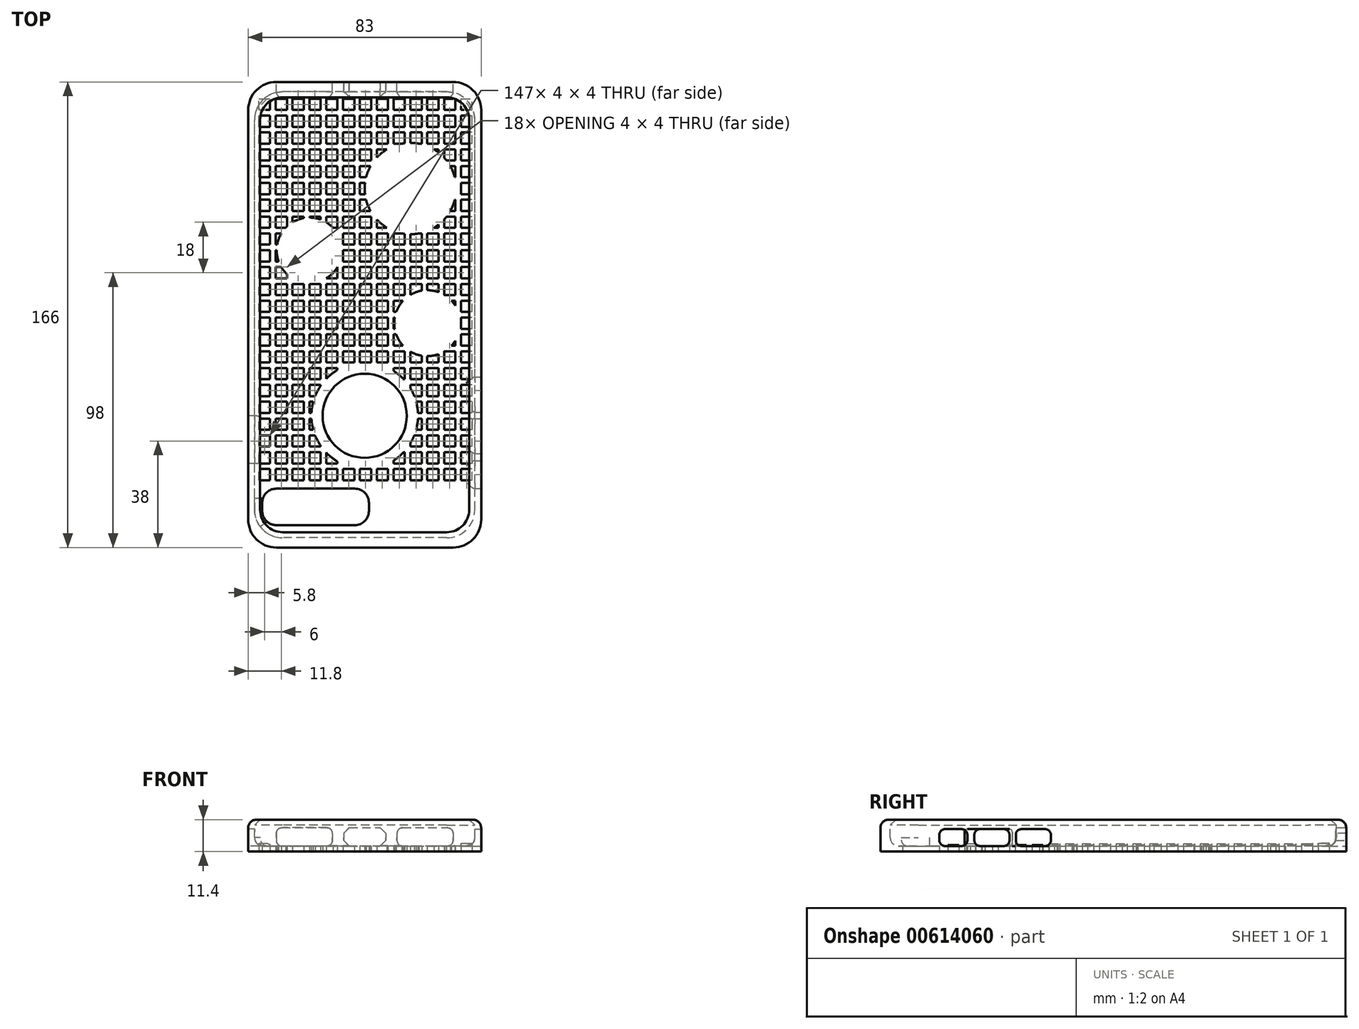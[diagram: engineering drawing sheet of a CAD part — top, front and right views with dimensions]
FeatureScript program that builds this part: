
annotation { "Feature Type Name" : "Feature", "Feature Type Description" : "" }
export const myFeature = defineFeature(function(context is Context, id is Id, definition is map)
    precondition{}
    {
        {
            var Q0;
            Q0=qCreatedBy(makeId("Top.planeOp"),FACE);
            var sketch = newSketch(context, id + "F0", { "sketchPlane" : qUnion([Q0])});
            skLineSegment(sketch, "E0.bottom", {"start": v(41.5, 83) * mm, "end": v(-41.5, 83) * mm});
            skLineSegment(sketch, "E0.top", {"start": v(41.5, -83) * mm, "end": v(-41.5, -83) * mm});
            skLineSegment(sketch, "E0.left", {"start": v(41.5, 83) * mm, "end": v(41.5, -83) * mm});
            skLineSegment(sketch, "E0.right", {"start": v(-41.5, 83) * mm, "end": v(-41.5, -83) * mm});
            skPoint(sketch, "E0.middle", {"position": v(0, 0) * mm});
            skSolve(sketch);
        }
        {
            var Q0;
            Q0=makeQuery(id+"F0.imprint","IMPRINT",FACE,{"disambiguationData":[TD([[makeQuery(id+"F0.imprint","IMPRINT",EDGE,{"derivedFrom":sQuery(id+"F0.wireOp",EDGE,"E0.bottom")}),1.0]])]});
            extrude(context, id + "F1", {"entities" : qUnion([Q0]), "depth" : 9.4 * mm});
        }
        {
            var Q0;
            Q0=makeQuery(id+"F1.opExtrude","CAP_FACE",FACE,{"disambiguationData":[OSD([sQuery(id+"F0.wireOp",EDGE,"E0.bottom"),sQuery(id+"F0.wireOp",EDGE,"E0.top"),sQuery(id+"F0.wireOp",EDGE,"E0.left"),sQuery(id+"F0.wireOp",EDGE,"E0.right")])],"isStart":false});
            var sketch = newSketch(context, id + "F2", { "sketchPlane" : qUnion([Q0])});
            skLineSegment(sketch, "E1.bottom", {"start": v(39.25, -79.5) * mm, "end": v(-39.25, -79.5) * mm});
            skLineSegment(sketch, "E1.top", {"start": v(39.25, 79.5) * mm, "end": v(-39.25, 79.5) * mm});
            skLineSegment(sketch, "E1.left", {"start": v(39.25, -79.5) * mm, "end": v(39.25, 79.5) * mm});
            skLineSegment(sketch, "E1.right", {"start": v(-39.25, -79.5) * mm, "end": v(-39.25, 79.5) * mm});
            skPoint(sketch, "E1.middle", {"position": v(0, 0) * mm});
            skSolve(sketch);
        }
        {
            var Q0;
            Q0=makeQuery(id+"F2.imprint","IMPRINT",FACE,{"disambiguationData":[TD([[makeQuery(id+"F2.imprint","IMPRINT",EDGE,{"derivedFrom":sQuery(id+"F2.wireOp",EDGE,"E1.bottom")}),-1.0]])]});
            extrude(context, id + "F3", {"entities" : qUnion([Q0]), "operationType" : NewBodyOperationType.REMOVE, "oppositeDirection" : true, "depth" : 7.4 * mm});
        }
        {
            var Q0;
            Q0=makeQuery(id+"F3.boolean.opBoolean","COPY",EDGE,{"derivedFrom":makeQuery(id+"F3.opExtrude","SWEPT_EDGE",EDGE,{"disambiguationData":[OSD([sQuery(id+"F2.wireOp",EDGE,"E1.top"),sQuery(id+"F2.wireOp",EDGE,"E1.left")])]})});
            var Q1;
            Q1=makeQuery(id+"F3.boolean.opBoolean","COPY",EDGE,{"derivedFrom":makeQuery(id+"F3.opExtrude","SWEPT_EDGE",EDGE,{"disambiguationData":[OSD([sQuery(id+"F2.wireOp",EDGE,"E1.top"),sQuery(id+"F2.wireOp",EDGE,"E1.right")])]})});
            var Q2;
            Q2=makeQuery(id+"F3.boolean.opBoolean","COPY",EDGE,{"derivedFrom":makeQuery(id+"F3.opExtrude","SWEPT_EDGE",EDGE,{"disambiguationData":[OSD([sQuery(id+"F2.wireOp",EDGE,"E1.bottom"),sQuery(id+"F2.wireOp",EDGE,"E1.left")])]})});
            var Q3;
            Q3=makeQuery(id+"F3.boolean.opBoolean","COPY",EDGE,{"derivedFrom":makeQuery(id+"F3.opExtrude","SWEPT_EDGE",EDGE,{"disambiguationData":[OSD([sQuery(id+"F2.wireOp",EDGE,"E1.bottom"),sQuery(id+"F2.wireOp",EDGE,"E1.right")])]})});
            fillet(context, id + "F4", {"entities" : qUnion([Q0, Q1, Q2, Q3]), "radius" : 10 * mm, "tangentPropagation" : true, "allowEdgeOverflow" : false});
        }
        {
            var Q0;
            Q0=makeQuery(id+"F1.opExtrude","CAP_FACE",FACE,{"disambiguationData":[OSD([sQuery(id+"F0.wireOp",EDGE,"E0.bottom"),sQuery(id+"F0.wireOp",EDGE,"E0.top"),sQuery(id+"F0.wireOp",EDGE,"E0.left"),sQuery(id+"F0.wireOp",EDGE,"E0.right")])],"isStart":true});
            var sketch = newSketch(context, id + "F5", { "sketchPlane" : qUnion([Q0])});
            skLineSegment(sketch, "E2.bottom", {"start": v(1.5, 62) * mm, "end": v(-36.5, 62) * mm});
            skLineSegment(sketch, "E2.top", {"start": v(1.5, 75) * mm, "end": v(-36.5, 75) * mm});
            skLineSegment(sketch, "E2.left", {"start": v(-36.5, 62) * mm, "end": v(-36.5, 75) * mm});
            skLineSegment(sketch, "E2.right", {"start": v(1.5, 62) * mm, "end": v(1.5, 75) * mm});
            skSolve(sketch);
        }
        {
            var Q0;
            Q0=makeQuery(id+"F5.imprint","IMPRINT",FACE,{"disambiguationData":[TD([[makeQuery(id+"F5.imprint","IMPRINT",EDGE,{"derivedFrom":sQuery(id+"F5.wireOp",EDGE,"E2.bottom")}),-1.0]])]});
            extrude(context, id + "F6", {"entities" : qUnion([Q0]), "operationType" : NewBodyOperationType.REMOVE, "oppositeDirection" : true, "depth" : 25 * mm});
        }
        {
            var Q0;
            Q0=makeQuery(id+"F1.opExtrude","SWEPT_EDGE",EDGE,{"disambiguationData":[OSD([sQuery(id+"F0.wireOp",EDGE,"E0.top"),sQuery(id+"F0.wireOp",EDGE,"E0.right")])]});
            var Q1;
            Q1=makeQuery(id+"F1.opExtrude","SWEPT_EDGE",EDGE,{"disambiguationData":[OSD([sQuery(id+"F0.wireOp",EDGE,"E0.top"),sQuery(id+"F0.wireOp",EDGE,"E0.left")])]});
            var Q2;
            Q2=makeQuery(id+"F1.opExtrude","SWEPT_EDGE",EDGE,{"disambiguationData":[OSD([sQuery(id+"F0.wireOp",EDGE,"E0.bottom"),sQuery(id+"F0.wireOp",EDGE,"E0.right")])]});
            var Q3;
            Q3=makeQuery(id+"F1.opExtrude","SWEPT_EDGE",EDGE,{"disambiguationData":[OSD([sQuery(id+"F0.wireOp",EDGE,"E0.bottom"),sQuery(id+"F0.wireOp",EDGE,"E0.left")])]});
            fillet(context, id + "F7", {"entities" : qUnion([Q0, Q1, Q2, Q3]), "radius" : 10 * mm, "tangentPropagation" : true, "allowEdgeOverflow" : false});
        }
        {
            var Q0;
            Q0=makeQuery(id+"F6.boolean.opBoolean","COPY",EDGE,{"derivedFrom":makeQuery(id+"F6.opExtrude","SWEPT_EDGE",EDGE,{"disambiguationData":[OSD([sQuery(id+"F5.wireOp",EDGE,"E2.top"),sQuery(id+"F5.wireOp",EDGE,"E2.left")])]})});
            var Q1;
            Q1=makeQuery(id+"F6.boolean.opBoolean","COPY",EDGE,{"derivedFrom":makeQuery(id+"F6.opExtrude","SWEPT_EDGE",EDGE,{"disambiguationData":[OSD([sQuery(id+"F5.wireOp",EDGE,"E2.bottom"),sQuery(id+"F5.wireOp",EDGE,"E2.left")])]})});
            var Q2;
            Q2=makeQuery(id+"F6.boolean.opBoolean","COPY",EDGE,{"derivedFrom":makeQuery(id+"F6.opExtrude","SWEPT_EDGE",EDGE,{"disambiguationData":[OSD([sQuery(id+"F5.wireOp",EDGE,"E2.top"),sQuery(id+"F5.wireOp",EDGE,"E2.right")])]})});
            var Q3;
            Q3=makeQuery(id+"F6.boolean.opBoolean","COPY",EDGE,{"derivedFrom":makeQuery(id+"F6.opExtrude","SWEPT_EDGE",EDGE,{"disambiguationData":[OSD([sQuery(id+"F5.wireOp",EDGE,"E2.bottom"),sQuery(id+"F5.wireOp",EDGE,"E2.right")])]})});
            fillet(context, id + "F8", {"entities" : qUnion([Q0, Q1, Q2, Q3]), "radius" : 5 * mm, "tangentPropagation" : true, "allowEdgeOverflow" : false});
        }
        {
            var Q0;
            Q0=makeQuery(id+"F1.opExtrude","SWEPT_FACE",FACE,{"disambiguationData":[OSD([sQuery(id+"F0.wireOp",EDGE,"E0.bottom")])]});
            var sketch = newSketch(context, id + "F9", { "sketchPlane" : qUnion([Q0])});
            skLineSegment(sketch, "E3.bottom", {"start": v(7.5, 8.5) * mm, "end": v(-7.5, 8.5) * mm});
            skLineSegment(sketch, "E3.top", {"start": v(7.5, 2) * mm, "end": v(-7.5, 2) * mm});
            skLineSegment(sketch, "E3.left", {"start": v(7.5, 8.5) * mm, "end": v(7.5, 2) * mm});
            skLineSegment(sketch, "E3.right", {"start": v(-7.5, 8.5) * mm, "end": v(-7.5, 2) * mm});
            skPoint(sketch, "E3.middle", {"position": v(0, 5.25) * mm});
            skLineSegment(sketch, "E4.bottom", {"start": v(-11.5, 8.5) * mm, "end": v(-31.5, 8.5) * mm});
            skLineSegment(sketch, "E4.top", {"start": v(-11.5, 2) * mm, "end": v(-31.5, 2) * mm});
            skLineSegment(sketch, "E4.left", {"start": v(-11.5, 8.5) * mm, "end": v(-11.5, 2) * mm});
            skLineSegment(sketch, "E4.right", {"start": v(-31.5, 8.5) * mm, "end": v(-31.5, 2) * mm});
            skLineSegment(sketch, "E5.bottom", {"start": v(11.5, 8.5) * mm, "end": v(31.5, 8.5) * mm});
            skLineSegment(sketch, "E5.top", {"start": v(11.5, 2) * mm, "end": v(31.5, 2) * mm});
            skLineSegment(sketch, "E5.left", {"start": v(11.5, 8.5) * mm, "end": v(11.5, 2) * mm});
            skLineSegment(sketch, "E5.right", {"start": v(31.5, 8.5) * mm, "end": v(31.5, 2) * mm});
            skSolve(sketch);
        }
        {
            var Q0;
            Q0=qSketchRegion(id+"F9",true);
            extrude(context, id + "F10", {"entities" : qUnion([Q0]), "operationType" : NewBodyOperationType.REMOVE, "oppositeDirection" : true, "depth" : 25 * mm});
        }
        {
            var Q0;
            Q0=makeQuery(id+"F1.opExtrude","SWEPT_FACE",FACE,{"disambiguationData":[OSD([sQuery(id+"F0.wireOp",EDGE,"E0.left")])]});
            var sketch = newSketch(context, id + "F11", { "sketchPlane" : qUnion([Q0])});
            skLineSegment(sketch, "E6.bottom", {"start": v(-62, 8) * mm, "end": v(-52, 8) * mm});
            skLineSegment(sketch, "E6.top", {"start": v(-62, 2) * mm, "end": v(-52, 2) * mm});
            skLineSegment(sketch, "E6.left", {"start": v(-62, 8) * mm, "end": v(-62, 2) * mm});
            skLineSegment(sketch, "E6.right", {"start": v(-52, 8) * mm, "end": v(-52, 2) * mm});
            skLineSegment(sketch, "E7.bottom", {"start": v(-49.5, 2) * mm, "end": v(-37, 2) * mm});
            skLineSegment(sketch, "E7.top", {"start": v(-49.5, 8) * mm, "end": v(-37, 8) * mm});
            skLineSegment(sketch, "E7.left", {"start": v(-49.5, 2) * mm, "end": v(-49.5, 8) * mm});
            skLineSegment(sketch, "E7.right", {"start": v(-37, 2) * mm, "end": v(-37, 8) * mm});
            skLineSegment(sketch, "E8.bottom", {"start": v(-34.74, 2) * mm, "end": v(-22.24, 2) * mm});
            skLineSegment(sketch, "E8.top", {"start": v(-34.74, 8) * mm, "end": v(-22.24, 8) * mm});
            skLineSegment(sketch, "E8.left", {"start": v(-34.74, 2) * mm, "end": v(-34.74, 8) * mm});
            skLineSegment(sketch, "E8.right", {"start": v(-22.24, 2) * mm, "end": v(-22.24, 8) * mm});
            skSolve(sketch);
        }
        {
            var Q0;
            Q0=makeQuery(id+"F11.imprint","IMPRINT",FACE,{"disambiguationData":[TD([[makeQuery(id+"F11.imprint","IMPRINT",EDGE,{"derivedFrom":sQuery(id+"F11.wireOp",EDGE,"E6.bottom")}),-1.0]])]});
            var Q1;
            Q1=makeQuery(id+"F11.imprint","IMPRINT",FACE,{"disambiguationData":[TD([[makeQuery(id+"F11.imprint","IMPRINT",EDGE,{"derivedFrom":sQuery(id+"F11.wireOp",EDGE,"E7.bottom")}),1.0]])]});
            var Q2;
            Q2=makeQuery(id+"F11.imprint","IMPRINT",FACE,{"disambiguationData":[TD([[makeQuery(id+"F11.imprint","IMPRINT",EDGE,{"derivedFrom":sQuery(id+"F11.wireOp",EDGE,"E8.bottom")}),1.0]])]});
            extrude(context, id + "F12", {"entities" : qUnion([Q0, Q1, Q2]), "operationType" : NewBodyOperationType.REMOVE, "oppositeDirection" : true, "depth" : 3 * mm});
        }
        {
            var Q0;
            Q0=makeQuery(id+"F1.opExtrude","SWEPT_FACE",FACE,{"disambiguationData":[OSD([sQuery(id+"F0.wireOp",EDGE,"E0.right")])]});
            var sketch = newSketch(context, id + "F13", { "sketchPlane" : qUnion([Q0])});
            skLineSegment(sketch, "E9.bottom", {"start": v(53, 8) * mm, "end": v(36, 8) * mm});
            skLineSegment(sketch, "E9.top", {"start": v(53, 2) * mm, "end": v(36, 2) * mm});
            skLineSegment(sketch, "E9.left", {"start": v(53, 8) * mm, "end": v(53, 2) * mm});
            skLineSegment(sketch, "E9.right", {"start": v(36, 8) * mm, "end": v(36, 2) * mm});
            skSolve(sketch);
        }
        {
            var Q0;
            Q0=makeQuery(id+"F13.imprint","IMPRINT",FACE,{"disambiguationData":[TD([[makeQuery(id+"F13.imprint","IMPRINT",EDGE,{"derivedFrom":sQuery(id+"F13.wireOp",EDGE,"E9.bottom")}),1.0]])]});
            extrude(context, id + "F14", {"entities" : qUnion([Q0]), "operationType" : NewBodyOperationType.REMOVE, "oppositeDirection" : true, "depth" : 5 * mm});
        }
        {
            var Q0;
            Q0=makeQuery(id+"F1.opExtrude","CAP_FACE",FACE,{"disambiguationData":[OSD([sQuery(id+"F0.wireOp",EDGE,"E0.bottom"),sQuery(id+"F0.wireOp",EDGE,"E0.top"),sQuery(id+"F0.wireOp",EDGE,"E0.left"),sQuery(id+"F0.wireOp",EDGE,"E0.right")])],"isStart":false});
            var sketch = newSketch(context, id + "F15", { "sketchPlane" : qUnion([Q0])});
            skArc(sketch, "E10.0", {"start": v(-31.5, 83) * mm, "mid": v(-38.57, 80.07) * mm, "end": v(-41.5, 73) * mm});
            skLineSegment(sketch, "E11.0", {"start": v(31.5, 83) * mm, "end": v(-31.5, 83) * mm});
            skArc(sketch, "E12.0", {"start": v(41.5, 73) * mm, "mid": v(38.57, 80.07) * mm, "end": v(31.5, 83) * mm});
            skLineSegment(sketch, "E13.0", {"start": v(41.5, 73) * mm, "end": v(41.5, -73) * mm});
            skArc(sketch, "E14.0", {"start": v(31.5, -83) * mm, "mid": v(38.57, -80.07) * mm, "end": v(41.5, -73) * mm});
            skLineSegment(sketch, "E15.0", {"start": v(31.5, -83) * mm, "end": v(-31.5, -83) * mm});
            skArc(sketch, "E16.0", {"start": v(-41.5, -73) * mm, "mid": v(-38.57, -80.07) * mm, "end": v(-31.5, -83) * mm});
            skLineSegment(sketch, "E17.0", {"start": v(-41.5, 73) * mm, "end": v(-41.5, -73) * mm});
            skLineSegment(sketch, "E18.0", {"start": v(-36.25, -69.5) * mm, "end": v(-36.25, 69.5) * mm});
            skArc(sketch, "E18.1", {"start": v(-29.25, -76.5) * mm, "mid": v(-34.2, -74.45) * mm, "end": v(-36.25, -69.5) * mm});
            skArc(sketch, "E18.2", {"start": v(-36.25, 69.5) * mm, "mid": v(-34.2, 74.45) * mm, "end": v(-29.25, 76.5) * mm});
            skLineSegment(sketch, "E18.3", {"start": v(29.25, -76.5) * mm, "end": v(-29.25, -76.5) * mm});
            skLineSegment(sketch, "E18.4", {"start": v(29.25, 76.5) * mm, "end": v(-29.25, 76.5) * mm});
            skArc(sketch, "E18.5", {"start": v(29.25, 76.5) * mm, "mid": v(34.2, 74.45) * mm, "end": v(36.25, 69.5) * mm});
            skLineSegment(sketch, "E18.6", {"start": v(36.25, -69.5) * mm, "end": v(36.25, 69.5) * mm});
            skArc(sketch, "E18.7", {"start": v(36.25, -69.5) * mm, "mid": v(34.2, -74.45) * mm, "end": v(29.25, -76.5) * mm});
            skSolve(sketch);
        }
        {
            var Q0;
            Q0=qSketchRegion(id+"F15",true);
            extrude(context, id + "F16", {"entities" : qUnion([Q0]), "operationType" : NewBodyOperationType.ADD, "depth" : 2 * mm});
        }
        {
            var Q0;
            Q0=makeQuery(id+"F16.opExtrude","CAP_EDGE",EDGE,{"disambiguationData":[OSD([sQuery(id+"F15.wireOp",EDGE,"70d5f63f-d463-4b85-bbfd-dc065f4d9ea8.0")])],"isStart":true});
            var Q1;
            Q1=makeQuery(id+"F16.opExtrude","CAP_EDGE",EDGE,{"disambiguationData":[OSD([sQuery(id+"F15.wireOp",EDGE,"E18.0")])],"isStart":true});
            chamfer(context, id + "F17", {"entities" : qUnion([Q0, Q1]), "width" : 3 * mm, "tangentPropagation" : true});
        }
        {
            var Q0;
            Q0=makeQuery(id+"F14.boolean.opBoolean","COPY",EDGE,{"derivedFrom":makeQuery(id+"F14.opExtrude","SWEPT_EDGE",EDGE,{"disambiguationData":[OSD([sQuery(id+"F13.wireOp",EDGE,"E9.bottom"),sQuery(id+"F13.wireOp",EDGE,"E9.right")])]})});
            var Q1;
            Q1=makeQuery(id+"F14.boolean.opBoolean","COPY",EDGE,{"derivedFrom":makeQuery(id+"F14.opExtrude","SWEPT_EDGE",EDGE,{"disambiguationData":[OSD([sQuery(id+"F13.wireOp",EDGE,"E9.top"),sQuery(id+"F13.wireOp",EDGE,"E9.right")])]})});
            var Q2;
            Q2=makeQuery(id+"F14.boolean.opBoolean","COPY",EDGE,{"derivedFrom":makeQuery(id+"F14.opExtrude","SWEPT_EDGE",EDGE,{"disambiguationData":[OSD([sQuery(id+"F13.wireOp",EDGE,"E9.top"),sQuery(id+"F13.wireOp",EDGE,"E9.left")])]})});
            var Q3;
            Q3=makeQuery(id+"F14.boolean.opBoolean","COPY",EDGE,{"derivedFrom":makeQuery(id+"F14.opExtrude","SWEPT_EDGE",EDGE,{"disambiguationData":[OSD([sQuery(id+"F13.wireOp",EDGE,"E9.bottom"),sQuery(id+"F13.wireOp",EDGE,"E9.left")])]})});
            fillet(context, id + "F18", {"entities" : qUnion([Q0, Q1, Q2, Q3]), "radius" : 1 * mm, "tangentPropagation" : true, "allowEdgeOverflow" : false});
        }
        {
            var Q0;
            Q0=makeQuery(id+"F12.boolean.opBoolean","COPY",EDGE,{"derivedFrom":makeQuery(id+"F12.opExtrude","SWEPT_EDGE",EDGE,{"disambiguationData":[OSD([sQuery(id+"F11.wireOp",EDGE,"E6.top"),sQuery(id+"F11.wireOp",EDGE,"E6.right")])]})});
            var Q1;
            Q1=makeQuery(id+"F12.boolean.opBoolean","COPY",EDGE,{"derivedFrom":makeQuery(id+"F12.opExtrude","SWEPT_EDGE",EDGE,{"disambiguationData":[OSD([sQuery(id+"F11.wireOp",EDGE,"E7.bottom"),sQuery(id+"F11.wireOp",EDGE,"E7.right")])]})});
            var Q2;
            Q2=makeQuery(id+"F12.boolean.opBoolean","COPY",EDGE,{"derivedFrom":makeQuery(id+"F12.opExtrude","SWEPT_EDGE",EDGE,{"disambiguationData":[OSD([sQuery(id+"F11.wireOp",EDGE,"E8.bottom"),sQuery(id+"F11.wireOp",EDGE,"E8.right")])]})});
            var Q3;
            Q3=makeQuery(id+"F12.boolean.opBoolean","COPY",EDGE,{"derivedFrom":makeQuery(id+"F12.opExtrude","SWEPT_EDGE",EDGE,{"disambiguationData":[OSD([sQuery(id+"F11.wireOp",EDGE,"E7.bottom"),sQuery(id+"F11.wireOp",EDGE,"E7.left")])]})});
            var Q4;
            Q4=makeQuery(id+"F12.boolean.opBoolean","COPY",EDGE,{"derivedFrom":makeQuery(id+"F12.opExtrude","SWEPT_EDGE",EDGE,{"disambiguationData":[OSD([sQuery(id+"F11.wireOp",EDGE,"E8.bottom"),sQuery(id+"F11.wireOp",EDGE,"E8.left")])]})});
            var Q5;
            Q5=makeQuery(id+"F12.boolean.opBoolean","COPY",EDGE,{"derivedFrom":makeQuery(id+"F12.opExtrude","SWEPT_EDGE",EDGE,{"disambiguationData":[OSD([sQuery(id+"F11.wireOp",EDGE,"E6.top"),sQuery(id+"F11.wireOp",EDGE,"E6.left")])]})});
            var Q6;
            Q6=makeQuery(id+"F12.boolean.opBoolean","COPY",EDGE,{"derivedFrom":makeQuery(id+"F12.opExtrude","SWEPT_EDGE",EDGE,{"disambiguationData":[OSD([sQuery(id+"F11.wireOp",EDGE,"E6.bottom"),sQuery(id+"F11.wireOp",EDGE,"E6.left")])]})});
            var Q7;
            Q7=makeQuery(id+"F12.boolean.opBoolean","COPY",EDGE,{"derivedFrom":makeQuery(id+"F12.opExtrude","SWEPT_EDGE",EDGE,{"disambiguationData":[OSD([sQuery(id+"F11.wireOp",EDGE,"E7.top"),sQuery(id+"F11.wireOp",EDGE,"E7.left")])]})});
            var Q8;
            Q8=makeQuery(id+"F12.boolean.opBoolean","COPY",EDGE,{"derivedFrom":makeQuery(id+"F12.opExtrude","SWEPT_EDGE",EDGE,{"disambiguationData":[OSD([sQuery(id+"F11.wireOp",EDGE,"E8.top"),sQuery(id+"F11.wireOp",EDGE,"E8.left")])]})});
            var Q9;
            Q9=makeQuery(id+"F12.boolean.opBoolean","COPY",EDGE,{"derivedFrom":makeQuery(id+"F12.opExtrude","SWEPT_EDGE",EDGE,{"disambiguationData":[OSD([sQuery(id+"F11.wireOp",EDGE,"E8.top"),sQuery(id+"F11.wireOp",EDGE,"E8.right")])]})});
            var Q10;
            Q10=makeQuery(id+"F12.boolean.opBoolean","COPY",EDGE,{"derivedFrom":makeQuery(id+"F12.opExtrude","SWEPT_EDGE",EDGE,{"disambiguationData":[OSD([sQuery(id+"F11.wireOp",EDGE,"E7.top"),sQuery(id+"F11.wireOp",EDGE,"E7.right")])]})});
            var Q11;
            Q11=makeQuery(id+"F12.boolean.opBoolean","COPY",EDGE,{"derivedFrom":makeQuery(id+"F12.opExtrude","SWEPT_EDGE",EDGE,{"disambiguationData":[OSD([sQuery(id+"F11.wireOp",EDGE,"E6.bottom"),sQuery(id+"F11.wireOp",EDGE,"E6.right")])]})});
            fillet(context, id + "F19", {"entities" : qUnion([Q0, Q1, Q2, Q3, Q4, Q5, Q6, Q7, Q8, Q9, Q10, Q11]), "radius" : 2 * mm, "tangentPropagation" : true, "allowEdgeOverflow" : false});
        }
        {
            var Q0;
            Q0=makeQuery(id+"F10.boolean.opBoolean","COPY",EDGE,{"derivedFrom":makeQuery(id+"F10.opExtrude","SWEPT_EDGE",EDGE,{"disambiguationData":[OSD([sQuery(id+"F9.wireOp",EDGE,"E3.bottom"),sQuery(id+"F9.wireOp",EDGE,"E3.right")])]})});
            var Q1;
            Q1=makeQuery(id+"F10.boolean.opBoolean","COPY",EDGE,{"derivedFrom":makeQuery(id+"F10.opExtrude","SWEPT_EDGE",EDGE,{"disambiguationData":[OSD([sQuery(id+"F9.wireOp",EDGE,"E3.top"),sQuery(id+"F9.wireOp",EDGE,"E3.left")])]})});
            var Q2;
            Q2=makeQuery(id+"F10.boolean.opBoolean","COPY",EDGE,{"derivedFrom":makeQuery(id+"F10.opExtrude","SWEPT_EDGE",EDGE,{"disambiguationData":[OSD([sQuery(id+"F9.wireOp",EDGE,"E3.bottom"),sQuery(id+"F9.wireOp",EDGE,"E3.left")])]})});
            var Q3;
            Q3=makeQuery(id+"F10.boolean.opBoolean","COPY",EDGE,{"derivedFrom":makeQuery(id+"F10.opExtrude","SWEPT_EDGE",EDGE,{"disambiguationData":[OSD([sQuery(id+"F9.wireOp",EDGE,"E3.top"),sQuery(id+"F9.wireOp",EDGE,"E3.right")])]})});
            chamfer(context, id + "F20", {"entities" : qUnion([Q0, Q1, Q2, Q3]), "width" : 2 * mm, "tangentPropagation" : true});
        }
        {
            var Q0;
            Q0=makeQuery(id+"F10.boolean.opBoolean","COPY",EDGE,{"derivedFrom":makeQuery(id+"F10.opExtrude","SWEPT_EDGE",EDGE,{"disambiguationData":[OSD([sQuery(id+"F9.wireOp",EDGE,"E4.bottom"),sQuery(id+"F9.wireOp",EDGE,"E4.left")])]})});
            var Q1;
            Q1=makeQuery(id+"F10.boolean.opBoolean","COPY",EDGE,{"derivedFrom":makeQuery(id+"F10.opExtrude","SWEPT_EDGE",EDGE,{"disambiguationData":[OSD([sQuery(id+"F0.wireOp",EDGE,"E0.bottom"),sQuery(id+"F0.wireOp",EDGE,"E0.right"),sQuery(id+"F9.wireOp",EDGE,"E5.bottom"),sQuery(id+"F9.wireOp",EDGE,"E5.right")])]})});
            var Q2;
            Q2=makeQuery(id+"F10.boolean.opBoolean","COPY",EDGE,{"derivedFrom":makeQuery(id+"F10.opExtrude","SWEPT_EDGE",EDGE,{"disambiguationData":[OSD([sQuery(id+"F0.wireOp",EDGE,"E0.bottom"),sQuery(id+"F0.wireOp",EDGE,"E0.right"),sQuery(id+"F9.wireOp",EDGE,"E5.top"),sQuery(id+"F9.wireOp",EDGE,"E5.right")])]})});
            var Q3;
            Q3=makeQuery(id+"F10.boolean.opBoolean","COPY",EDGE,{"derivedFrom":makeQuery(id+"F10.opExtrude","SWEPT_EDGE",EDGE,{"disambiguationData":[OSD([sQuery(id+"F9.wireOp",EDGE,"E4.top"),sQuery(id+"F9.wireOp",EDGE,"E4.left")])]})});
            var Q4;
            Q4=makeQuery(id+"F10.boolean.opBoolean","COPY",EDGE,{"derivedFrom":makeQuery(id+"F10.opExtrude","SWEPT_EDGE",EDGE,{"disambiguationData":[OSD([sQuery(id+"F0.wireOp",EDGE,"E0.bottom"),sQuery(id+"F0.wireOp",EDGE,"E0.left"),sQuery(id+"F9.wireOp",EDGE,"E4.top"),sQuery(id+"F9.wireOp",EDGE,"E4.right")])]})});
            var Q5;
            Q5=makeQuery(id+"F10.boolean.opBoolean","COPY",EDGE,{"derivedFrom":makeQuery(id+"F10.opExtrude","SWEPT_EDGE",EDGE,{"disambiguationData":[OSD([sQuery(id+"F9.wireOp",EDGE,"E5.top"),sQuery(id+"F9.wireOp",EDGE,"E5.left")])]})});
            var Q6;
            Q6=makeQuery(id+"F10.boolean.opBoolean","COPY",EDGE,{"derivedFrom":makeQuery(id+"F10.opExtrude","SWEPT_EDGE",EDGE,{"disambiguationData":[OSD([sQuery(id+"F9.wireOp",EDGE,"E5.bottom"),sQuery(id+"F9.wireOp",EDGE,"E5.left")])]})});
            var Q7;
            Q7=makeQuery(id+"F10.boolean.opBoolean","COPY",EDGE,{"derivedFrom":makeQuery(id+"F10.opExtrude","SWEPT_EDGE",EDGE,{"disambiguationData":[OSD([sQuery(id+"F0.wireOp",EDGE,"E0.bottom"),sQuery(id+"F0.wireOp",EDGE,"E0.left"),sQuery(id+"F9.wireOp",EDGE,"E4.bottom"),sQuery(id+"F9.wireOp",EDGE,"E4.right")])]})});
            fillet(context, id + "F21", {"entities" : qUnion([Q0, Q1, Q2, Q3, Q4, Q5, Q6, Q7]), "radius" : 2 * mm, "tangentPropagation" : true, "allowEdgeOverflow" : false});
        }
        {
            var Q0;
            Q0=makeQuery(id+"F16.opExtrude","CAP_EDGE",EDGE,{"disambiguationData":[OSD([sQuery(id+"F15.wireOp",EDGE,"E13.0")])],"isStart":false});
            fillet(context, id + "F22", {"entities" : qUnion([Q0]), "radius" : 3 * mm, "tangentPropagation" : true, "allowEdgeOverflow" : false});
        }
        {
            var Q0;
            {var subQ0=sQuery(id+"F2.wireOp",EDGE,"E1.right");Q0=makeQuery(id+"F14.boolean.opBoolean","SPLIT",EDGE,{"disambiguationData":[TD([makeQuery(id+"F14.opExtrude","SWEPT_FACE",FACE,{"disambiguationData":[OSD([sQuery(id+"F13.wireOp",EDGE,"E9.left")])]})])],"derivedFrom":makeQuery(id+"F3.boolean.opBoolean","COPY",EDGE,{"derivedFrom":makeQuery(id+"F3.opExtrude","CAP_EDGE",EDGE,{"disambiguationData":[OSD([subQ0])],"isStart":false})})});}
            var Q1;
            {var subQ0=sQuery(id+"F2.wireOp",EDGE,"E1.right");Q1=makeQuery(id+"FE60Vq3lKrfm1dI_2.splitOp","SPLIT",EDGE,{"derivedFrom":makeQuery(id+"F14.boolean.opBoolean","SPLIT",EDGE,{"disambiguationData":[TD([makeQuery(id+"F14.opExtrude","SWEPT_FACE",FACE,{"disambiguationData":[OSD([sQuery(id+"F13.wireOp",EDGE,"E9.right")])]})])],"derivedFrom":makeQuery(id+"F3.boolean.opBoolean","COPY",EDGE,{"derivedFrom":makeQuery(id+"F3.opExtrude","CAP_EDGE",EDGE,{"disambiguationData":[OSD([subQ0])],"isStart":false})})}),"isFromBackBody":true});}
            var Q2;
            {var subQ0=sQuery(id+"F2.wireOp",EDGE,"E1.right");Q2=makeQuery(id+"FE60Vq3lKrfm1dI_2.splitOp","SPLIT",EDGE,{"derivedFrom":makeQuery(id+"F14.boolean.opBoolean","SPLIT",EDGE,{"disambiguationData":[TD([makeQuery(id+"F14.opExtrude","SWEPT_FACE",FACE,{"disambiguationData":[OSD([sQuery(id+"F13.wireOp",EDGE,"E9.right")])]})])],"derivedFrom":makeQuery(id+"F3.boolean.opBoolean","COPY",EDGE,{"derivedFrom":makeQuery(id+"F3.opExtrude","CAP_EDGE",EDGE,{"disambiguationData":[OSD([subQ0])],"isStart":false})})})});}
            var Q3;
            {var subQ0=sQuery(id+"F2.wireOp",EDGE,"E1.top");Q3=makeQuery(id+"F10.boolean.opBoolean","SPLIT",EDGE,{"disambiguationData":[TD([makeQuery(id+"F10.opExtrude","SWEPT_FACE",FACE,{"disambiguationData":[OSD([sQuery(id+"F9.wireOp",EDGE,"E3.left")])]})])],"derivedFrom":makeQuery(id+"F3.boolean.opBoolean","COPY",EDGE,{"derivedFrom":makeQuery(id+"F3.opExtrude","CAP_EDGE",EDGE,{"disambiguationData":[OSD([subQ0])],"isStart":false})})});}
            var Q4;
            {var subQ0=sQuery(id+"F2.wireOp",EDGE,"E1.top");Q4=makeQuery(id+"F10.boolean.opBoolean","SPLIT",EDGE,{"disambiguationData":[TD([makeQuery(id+"F10.opExtrude","SWEPT_FACE",FACE,{"disambiguationData":[OSD([sQuery(id+"F9.wireOp",EDGE,"E3.right")])]})])],"derivedFrom":makeQuery(id+"F3.boolean.opBoolean","COPY",EDGE,{"derivedFrom":makeQuery(id+"F3.opExtrude","CAP_EDGE",EDGE,{"disambiguationData":[OSD([subQ0])],"isStart":false})})});}
            var Q5;
            {var subQ0=sQuery(id+"F2.wireOp",EDGE,"E1.left");var subQ1=sQuery(id+"F2.wireOp",EDGE,"E1.top");Q5=makeQuery(id+"F4.opFillet","BLEND_EDGE",EDGE,{"blendedFrom":[makeQuery(id+"F3.boolean.opBoolean","COPY",EDGE,{"derivedFrom":makeQuery(id+"F3.opExtrude","SWEPT_EDGE",EDGE,{"disambiguationData":[OSD([subQ1,subQ0])]})}),makeQuery(id+"F3.boolean.opBoolean","COPY",FACE,{"derivedFrom":makeQuery(id+"F3.opExtrude","CAP_FACE",FACE,{"disambiguationData":[OSD([sQuery(id+"F2.wireOp",EDGE,"E1.bottom"),subQ1,subQ0,sQuery(id+"F2.wireOp",EDGE,"E1.right")])],"isStart":false})})],"blendedInto":[makeQuery(id+"F3.boolean.opBoolean","COPY",FACE,{"derivedFrom":makeQuery(id+"F3.opExtrude","CAP_FACE",FACE,{"disambiguationData":[OSD([sQuery(id+"F2.wireOp",EDGE,"E1.bottom"),subQ1,subQ0,sQuery(id+"F2.wireOp",EDGE,"E1.right")])],"isStart":false})})]});}
            var Q6;
            {var subQ0=sQuery(id+"F2.wireOp",EDGE,"E1.left");Q6=makeQuery(id+"F12.boolean.opBoolean","SPLIT",EDGE,{"disambiguationData":[TD([makeQuery(id+"F12.opExtrude","SWEPT_FACE",FACE,{"disambiguationData":[OSD([sQuery(id+"F11.wireOp",EDGE,"E7.right")])]})])],"derivedFrom":makeQuery(id+"F3.boolean.opBoolean","COPY",EDGE,{"derivedFrom":makeQuery(id+"F3.opExtrude","CAP_EDGE",EDGE,{"disambiguationData":[OSD([subQ0])],"isStart":false})})});}
            var Q7;
            {var subQ0=sQuery(id+"F2.wireOp",EDGE,"E1.left");Q7=makeQuery(id+"F12.boolean.opBoolean","SPLIT",EDGE,{"disambiguationData":[TD([makeQuery(id+"F12.opExtrude","SWEPT_FACE",FACE,{"disambiguationData":[OSD([sQuery(id+"F11.wireOp",EDGE,"E6.right")])]})])],"derivedFrom":makeQuery(id+"F3.boolean.opBoolean","COPY",EDGE,{"derivedFrom":makeQuery(id+"F3.opExtrude","CAP_EDGE",EDGE,{"disambiguationData":[OSD([subQ0])],"isStart":false})})});}
            var Q8;
            {var subQ0=sQuery(id+"F2.wireOp",EDGE,"E1.left");Q8=makeQuery(id+"FE60Vq3lKrfm1dI_2.splitOp","SPLIT",EDGE,{"derivedFrom":makeQuery(id+"F12.boolean.opBoolean","SPLIT",EDGE,{"disambiguationData":[TD([makeQuery(id+"F12.opExtrude","SWEPT_FACE",FACE,{"disambiguationData":[OSD([sQuery(id+"F11.wireOp",EDGE,"E8.right")])]})])],"derivedFrom":makeQuery(id+"F3.boolean.opBoolean","COPY",EDGE,{"derivedFrom":makeQuery(id+"F3.opExtrude","CAP_EDGE",EDGE,{"disambiguationData":[OSD([subQ0])],"isStart":false})})}),"isFromBackBody":true});}
            fillet(context, id + "F23", {"entities" : qUnion([Q0, Q1, Q2, Q3, Q4, Q5, Q6, Q7, Q8]), "radius" : 3 * mm, "tangentPropagation" : true, "allowEdgeOverflow" : false});
        }
        {
            var Q0;
            Q0=makeQuery(id+"F1.opExtrude","CAP_FACE",FACE,{"disambiguationData":[OSD([sQuery(id+"F0.wireOp",EDGE,"E0.bottom"),sQuery(id+"F0.wireOp",EDGE,"E0.top"),sQuery(id+"F0.wireOp",EDGE,"E0.left"),sQuery(id+"F0.wireOp",EDGE,"E0.right")])],"isStart":true});
            var sketch = newSketch(context, id + "F24", { "sketchPlane" : qUnion([Q0])});
            skLineSegment(sketch, "E19.bottom", {"start": v(-37.7, 59) * mm, "end": v(-33.7, 59) * mm});
            skLineSegment(sketch, "E19.top", {"start": v(-37.7, 55) * mm, "end": v(-33.7, 55) * mm});
            skLineSegment(sketch, "E19.left", {"start": v(-37.7, 59) * mm, "end": v(-37.7, 55) * mm});
            skLineSegment(sketch, "E19.right", {"start": v(-33.7, 59) * mm, "end": v(-33.7, 55) * mm});
            skLineSegment(sketch, "E20.0.1.0", {"start": v(-37.7, 53) * mm, "end": v(-33.7, 53) * mm});
            skLineSegment(sketch, "E20.0.1.1", {"start": v(-37.7, 53) * mm, "end": v(-37.7, 49) * mm});
            skLineSegment(sketch, "E20.0.1.2", {"start": v(-37.7, 49) * mm, "end": v(-33.7, 49) * mm});
            skLineSegment(sketch, "E20.0.1.3", {"start": v(-33.7, 53) * mm, "end": v(-33.7, 49) * mm});
            skLineSegment(sketch, "E20.0.2.0", {"start": v(-37.7, 47) * mm, "end": v(-33.7, 47) * mm});
            skLineSegment(sketch, "E20.0.2.1", {"start": v(-37.7, 47) * mm, "end": v(-37.7, 43) * mm});
            skLineSegment(sketch, "E20.0.2.2", {"start": v(-37.7, 43) * mm, "end": v(-33.7, 43) * mm});
            skLineSegment(sketch, "E20.0.2.3", {"start": v(-33.7, 47) * mm, "end": v(-33.7, 43) * mm});
            skLineSegment(sketch, "E20.0.3.0", {"start": v(-37.7, 41) * mm, "end": v(-33.7, 41) * mm});
            skLineSegment(sketch, "E20.0.3.1", {"start": v(-37.7, 41) * mm, "end": v(-37.7, 37) * mm});
            skLineSegment(sketch, "E20.0.3.2", {"start": v(-37.7, 37) * mm, "end": v(-33.7, 37) * mm});
            skLineSegment(sketch, "E20.0.3.3", {"start": v(-33.7, 41) * mm, "end": v(-33.7, 37) * mm});
            skLineSegment(sketch, "E20.0.4.0", {"start": v(-37.7, 35) * mm, "end": v(-33.7, 35) * mm});
            skLineSegment(sketch, "E20.0.4.1", {"start": v(-37.7, 35) * mm, "end": v(-37.7, 31) * mm});
            skLineSegment(sketch, "E20.0.4.2", {"start": v(-37.7, 31) * mm, "end": v(-33.7, 31) * mm});
            skLineSegment(sketch, "E20.0.4.3", {"start": v(-33.7, 35) * mm, "end": v(-33.7, 31) * mm});
            skLineSegment(sketch, "E20.0.5.0", {"start": v(-37.7, 29) * mm, "end": v(-33.7, 29) * mm});
            skLineSegment(sketch, "E20.0.5.1", {"start": v(-37.7, 29) * mm, "end": v(-37.7, 25) * mm});
            skLineSegment(sketch, "E20.0.5.2", {"start": v(-37.7, 25) * mm, "end": v(-33.7, 25) * mm});
            skLineSegment(sketch, "E20.0.5.3", {"start": v(-33.7, 29) * mm, "end": v(-33.7, 25) * mm});
            skLineSegment(sketch, "E20.0.6.0", {"start": v(-37.7, 23) * mm, "end": v(-33.7, 23) * mm});
            skLineSegment(sketch, "E20.0.6.1", {"start": v(-37.7, 23) * mm, "end": v(-37.7, 19) * mm});
            skLineSegment(sketch, "E20.0.6.2", {"start": v(-37.7, 19) * mm, "end": v(-33.7, 19) * mm});
            skLineSegment(sketch, "E20.0.6.3", {"start": v(-33.7, 23) * mm, "end": v(-33.7, 19) * mm});
            skLineSegment(sketch, "E20.0.7.0", {"start": v(-37.7, 17) * mm, "end": v(-33.7, 17) * mm});
            skLineSegment(sketch, "E20.0.7.1", {"start": v(-37.7, 17) * mm, "end": v(-37.7, 13) * mm});
            skLineSegment(sketch, "E20.0.7.2", {"start": v(-37.7, 13) * mm, "end": v(-33.7, 13) * mm});
            skLineSegment(sketch, "E20.0.7.3", {"start": v(-33.7, 17) * mm, "end": v(-33.7, 13) * mm});
            skLineSegment(sketch, "E20.0.8.0", {"start": v(-37.7, 11) * mm, "end": v(-33.7, 11) * mm});
            skLineSegment(sketch, "E20.0.8.1", {"start": v(-37.7, 11) * mm, "end": v(-37.7, 7) * mm});
            skLineSegment(sketch, "E20.0.8.2", {"start": v(-37.7, 7) * mm, "end": v(-33.7, 7) * mm});
            skLineSegment(sketch, "E20.0.8.3", {"start": v(-33.7, 11) * mm, "end": v(-33.7, 7) * mm});
            skLineSegment(sketch, "E20.0.9.0", {"start": v(-37.7, 5) * mm, "end": v(-33.7, 5) * mm});
            skLineSegment(sketch, "E20.0.9.1", {"start": v(-37.7, 5) * mm, "end": v(-37.7, 1) * mm});
            skLineSegment(sketch, "E20.0.9.2", {"start": v(-37.7, 1) * mm, "end": v(-33.7, 1) * mm});
            skLineSegment(sketch, "E20.0.9.3", {"start": v(-33.7, 5) * mm, "end": v(-33.7, 1) * mm});
            skLineSegment(sketch, "E20.0.10.0", {"start": v(-37.7, -1) * mm, "end": v(-33.7, -1) * mm});
            skLineSegment(sketch, "E20.0.10.1", {"start": v(-37.7, -1) * mm, "end": v(-37.7, -5) * mm});
            skLineSegment(sketch, "E20.0.10.2", {"start": v(-37.7, -5) * mm, "end": v(-33.7, -5) * mm});
            skLineSegment(sketch, "E20.0.10.3", {"start": v(-33.7, -1) * mm, "end": v(-33.7, -5) * mm});
            skLineSegment(sketch, "E20.0.11.0", {"start": v(-37.7, -7) * mm, "end": v(-33.7, -7) * mm});
            skLineSegment(sketch, "E20.0.11.1", {"start": v(-37.7, -7) * mm, "end": v(-37.7, -11) * mm});
            skLineSegment(sketch, "E20.0.11.2", {"start": v(-37.7, -11) * mm, "end": v(-33.7, -11) * mm});
            skLineSegment(sketch, "E20.0.11.3", {"start": v(-33.7, -7) * mm, "end": v(-33.7, -11) * mm});
            skLineSegment(sketch, "E20.0.12.0", {"start": v(-37.7, -13) * mm, "end": v(-33.7, -13) * mm});
            skLineSegment(sketch, "E20.0.12.1", {"start": v(-37.7, -13) * mm, "end": v(-37.7, -17) * mm});
            skLineSegment(sketch, "E20.0.12.2", {"start": v(-37.7, -17) * mm, "end": v(-33.7, -17) * mm});
            skLineSegment(sketch, "E20.0.12.3", {"start": v(-33.7, -13) * mm, "end": v(-33.7, -17) * mm});
            skLineSegment(sketch, "E20.0.13.0", {"start": v(-37.7, -19) * mm, "end": v(-33.7, -19) * mm});
            skLineSegment(sketch, "E20.0.13.1", {"start": v(-37.7, -19) * mm, "end": v(-37.7, -23) * mm});
            skLineSegment(sketch, "E20.0.13.2", {"start": v(-37.7, -23) * mm, "end": v(-33.7, -23) * mm});
            skLineSegment(sketch, "E20.0.13.3", {"start": v(-33.7, -19) * mm, "end": v(-33.7, -23) * mm});
            skLineSegment(sketch, "E20.0.14.0", {"start": v(-37.7, -25) * mm, "end": v(-33.7, -25) * mm});
            skLineSegment(sketch, "E20.0.14.1", {"start": v(-37.7, -25) * mm, "end": v(-37.7, -29) * mm});
            skLineSegment(sketch, "E20.0.14.2", {"start": v(-37.7, -29) * mm, "end": v(-33.7, -29) * mm});
            skLineSegment(sketch, "E20.0.14.3", {"start": v(-33.7, -25) * mm, "end": v(-33.7, -29) * mm});
            skLineSegment(sketch, "E20.1.0.0", {"start": v(-31.7, 59) * mm, "end": v(-27.7, 59) * mm});
            skLineSegment(sketch, "E20.1.0.1", {"start": v(-31.7, 59) * mm, "end": v(-31.7, 55) * mm});
            skLineSegment(sketch, "E20.1.0.2", {"start": v(-31.7, 55) * mm, "end": v(-27.7, 55) * mm});
            skLineSegment(sketch, "E20.1.0.3", {"start": v(-27.7, 59) * mm, "end": v(-27.7, 55) * mm});
            skLineSegment(sketch, "E20.1.1.0", {"start": v(-31.7, 53) * mm, "end": v(-27.7, 53) * mm});
            skLineSegment(sketch, "E20.1.1.1", {"start": v(-31.7, 53) * mm, "end": v(-31.7, 49) * mm});
            skLineSegment(sketch, "E20.1.1.2", {"start": v(-31.7, 49) * mm, "end": v(-27.7, 49) * mm});
            skLineSegment(sketch, "E20.1.1.3", {"start": v(-27.7, 53) * mm, "end": v(-27.7, 49) * mm});
            skLineSegment(sketch, "E20.1.2.0", {"start": v(-31.7, 47) * mm, "end": v(-27.7, 47) * mm});
            skLineSegment(sketch, "E20.1.2.1", {"start": v(-31.7, 47) * mm, "end": v(-31.7, 43) * mm});
            skLineSegment(sketch, "E20.1.2.2", {"start": v(-31.7, 43) * mm, "end": v(-27.7, 43) * mm});
            skLineSegment(sketch, "E20.1.2.3", {"start": v(-27.7, 47) * mm, "end": v(-27.7, 43) * mm});
            skLineSegment(sketch, "E20.1.3.0", {"start": v(-31.7, 41) * mm, "end": v(-27.7, 41) * mm});
            skLineSegment(sketch, "E20.1.3.1", {"start": v(-31.7, 41) * mm, "end": v(-31.7, 37) * mm});
            skLineSegment(sketch, "E20.1.3.2", {"start": v(-31.7, 37) * mm, "end": v(-27.7, 37) * mm});
            skLineSegment(sketch, "E20.1.3.3", {"start": v(-27.7, 41) * mm, "end": v(-27.7, 37) * mm});
            skLineSegment(sketch, "E20.1.4.0", {"start": v(-31.7, 35) * mm, "end": v(-27.7, 35) * mm});
            skLineSegment(sketch, "E20.1.4.1", {"start": v(-31.7, 35) * mm, "end": v(-31.7, 31) * mm});
            skLineSegment(sketch, "E20.1.4.2", {"start": v(-31.7, 31) * mm, "end": v(-27.7, 31) * mm});
            skLineSegment(sketch, "E20.1.4.3", {"start": v(-27.7, 35) * mm, "end": v(-27.7, 31) * mm});
            skLineSegment(sketch, "E20.1.5.0", {"start": v(-31.7, 29) * mm, "end": v(-27.7, 29) * mm});
            skLineSegment(sketch, "E20.1.5.1", {"start": v(-31.7, 29) * mm, "end": v(-31.7, 25) * mm});
            skLineSegment(sketch, "E20.1.5.2", {"start": v(-31.7, 25) * mm, "end": v(-27.7, 25) * mm});
            skLineSegment(sketch, "E20.1.5.3", {"start": v(-27.7, 29) * mm, "end": v(-27.7, 25) * mm});
            skLineSegment(sketch, "E20.1.6.0", {"start": v(-31.7, 23) * mm, "end": v(-27.7, 23) * mm});
            skLineSegment(sketch, "E20.1.6.1", {"start": v(-31.7, 23) * mm, "end": v(-31.7, 19) * mm});
            skLineSegment(sketch, "E20.1.6.2", {"start": v(-31.7, 19) * mm, "end": v(-27.7, 19) * mm});
            skLineSegment(sketch, "E20.1.6.3", {"start": v(-27.7, 23) * mm, "end": v(-27.7, 19) * mm});
            skLineSegment(sketch, "E20.1.7.0", {"start": v(-31.7, 17) * mm, "end": v(-27.7, 17) * mm});
            skLineSegment(sketch, "E20.1.7.1", {"start": v(-31.7, 17) * mm, "end": v(-31.7, 13) * mm});
            skLineSegment(sketch, "E20.1.7.2", {"start": v(-31.7, 13) * mm, "end": v(-27.7, 13) * mm});
            skLineSegment(sketch, "E20.1.7.3", {"start": v(-27.7, 17) * mm, "end": v(-27.7, 13) * mm});
            skLineSegment(sketch, "E20.1.8.0", {"start": v(-31.7, 11) * mm, "end": v(-27.7, 11) * mm});
            skLineSegment(sketch, "E20.1.8.1", {"start": v(-31.7, 11) * mm, "end": v(-31.7, 7) * mm});
            skLineSegment(sketch, "E20.1.8.2", {"start": v(-31.7, 7) * mm, "end": v(-27.7, 7) * mm});
            skLineSegment(sketch, "E20.1.8.3", {"start": v(-27.7, 11) * mm, "end": v(-27.7, 7) * mm});
            skLineSegment(sketch, "E20.1.9.0", {"start": v(-31.7, 5) * mm, "end": v(-27.7, 5) * mm});
            skLineSegment(sketch, "E20.1.9.1", {"start": v(-31.7, 5) * mm, "end": v(-31.7, 1) * mm});
            skLineSegment(sketch, "E20.1.9.2", {"start": v(-31.7, 1) * mm, "end": v(-27.7, 1) * mm});
            skLineSegment(sketch, "E20.1.9.3", {"start": v(-27.7, 5) * mm, "end": v(-27.7, 1) * mm});
            skLineSegment(sketch, "E20.1.10.0", {"start": v(-31.7, -1) * mm, "end": v(-27.7, -1) * mm});
            skLineSegment(sketch, "E20.1.10.1", {"start": v(-31.7, -1) * mm, "end": v(-31.7, -5) * mm});
            skLineSegment(sketch, "E20.1.10.2", {"start": v(-31.7, -5) * mm, "end": v(-27.7, -5) * mm});
            skLineSegment(sketch, "E20.1.10.3", {"start": v(-27.7, -1) * mm, "end": v(-27.7, -5) * mm});
            skLineSegment(sketch, "E20.1.11.0", {"start": v(-31.7, -7) * mm, "end": v(-27.7, -7) * mm});
            skLineSegment(sketch, "E20.1.11.1", {"start": v(-31.7, -7) * mm, "end": v(-31.7, -11) * mm});
            skLineSegment(sketch, "E20.1.11.2", {"start": v(-31.7, -11) * mm, "end": v(-27.7, -11) * mm});
            skLineSegment(sketch, "E20.1.11.3", {"start": v(-27.7, -7) * mm, "end": v(-27.7, -11) * mm});
            skLineSegment(sketch, "E20.1.12.0", {"start": v(-31.7, -13) * mm, "end": v(-27.7, -13) * mm});
            skLineSegment(sketch, "E20.1.12.1", {"start": v(-31.7, -13) * mm, "end": v(-31.7, -17) * mm});
            skLineSegment(sketch, "E20.1.12.2", {"start": v(-31.7, -17) * mm, "end": v(-27.7, -17) * mm});
            skLineSegment(sketch, "E20.1.12.3", {"start": v(-27.7, -13) * mm, "end": v(-27.7, -17) * mm});
            skLineSegment(sketch, "E20.1.13.0", {"start": v(-31.7, -19) * mm, "end": v(-27.7, -19) * mm});
            skLineSegment(sketch, "E20.1.13.1", {"start": v(-31.7, -19) * mm, "end": v(-31.7, -23) * mm});
            skLineSegment(sketch, "E20.1.13.2", {"start": v(-31.7, -23) * mm, "end": v(-27.7, -23) * mm});
            skLineSegment(sketch, "E20.1.13.3", {"start": v(-27.7, -19) * mm, "end": v(-27.7, -23) * mm});
            skLineSegment(sketch, "E20.1.14.0", {"start": v(-31.7, -25) * mm, "end": v(-27.7, -25) * mm});
            skLineSegment(sketch, "E20.1.14.1", {"start": v(-31.7, -25) * mm, "end": v(-31.7, -29) * mm});
            skLineSegment(sketch, "E20.1.14.2", {"start": v(-31.7, -29) * mm, "end": v(-27.7, -29) * mm});
            skLineSegment(sketch, "E20.1.14.3", {"start": v(-27.7, -25) * mm, "end": v(-27.7, -29) * mm});
            skLineSegment(sketch, "E20.2.0.0", {"start": v(-25.7, 59) * mm, "end": v(-21.7, 59) * mm});
            skLineSegment(sketch, "E20.2.0.1", {"start": v(-25.7, 59) * mm, "end": v(-25.7, 55) * mm});
            skLineSegment(sketch, "E20.2.0.2", {"start": v(-25.7, 55) * mm, "end": v(-21.7, 55) * mm});
            skLineSegment(sketch, "E20.2.0.3", {"start": v(-21.7, 59) * mm, "end": v(-21.7, 55) * mm});
            skLineSegment(sketch, "E20.2.1.0", {"start": v(-25.7, 53) * mm, "end": v(-21.7, 53) * mm});
            skLineSegment(sketch, "E20.2.1.1", {"start": v(-25.7, 53) * mm, "end": v(-25.7, 49) * mm});
            skLineSegment(sketch, "E20.2.1.2", {"start": v(-25.7, 49) * mm, "end": v(-21.7, 49) * mm});
            skLineSegment(sketch, "E20.2.1.3", {"start": v(-21.7, 53) * mm, "end": v(-21.7, 49) * mm});
            skLineSegment(sketch, "E20.2.2.0", {"start": v(-25.7, 47) * mm, "end": v(-21.7, 47) * mm});
            skLineSegment(sketch, "E20.2.2.1", {"start": v(-25.7, 47) * mm, "end": v(-25.7, 43) * mm});
            skLineSegment(sketch, "E20.2.2.2", {"start": v(-25.7, 43) * mm, "end": v(-21.7, 43) * mm});
            skLineSegment(sketch, "E20.2.2.3", {"start": v(-21.7, 47) * mm, "end": v(-21.7, 43) * mm});
            skLineSegment(sketch, "E20.2.3.0", {"start": v(-25.7, 41) * mm, "end": v(-21.7, 41) * mm});
            skLineSegment(sketch, "E20.2.3.1", {"start": v(-25.7, 41) * mm, "end": v(-25.7, 37) * mm});
            skLineSegment(sketch, "E20.2.3.2", {"start": v(-25.7, 37) * mm, "end": v(-21.7, 37) * mm});
            skLineSegment(sketch, "E20.2.3.3", {"start": v(-21.7, 41) * mm, "end": v(-21.7, 37) * mm});
            skLineSegment(sketch, "E20.2.4.0", {"start": v(-25.7, 35) * mm, "end": v(-21.7, 35) * mm});
            skLineSegment(sketch, "E20.2.4.1", {"start": v(-25.7, 35) * mm, "end": v(-25.7, 31) * mm});
            skLineSegment(sketch, "E20.2.4.2", {"start": v(-25.7, 31) * mm, "end": v(-21.7, 31) * mm});
            skLineSegment(sketch, "E20.2.4.3", {"start": v(-21.7, 35) * mm, "end": v(-21.7, 31) * mm});
            skLineSegment(sketch, "E20.2.5.0", {"start": v(-25.7, 29) * mm, "end": v(-21.7, 29) * mm});
            skLineSegment(sketch, "E20.2.5.1", {"start": v(-25.7, 29) * mm, "end": v(-25.7, 25) * mm});
            skLineSegment(sketch, "E20.2.5.2", {"start": v(-25.7, 25) * mm, "end": v(-21.7, 25) * mm});
            skLineSegment(sketch, "E20.2.5.3", {"start": v(-21.7, 29) * mm, "end": v(-21.7, 25) * mm});
            skLineSegment(sketch, "E20.2.6.0", {"start": v(-25.7, 23) * mm, "end": v(-21.7, 23) * mm});
            skLineSegment(sketch, "E20.2.6.1", {"start": v(-25.7, 23) * mm, "end": v(-25.7, 19) * mm});
            skLineSegment(sketch, "E20.2.6.2", {"start": v(-25.7, 19) * mm, "end": v(-21.7, 19) * mm});
            skLineSegment(sketch, "E20.2.6.3", {"start": v(-21.7, 23) * mm, "end": v(-21.7, 19) * mm});
            skLineSegment(sketch, "E20.2.7.0", {"start": v(-25.7, 17) * mm, "end": v(-21.7, 17) * mm});
            skLineSegment(sketch, "E20.2.7.1", {"start": v(-25.7, 17) * mm, "end": v(-25.7, 13) * mm});
            skLineSegment(sketch, "E20.2.7.2", {"start": v(-25.7, 13) * mm, "end": v(-21.7, 13) * mm});
            skLineSegment(sketch, "E20.2.7.3", {"start": v(-21.7, 17) * mm, "end": v(-21.7, 13) * mm});
            skLineSegment(sketch, "E20.2.8.0", {"start": v(-25.7, 11) * mm, "end": v(-21.7, 11) * mm});
            skLineSegment(sketch, "E20.2.8.1", {"start": v(-25.7, 11) * mm, "end": v(-25.7, 7) * mm});
            skLineSegment(sketch, "E20.2.8.2", {"start": v(-25.7, 7) * mm, "end": v(-21.7, 7) * mm});
            skLineSegment(sketch, "E20.2.8.3", {"start": v(-21.7, 11) * mm, "end": v(-21.7, 7) * mm});
            skLineSegment(sketch, "E20.2.9.0", {"start": v(-25.7, 5) * mm, "end": v(-21.7, 5) * mm});
            skLineSegment(sketch, "E20.2.9.1", {"start": v(-25.7, 5) * mm, "end": v(-25.7, 1) * mm});
            skLineSegment(sketch, "E20.2.9.2", {"start": v(-25.7, 1) * mm, "end": v(-21.7, 1) * mm});
            skLineSegment(sketch, "E20.2.9.3", {"start": v(-21.7, 5) * mm, "end": v(-21.7, 1) * mm});
            skLineSegment(sketch, "E20.2.10.0", {"start": v(-25.7, -1) * mm, "end": v(-21.7, -1) * mm});
            skLineSegment(sketch, "E20.2.10.1", {"start": v(-25.7, -1) * mm, "end": v(-25.7, -5) * mm});
            skLineSegment(sketch, "E20.2.10.2", {"start": v(-25.7, -5) * mm, "end": v(-21.7, -5) * mm});
            skLineSegment(sketch, "E20.2.10.3", {"start": v(-21.7, -1) * mm, "end": v(-21.7, -5) * mm});
            skLineSegment(sketch, "E20.2.11.0", {"start": v(-25.7, -7) * mm, "end": v(-21.7, -7) * mm});
            skLineSegment(sketch, "E20.2.11.1", {"start": v(-25.7, -7) * mm, "end": v(-25.7, -11) * mm});
            skLineSegment(sketch, "E20.2.11.2", {"start": v(-25.7, -11) * mm, "end": v(-21.7, -11) * mm});
            skLineSegment(sketch, "E20.2.11.3", {"start": v(-21.7, -7) * mm, "end": v(-21.7, -11) * mm});
            skLineSegment(sketch, "E20.2.12.0", {"start": v(-25.7, -13) * mm, "end": v(-21.7, -13) * mm});
            skLineSegment(sketch, "E20.2.12.1", {"start": v(-25.7, -13) * mm, "end": v(-25.7, -17) * mm});
            skLineSegment(sketch, "E20.2.12.2", {"start": v(-25.7, -17) * mm, "end": v(-21.7, -17) * mm});
            skLineSegment(sketch, "E20.2.12.3", {"start": v(-21.7, -13) * mm, "end": v(-21.7, -17) * mm});
            skLineSegment(sketch, "E20.2.13.0", {"start": v(-25.7, -19) * mm, "end": v(-21.7, -19) * mm});
            skLineSegment(sketch, "E20.2.13.1", {"start": v(-25.7, -19) * mm, "end": v(-25.7, -23) * mm});
            skLineSegment(sketch, "E20.2.13.2", {"start": v(-25.7, -23) * mm, "end": v(-21.7, -23) * mm});
            skLineSegment(sketch, "E20.2.13.3", {"start": v(-21.7, -19) * mm, "end": v(-21.7, -23) * mm});
            skLineSegment(sketch, "E20.2.14.0", {"start": v(-25.7, -25) * mm, "end": v(-21.7, -25) * mm});
            skLineSegment(sketch, "E20.2.14.1", {"start": v(-25.7, -25) * mm, "end": v(-25.7, -29) * mm});
            skLineSegment(sketch, "E20.2.14.2", {"start": v(-25.7, -29) * mm, "end": v(-21.7, -29) * mm});
            skLineSegment(sketch, "E20.2.14.3", {"start": v(-21.7, -25) * mm, "end": v(-21.7, -29) * mm});
            skLineSegment(sketch, "E20.3.0.0", {"start": v(-19.7, 59) * mm, "end": v(-15.7, 59) * mm});
            skLineSegment(sketch, "E20.3.0.1", {"start": v(-19.7, 59) * mm, "end": v(-19.7, 55) * mm});
            skLineSegment(sketch, "E20.3.0.2", {"start": v(-19.7, 55) * mm, "end": v(-15.7, 55) * mm});
            skLineSegment(sketch, "E20.3.0.3", {"start": v(-15.7, 59) * mm, "end": v(-15.7, 55) * mm});
            skLineSegment(sketch, "E20.3.1.0", {"start": v(-19.7, 53) * mm, "end": v(-15.7, 53) * mm});
            skLineSegment(sketch, "E20.3.1.1", {"start": v(-19.7, 53) * mm, "end": v(-19.7, 49) * mm});
            skLineSegment(sketch, "E20.3.1.2", {"start": v(-19.7, 49) * mm, "end": v(-15.7, 49) * mm});
            skLineSegment(sketch, "E20.3.1.3", {"start": v(-15.7, 53) * mm, "end": v(-15.7, 49) * mm});
            skLineSegment(sketch, "E20.3.2.0", {"start": v(-19.7, 47) * mm, "end": v(-15.7, 47) * mm});
            skLineSegment(sketch, "E20.3.2.1", {"start": v(-19.7, 47) * mm, "end": v(-19.7, 43) * mm});
            skLineSegment(sketch, "E20.3.2.2", {"start": v(-19.7, 43) * mm, "end": v(-15.7, 43) * mm});
            skLineSegment(sketch, "E20.3.2.3", {"start": v(-15.7, 47) * mm, "end": v(-15.7, 43) * mm});
            skLineSegment(sketch, "E20.3.3.0", {"start": v(-19.7, 41) * mm, "end": v(-15.7, 41) * mm});
            skLineSegment(sketch, "E20.3.3.1", {"start": v(-19.7, 41) * mm, "end": v(-19.7, 37) * mm});
            skLineSegment(sketch, "E20.3.3.2", {"start": v(-19.7, 37) * mm, "end": v(-15.7, 37) * mm});
            skLineSegment(sketch, "E20.3.3.3", {"start": v(-15.7, 41) * mm, "end": v(-15.7, 37) * mm});
            skLineSegment(sketch, "E20.3.4.0", {"start": v(-19.7, 35) * mm, "end": v(-15.7, 35) * mm});
            skLineSegment(sketch, "E20.3.4.1", {"start": v(-19.7, 35) * mm, "end": v(-19.7, 31) * mm});
            skLineSegment(sketch, "E20.3.4.2", {"start": v(-19.7, 31) * mm, "end": v(-15.7, 31) * mm});
            skLineSegment(sketch, "E20.3.4.3", {"start": v(-15.7, 35) * mm, "end": v(-15.7, 31) * mm});
            skLineSegment(sketch, "E20.3.5.0", {"start": v(-19.7, 29) * mm, "end": v(-15.7, 29) * mm});
            skLineSegment(sketch, "E20.3.5.1", {"start": v(-19.7, 29) * mm, "end": v(-19.7, 25) * mm});
            skLineSegment(sketch, "E20.3.5.2", {"start": v(-19.7, 25) * mm, "end": v(-15.7, 25) * mm});
            skLineSegment(sketch, "E20.3.5.3", {"start": v(-15.7, 29) * mm, "end": v(-15.7, 25) * mm});
            skLineSegment(sketch, "E20.3.6.0", {"start": v(-19.7, 23) * mm, "end": v(-15.7, 23) * mm});
            skLineSegment(sketch, "E20.3.6.1", {"start": v(-19.7, 23) * mm, "end": v(-19.7, 19) * mm});
            skLineSegment(sketch, "E20.3.6.2", {"start": v(-19.7, 19) * mm, "end": v(-15.7, 19) * mm});
            skLineSegment(sketch, "E20.3.6.3", {"start": v(-15.7, 23) * mm, "end": v(-15.7, 19) * mm});
            skLineSegment(sketch, "E20.3.7.0", {"start": v(-19.7, 17) * mm, "end": v(-15.7, 17) * mm});
            skLineSegment(sketch, "E20.3.7.1", {"start": v(-19.7, 17) * mm, "end": v(-19.7, 13) * mm});
            skLineSegment(sketch, "E20.3.7.2", {"start": v(-19.7, 13) * mm, "end": v(-15.7, 13) * mm});
            skLineSegment(sketch, "E20.3.7.3", {"start": v(-15.7, 17) * mm, "end": v(-15.7, 13) * mm});
            skLineSegment(sketch, "E20.3.8.0", {"start": v(-19.7, 11) * mm, "end": v(-15.7, 11) * mm});
            skLineSegment(sketch, "E20.3.8.1", {"start": v(-19.7, 11) * mm, "end": v(-19.7, 7) * mm});
            skLineSegment(sketch, "E20.3.8.2", {"start": v(-19.7, 7) * mm, "end": v(-15.7, 7) * mm});
            skLineSegment(sketch, "E20.3.8.3", {"start": v(-15.7, 11) * mm, "end": v(-15.7, 7) * mm});
            skLineSegment(sketch, "E20.3.9.0", {"start": v(-19.7, 5) * mm, "end": v(-15.7, 5) * mm});
            skLineSegment(sketch, "E20.3.9.1", {"start": v(-19.7, 5) * mm, "end": v(-19.7, 1) * mm});
            skLineSegment(sketch, "E20.3.9.2", {"start": v(-19.7, 1) * mm, "end": v(-15.7, 1) * mm});
            skLineSegment(sketch, "E20.3.9.3", {"start": v(-15.7, 5) * mm, "end": v(-15.7, 1) * mm});
            skLineSegment(sketch, "E20.3.10.0", {"start": v(-19.7, -1) * mm, "end": v(-15.7, -1) * mm});
            skLineSegment(sketch, "E20.3.10.1", {"start": v(-19.7, -1) * mm, "end": v(-19.7, -5) * mm});
            skLineSegment(sketch, "E20.3.10.2", {"start": v(-19.7, -5) * mm, "end": v(-15.7, -5) * mm});
            skLineSegment(sketch, "E20.3.10.3", {"start": v(-15.7, -1) * mm, "end": v(-15.7, -5) * mm});
            skLineSegment(sketch, "E20.3.11.0", {"start": v(-19.7, -7) * mm, "end": v(-15.7, -7) * mm});
            skLineSegment(sketch, "E20.3.11.1", {"start": v(-19.7, -7) * mm, "end": v(-19.7, -11) * mm});
            skLineSegment(sketch, "E20.3.11.2", {"start": v(-19.7, -11) * mm, "end": v(-15.7, -11) * mm});
            skLineSegment(sketch, "E20.3.11.3", {"start": v(-15.7, -7) * mm, "end": v(-15.7, -11) * mm});
            skLineSegment(sketch, "E20.3.12.0", {"start": v(-19.7, -13) * mm, "end": v(-15.7, -13) * mm});
            skLineSegment(sketch, "E20.3.12.1", {"start": v(-19.7, -13) * mm, "end": v(-19.7, -17) * mm});
            skLineSegment(sketch, "E20.3.12.2", {"start": v(-19.7, -17) * mm, "end": v(-15.7, -17) * mm});
            skLineSegment(sketch, "E20.3.12.3", {"start": v(-15.7, -13) * mm, "end": v(-15.7, -17) * mm});
            skLineSegment(sketch, "E20.3.13.0", {"start": v(-19.7, -19) * mm, "end": v(-15.7, -19) * mm});
            skLineSegment(sketch, "E20.3.13.1", {"start": v(-19.7, -19) * mm, "end": v(-19.7, -23) * mm});
            skLineSegment(sketch, "E20.3.13.2", {"start": v(-19.7, -23) * mm, "end": v(-15.7, -23) * mm});
            skLineSegment(sketch, "E20.3.13.3", {"start": v(-15.7, -19) * mm, "end": v(-15.7, -23) * mm});
            skLineSegment(sketch, "E20.3.14.0", {"start": v(-19.7, -25) * mm, "end": v(-15.7, -25) * mm});
            skLineSegment(sketch, "E20.3.14.1", {"start": v(-19.7, -25) * mm, "end": v(-19.7, -29) * mm});
            skLineSegment(sketch, "E20.3.14.2", {"start": v(-19.7, -29) * mm, "end": v(-15.7, -29) * mm});
            skLineSegment(sketch, "E20.3.14.3", {"start": v(-15.7, -25) * mm, "end": v(-15.7, -29) * mm});
            skLineSegment(sketch, "E20.4.0.0", {"start": v(-13.7, 59) * mm, "end": v(-9.7, 59) * mm});
            skLineSegment(sketch, "E20.4.0.1", {"start": v(-13.7, 59) * mm, "end": v(-13.7, 55) * mm});
            skLineSegment(sketch, "E20.4.0.2", {"start": v(-13.7, 55) * mm, "end": v(-9.7, 55) * mm});
            skLineSegment(sketch, "E20.4.0.3", {"start": v(-9.7, 59) * mm, "end": v(-9.7, 55) * mm});
            skLineSegment(sketch, "E20.4.1.0", {"start": v(-13.7, 53) * mm, "end": v(-9.7, 53) * mm});
            skLineSegment(sketch, "E20.4.1.1", {"start": v(-13.7, 53) * mm, "end": v(-13.7, 49) * mm});
            skLineSegment(sketch, "E20.4.1.2", {"start": v(-13.7, 49) * mm, "end": v(-9.7, 49) * mm});
            skLineSegment(sketch, "E20.4.1.3", {"start": v(-9.7, 53) * mm, "end": v(-9.7, 49) * mm});
            skLineSegment(sketch, "E20.4.2.0", {"start": v(-13.7, 47) * mm, "end": v(-9.7, 47) * mm});
            skLineSegment(sketch, "E20.4.2.1", {"start": v(-13.7, 47) * mm, "end": v(-13.7, 43) * mm});
            skLineSegment(sketch, "E20.4.2.2", {"start": v(-13.7, 43) * mm, "end": v(-9.7, 43) * mm});
            skLineSegment(sketch, "E20.4.2.3", {"start": v(-9.7, 47) * mm, "end": v(-9.7, 43) * mm});
            skLineSegment(sketch, "E20.4.3.0", {"start": v(-13.7, 41) * mm, "end": v(-9.7, 41) * mm});
            skLineSegment(sketch, "E20.4.3.1", {"start": v(-13.7, 41) * mm, "end": v(-13.7, 37) * mm});
            skLineSegment(sketch, "E20.4.3.2", {"start": v(-13.7, 37) * mm, "end": v(-9.7, 37) * mm});
            skLineSegment(sketch, "E20.4.3.3", {"start": v(-9.7, 41) * mm, "end": v(-9.7, 37) * mm});
            skLineSegment(sketch, "E20.4.4.0", {"start": v(-13.7, 35) * mm, "end": v(-9.7, 35) * mm});
            skLineSegment(sketch, "E20.4.4.1", {"start": v(-13.7, 35) * mm, "end": v(-13.7, 31) * mm});
            skLineSegment(sketch, "E20.4.4.2", {"start": v(-13.7, 31) * mm, "end": v(-9.7, 31) * mm});
            skLineSegment(sketch, "E20.4.4.3", {"start": v(-9.7, 35) * mm, "end": v(-9.7, 31) * mm});
            skLineSegment(sketch, "E20.4.5.0", {"start": v(-13.7, 29) * mm, "end": v(-9.7, 29) * mm});
            skLineSegment(sketch, "E20.4.5.1", {"start": v(-13.7, 29) * mm, "end": v(-13.7, 25) * mm});
            skLineSegment(sketch, "E20.4.5.2", {"start": v(-13.7, 25) * mm, "end": v(-9.7, 25) * mm});
            skLineSegment(sketch, "E20.4.5.3", {"start": v(-9.7, 29) * mm, "end": v(-9.7, 25) * mm});
            skLineSegment(sketch, "E20.4.6.0", {"start": v(-13.7, 23) * mm, "end": v(-9.7, 23) * mm});
            skLineSegment(sketch, "E20.4.6.1", {"start": v(-13.7, 23) * mm, "end": v(-13.7, 19) * mm});
            skLineSegment(sketch, "E20.4.6.2", {"start": v(-13.7, 19) * mm, "end": v(-9.7, 19) * mm});
            skLineSegment(sketch, "E20.4.6.3", {"start": v(-9.7, 23) * mm, "end": v(-9.7, 19) * mm});
            skLineSegment(sketch, "E20.4.7.0", {"start": v(-13.7, 17) * mm, "end": v(-9.7, 17) * mm});
            skLineSegment(sketch, "E20.4.7.1", {"start": v(-13.7, 17) * mm, "end": v(-13.7, 13) * mm});
            skLineSegment(sketch, "E20.4.7.2", {"start": v(-13.7, 13) * mm, "end": v(-9.7, 13) * mm});
            skLineSegment(sketch, "E20.4.7.3", {"start": v(-9.7, 17) * mm, "end": v(-9.7, 13) * mm});
            skLineSegment(sketch, "E20.4.8.0", {"start": v(-13.7, 11) * mm, "end": v(-9.7, 11) * mm});
            skLineSegment(sketch, "E20.4.8.1", {"start": v(-13.7, 11) * mm, "end": v(-13.7, 7) * mm});
            skLineSegment(sketch, "E20.4.8.2", {"start": v(-13.7, 7) * mm, "end": v(-9.7, 7) * mm});
            skLineSegment(sketch, "E20.4.8.3", {"start": v(-9.7, 11) * mm, "end": v(-9.7, 7) * mm});
            skLineSegment(sketch, "E20.4.9.0", {"start": v(-13.7, 5) * mm, "end": v(-9.7, 5) * mm});
            skLineSegment(sketch, "E20.4.9.1", {"start": v(-13.7, 5) * mm, "end": v(-13.7, 1) * mm});
            skLineSegment(sketch, "E20.4.9.2", {"start": v(-13.7, 1) * mm, "end": v(-9.7, 1) * mm});
            skLineSegment(sketch, "E20.4.9.3", {"start": v(-9.7, 5) * mm, "end": v(-9.7, 1) * mm});
            skLineSegment(sketch, "E20.4.10.0", {"start": v(-13.7, -1) * mm, "end": v(-9.7, -1) * mm});
            skLineSegment(sketch, "E20.4.10.1", {"start": v(-13.7, -1) * mm, "end": v(-13.7, -5) * mm});
            skLineSegment(sketch, "E20.4.10.2", {"start": v(-13.7, -5) * mm, "end": v(-9.7, -5) * mm});
            skLineSegment(sketch, "E20.4.10.3", {"start": v(-9.7, -1) * mm, "end": v(-9.7, -5) * mm});
            skLineSegment(sketch, "E20.4.11.0", {"start": v(-13.7, -7) * mm, "end": v(-9.7, -7) * mm});
            skLineSegment(sketch, "E20.4.11.1", {"start": v(-13.7, -7) * mm, "end": v(-13.7, -11) * mm});
            skLineSegment(sketch, "E20.4.11.2", {"start": v(-13.7, -11) * mm, "end": v(-9.7, -11) * mm});
            skLineSegment(sketch, "E20.4.11.3", {"start": v(-9.7, -7) * mm, "end": v(-9.7, -11) * mm});
            skLineSegment(sketch, "E20.4.12.0", {"start": v(-13.7, -13) * mm, "end": v(-9.7, -13) * mm});
            skLineSegment(sketch, "E20.4.12.1", {"start": v(-13.7, -13) * mm, "end": v(-13.7, -17) * mm});
            skLineSegment(sketch, "E20.4.12.2", {"start": v(-13.7, -17) * mm, "end": v(-9.7, -17) * mm});
            skLineSegment(sketch, "E20.4.12.3", {"start": v(-9.7, -13) * mm, "end": v(-9.7, -17) * mm});
            skLineSegment(sketch, "E20.4.13.0", {"start": v(-13.7, -19) * mm, "end": v(-9.7, -19) * mm});
            skLineSegment(sketch, "E20.4.13.1", {"start": v(-13.7, -19) * mm, "end": v(-13.7, -23) * mm});
            skLineSegment(sketch, "E20.4.13.2", {"start": v(-13.7, -23) * mm, "end": v(-9.7, -23) * mm});
            skLineSegment(sketch, "E20.4.13.3", {"start": v(-9.7, -19) * mm, "end": v(-9.7, -23) * mm});
            skLineSegment(sketch, "E20.4.14.0", {"start": v(-13.7, -25) * mm, "end": v(-9.7, -25) * mm});
            skLineSegment(sketch, "E20.4.14.1", {"start": v(-13.7, -25) * mm, "end": v(-13.7, -29) * mm});
            skLineSegment(sketch, "E20.4.14.2", {"start": v(-13.7, -29) * mm, "end": v(-9.7, -29) * mm});
            skLineSegment(sketch, "E20.4.14.3", {"start": v(-9.7, -25) * mm, "end": v(-9.7, -29) * mm});
            skLineSegment(sketch, "E20.5.0.0", {"start": v(-7.7, 59) * mm, "end": v(-3.7, 59) * mm});
            skLineSegment(sketch, "E20.5.0.1", {"start": v(-7.7, 59) * mm, "end": v(-7.7, 55) * mm});
            skLineSegment(sketch, "E20.5.0.2", {"start": v(-7.7, 55) * mm, "end": v(-3.7, 55) * mm});
            skLineSegment(sketch, "E20.5.0.3", {"start": v(-3.7, 59) * mm, "end": v(-3.7, 55) * mm});
            skLineSegment(sketch, "E20.5.1.0", {"start": v(-7.7, 53) * mm, "end": v(-3.7, 53) * mm});
            skLineSegment(sketch, "E20.5.1.1", {"start": v(-7.7, 53) * mm, "end": v(-7.7, 49) * mm});
            skLineSegment(sketch, "E20.5.1.2", {"start": v(-7.7, 49) * mm, "end": v(-3.7, 49) * mm});
            skLineSegment(sketch, "E20.5.1.3", {"start": v(-3.7, 53) * mm, "end": v(-3.7, 49) * mm});
            skLineSegment(sketch, "E20.5.2.0", {"start": v(-7.7, 47) * mm, "end": v(-3.7, 47) * mm});
            skLineSegment(sketch, "E20.5.2.1", {"start": v(-7.7, 47) * mm, "end": v(-7.7, 43) * mm});
            skLineSegment(sketch, "E20.5.2.2", {"start": v(-7.7, 43) * mm, "end": v(-3.7, 43) * mm});
            skLineSegment(sketch, "E20.5.2.3", {"start": v(-3.7, 47) * mm, "end": v(-3.7, 43) * mm});
            skLineSegment(sketch, "E20.5.3.0", {"start": v(-7.7, 41) * mm, "end": v(-3.7, 41) * mm});
            skLineSegment(sketch, "E20.5.3.1", {"start": v(-7.7, 41) * mm, "end": v(-7.7, 37) * mm});
            skLineSegment(sketch, "E20.5.3.2", {"start": v(-7.7, 37) * mm, "end": v(-3.7, 37) * mm});
            skLineSegment(sketch, "E20.5.3.3", {"start": v(-3.7, 41) * mm, "end": v(-3.7, 37) * mm});
            skLineSegment(sketch, "E20.5.4.0", {"start": v(-7.7, 35) * mm, "end": v(-3.7, 35) * mm});
            skLineSegment(sketch, "E20.5.4.1", {"start": v(-7.7, 35) * mm, "end": v(-7.7, 31) * mm});
            skLineSegment(sketch, "E20.5.4.2", {"start": v(-7.7, 31) * mm, "end": v(-3.7, 31) * mm});
            skLineSegment(sketch, "E20.5.4.3", {"start": v(-3.7, 35) * mm, "end": v(-3.7, 31) * mm});
            skLineSegment(sketch, "E20.5.5.0", {"start": v(-7.7, 29) * mm, "end": v(-3.7, 29) * mm});
            skLineSegment(sketch, "E20.5.5.1", {"start": v(-7.7, 29) * mm, "end": v(-7.7, 25) * mm});
            skLineSegment(sketch, "E20.5.5.2", {"start": v(-7.7, 25) * mm, "end": v(-3.7, 25) * mm});
            skLineSegment(sketch, "E20.5.5.3", {"start": v(-3.7, 29) * mm, "end": v(-3.7, 25) * mm});
            skLineSegment(sketch, "E20.5.6.0", {"start": v(-7.7, 23) * mm, "end": v(-3.7, 23) * mm});
            skLineSegment(sketch, "E20.5.6.1", {"start": v(-7.7, 23) * mm, "end": v(-7.7, 19) * mm});
            skLineSegment(sketch, "E20.5.6.2", {"start": v(-7.7, 19) * mm, "end": v(-3.7, 19) * mm});
            skLineSegment(sketch, "E20.5.6.3", {"start": v(-3.7, 23) * mm, "end": v(-3.7, 19) * mm});
            skLineSegment(sketch, "E20.5.7.0", {"start": v(-7.7, 17) * mm, "end": v(-3.7, 17) * mm});
            skLineSegment(sketch, "E20.5.7.1", {"start": v(-7.7, 17) * mm, "end": v(-7.7, 13) * mm});
            skLineSegment(sketch, "E20.5.7.2", {"start": v(-7.7, 13) * mm, "end": v(-3.7, 13) * mm});
            skLineSegment(sketch, "E20.5.7.3", {"start": v(-3.7, 17) * mm, "end": v(-3.7, 13) * mm});
            skLineSegment(sketch, "E20.5.8.0", {"start": v(-7.7, 11) * mm, "end": v(-3.7, 11) * mm});
            skLineSegment(sketch, "E20.5.8.1", {"start": v(-7.7, 11) * mm, "end": v(-7.7, 7) * mm});
            skLineSegment(sketch, "E20.5.8.2", {"start": v(-7.7, 7) * mm, "end": v(-3.7, 7) * mm});
            skLineSegment(sketch, "E20.5.8.3", {"start": v(-3.7, 11) * mm, "end": v(-3.7, 7) * mm});
            skLineSegment(sketch, "E20.5.9.0", {"start": v(-7.7, 5) * mm, "end": v(-3.7, 5) * mm});
            skLineSegment(sketch, "E20.5.9.1", {"start": v(-7.7, 5) * mm, "end": v(-7.7, 1) * mm});
            skLineSegment(sketch, "E20.5.9.2", {"start": v(-7.7, 1) * mm, "end": v(-3.7, 1) * mm});
            skLineSegment(sketch, "E20.5.9.3", {"start": v(-3.7, 5) * mm, "end": v(-3.7, 1) * mm});
            skLineSegment(sketch, "E20.5.10.0", {"start": v(-7.7, -1) * mm, "end": v(-3.7, -1) * mm});
            skLineSegment(sketch, "E20.5.10.1", {"start": v(-7.7, -1) * mm, "end": v(-7.7, -5) * mm});
            skLineSegment(sketch, "E20.5.10.2", {"start": v(-7.7, -5) * mm, "end": v(-3.7, -5) * mm});
            skLineSegment(sketch, "E20.5.10.3", {"start": v(-3.7, -1) * mm, "end": v(-3.7, -5) * mm});
            skLineSegment(sketch, "E20.5.11.0", {"start": v(-7.7, -7) * mm, "end": v(-3.7, -7) * mm});
            skLineSegment(sketch, "E20.5.11.1", {"start": v(-7.7, -7) * mm, "end": v(-7.7, -11) * mm});
            skLineSegment(sketch, "E20.5.11.2", {"start": v(-7.7, -11) * mm, "end": v(-3.7, -11) * mm});
            skLineSegment(sketch, "E20.5.11.3", {"start": v(-3.7, -7) * mm, "end": v(-3.7, -11) * mm});
            skLineSegment(sketch, "E20.5.12.0", {"start": v(-7.7, -13) * mm, "end": v(-3.7, -13) * mm});
            skLineSegment(sketch, "E20.5.12.1", {"start": v(-7.7, -13) * mm, "end": v(-7.7, -17) * mm});
            skLineSegment(sketch, "E20.5.12.2", {"start": v(-7.7, -17) * mm, "end": v(-3.7, -17) * mm});
            skLineSegment(sketch, "E20.5.12.3", {"start": v(-3.7, -13) * mm, "end": v(-3.7, -17) * mm});
            skLineSegment(sketch, "E20.5.13.0", {"start": v(-7.7, -19) * mm, "end": v(-3.7, -19) * mm});
            skLineSegment(sketch, "E20.5.13.1", {"start": v(-7.7, -19) * mm, "end": v(-7.7, -23) * mm});
            skLineSegment(sketch, "E20.5.13.2", {"start": v(-7.7, -23) * mm, "end": v(-3.7, -23) * mm});
            skLineSegment(sketch, "E20.5.13.3", {"start": v(-3.7, -19) * mm, "end": v(-3.7, -23) * mm});
            skLineSegment(sketch, "E20.5.14.0", {"start": v(-7.7, -25) * mm, "end": v(-3.7, -25) * mm});
            skLineSegment(sketch, "E20.5.14.1", {"start": v(-7.7, -25) * mm, "end": v(-7.7, -29) * mm});
            skLineSegment(sketch, "E20.5.14.2", {"start": v(-7.7, -29) * mm, "end": v(-3.7, -29) * mm});
            skLineSegment(sketch, "E20.5.14.3", {"start": v(-3.7, -25) * mm, "end": v(-3.7, -29) * mm});
            skLineSegment(sketch, "E20.6.0.0", {"start": v(-1.7, 59) * mm, "end": v(2.3, 59) * mm});
            skLineSegment(sketch, "E20.6.0.1", {"start": v(-1.7, 59) * mm, "end": v(-1.7, 55) * mm});
            skLineSegment(sketch, "E20.6.0.2", {"start": v(-1.7, 55) * mm, "end": v(2.3, 55) * mm});
            skLineSegment(sketch, "E20.6.0.3", {"start": v(2.3, 59) * mm, "end": v(2.3, 55) * mm});
            skLineSegment(sketch, "E20.6.1.0", {"start": v(-1.7, 53) * mm, "end": v(2.3, 53) * mm});
            skLineSegment(sketch, "E20.6.1.1", {"start": v(-1.7, 53) * mm, "end": v(-1.7, 49) * mm});
            skLineSegment(sketch, "E20.6.1.2", {"start": v(-1.7, 49) * mm, "end": v(2.3, 49) * mm});
            skLineSegment(sketch, "E20.6.1.3", {"start": v(2.3, 53) * mm, "end": v(2.3, 49) * mm});
            skLineSegment(sketch, "E20.6.2.0", {"start": v(-1.7, 47) * mm, "end": v(2.3, 47) * mm});
            skLineSegment(sketch, "E20.6.2.1", {"start": v(-1.7, 47) * mm, "end": v(-1.7, 43) * mm});
            skLineSegment(sketch, "E20.6.2.2", {"start": v(-1.7, 43) * mm, "end": v(2.3, 43) * mm});
            skLineSegment(sketch, "E20.6.2.3", {"start": v(2.3, 47) * mm, "end": v(2.3, 43) * mm});
            skLineSegment(sketch, "E20.6.3.0", {"start": v(-1.7, 41) * mm, "end": v(2.3, 41) * mm});
            skLineSegment(sketch, "E20.6.3.1", {"start": v(-1.7, 41) * mm, "end": v(-1.7, 37) * mm});
            skLineSegment(sketch, "E20.6.3.2", {"start": v(-1.7, 37) * mm, "end": v(2.3, 37) * mm});
            skLineSegment(sketch, "E20.6.3.3", {"start": v(2.3, 41) * mm, "end": v(2.3, 37) * mm});
            skLineSegment(sketch, "E20.6.4.0", {"start": v(-1.7, 35) * mm, "end": v(2.3, 35) * mm});
            skLineSegment(sketch, "E20.6.4.1", {"start": v(-1.7, 35) * mm, "end": v(-1.7, 31) * mm});
            skLineSegment(sketch, "E20.6.4.2", {"start": v(-1.7, 31) * mm, "end": v(2.3, 31) * mm});
            skLineSegment(sketch, "E20.6.4.3", {"start": v(2.3, 35) * mm, "end": v(2.3, 31) * mm});
            skLineSegment(sketch, "E20.6.5.0", {"start": v(-1.7, 29) * mm, "end": v(2.3, 29) * mm});
            skLineSegment(sketch, "E20.6.5.1", {"start": v(-1.7, 29) * mm, "end": v(-1.7, 25) * mm});
            skLineSegment(sketch, "E20.6.5.2", {"start": v(-1.7, 25) * mm, "end": v(2.3, 25) * mm});
            skLineSegment(sketch, "E20.6.5.3", {"start": v(2.3, 29) * mm, "end": v(2.3, 25) * mm});
            skLineSegment(sketch, "E20.6.6.0", {"start": v(-1.7, 23) * mm, "end": v(2.3, 23) * mm});
            skLineSegment(sketch, "E20.6.6.1", {"start": v(-1.7, 23) * mm, "end": v(-1.7, 19) * mm});
            skLineSegment(sketch, "E20.6.6.2", {"start": v(-1.7, 19) * mm, "end": v(2.3, 19) * mm});
            skLineSegment(sketch, "E20.6.6.3", {"start": v(2.3, 23) * mm, "end": v(2.3, 19) * mm});
            skLineSegment(sketch, "E20.6.7.0", {"start": v(-1.7, 17) * mm, "end": v(2.3, 17) * mm});
            skLineSegment(sketch, "E20.6.7.1", {"start": v(-1.7, 17) * mm, "end": v(-1.7, 13) * mm});
            skLineSegment(sketch, "E20.6.7.2", {"start": v(-1.7, 13) * mm, "end": v(2.3, 13) * mm});
            skLineSegment(sketch, "E20.6.7.3", {"start": v(2.3, 17) * mm, "end": v(2.3, 13) * mm});
            skLineSegment(sketch, "E20.6.8.0", {"start": v(-1.7, 11) * mm, "end": v(2.3, 11) * mm});
            skLineSegment(sketch, "E20.6.8.1", {"start": v(-1.7, 11) * mm, "end": v(-1.7, 7) * mm});
            skLineSegment(sketch, "E20.6.8.2", {"start": v(-1.7, 7) * mm, "end": v(2.3, 7) * mm});
            skLineSegment(sketch, "E20.6.8.3", {"start": v(2.3, 11) * mm, "end": v(2.3, 7) * mm});
            skLineSegment(sketch, "E20.6.9.0", {"start": v(-1.7, 5) * mm, "end": v(2.3, 5) * mm});
            skLineSegment(sketch, "E20.6.9.1", {"start": v(-1.7, 5) * mm, "end": v(-1.7, 1) * mm});
            skLineSegment(sketch, "E20.6.9.2", {"start": v(-1.7, 1) * mm, "end": v(2.3, 1) * mm});
            skLineSegment(sketch, "E20.6.9.3", {"start": v(2.3, 5) * mm, "end": v(2.3, 1) * mm});
            skLineSegment(sketch, "E20.6.10.0", {"start": v(-1.7, -1) * mm, "end": v(2.3, -1) * mm});
            skLineSegment(sketch, "E20.6.10.1", {"start": v(-1.7, -1) * mm, "end": v(-1.7, -5) * mm});
            skLineSegment(sketch, "E20.6.10.2", {"start": v(-1.7, -5) * mm, "end": v(2.3, -5) * mm});
            skLineSegment(sketch, "E20.6.10.3", {"start": v(2.3, -1) * mm, "end": v(2.3, -5) * mm});
            skLineSegment(sketch, "E20.6.11.0", {"start": v(-1.7, -7) * mm, "end": v(2.3, -7) * mm});
            skLineSegment(sketch, "E20.6.11.1", {"start": v(-1.7, -7) * mm, "end": v(-1.7, -11) * mm});
            skLineSegment(sketch, "E20.6.11.2", {"start": v(-1.7, -11) * mm, "end": v(2.3, -11) * mm});
            skLineSegment(sketch, "E20.6.11.3", {"start": v(2.3, -7) * mm, "end": v(2.3, -11) * mm});
            skLineSegment(sketch, "E20.6.12.0", {"start": v(-1.7, -13) * mm, "end": v(2.3, -13) * mm});
            skLineSegment(sketch, "E20.6.12.1", {"start": v(-1.7, -13) * mm, "end": v(-1.7, -17) * mm});
            skLineSegment(sketch, "E20.6.12.2", {"start": v(-1.7, -17) * mm, "end": v(2.3, -17) * mm});
            skLineSegment(sketch, "E20.6.12.3", {"start": v(2.3, -13) * mm, "end": v(2.3, -17) * mm});
            skLineSegment(sketch, "E20.6.13.0", {"start": v(-1.7, -19) * mm, "end": v(2.3, -19) * mm});
            skLineSegment(sketch, "E20.6.13.1", {"start": v(-1.7, -19) * mm, "end": v(-1.7, -23) * mm});
            skLineSegment(sketch, "E20.6.13.2", {"start": v(-1.7, -23) * mm, "end": v(2.3, -23) * mm});
            skLineSegment(sketch, "E20.6.13.3", {"start": v(2.3, -19) * mm, "end": v(2.3, -23) * mm});
            skLineSegment(sketch, "E20.6.14.0", {"start": v(-1.7, -25) * mm, "end": v(2.3, -25) * mm});
            skLineSegment(sketch, "E20.6.14.1", {"start": v(-1.7, -25) * mm, "end": v(-1.7, -29) * mm});
            skLineSegment(sketch, "E20.6.14.2", {"start": v(-1.7, -29) * mm, "end": v(2.3, -29) * mm});
            skLineSegment(sketch, "E20.6.14.3", {"start": v(2.3, -25) * mm, "end": v(2.3, -29) * mm});
            skLineSegment(sketch, "E20.7.0.0", {"start": v(4.3, 59) * mm, "end": v(8.3, 59) * mm});
            skLineSegment(sketch, "E20.7.0.1", {"start": v(4.3, 59) * mm, "end": v(4.3, 55) * mm});
            skLineSegment(sketch, "E20.7.0.2", {"start": v(4.3, 55) * mm, "end": v(8.3, 55) * mm});
            skLineSegment(sketch, "E20.7.0.3", {"start": v(8.3, 59) * mm, "end": v(8.3, 55) * mm});
            skLineSegment(sketch, "E20.7.1.0", {"start": v(4.3, 53) * mm, "end": v(8.3, 53) * mm});
            skLineSegment(sketch, "E20.7.1.1", {"start": v(4.3, 53) * mm, "end": v(4.3, 49) * mm});
            skLineSegment(sketch, "E20.7.1.2", {"start": v(4.3, 49) * mm, "end": v(8.3, 49) * mm});
            skLineSegment(sketch, "E20.7.1.3", {"start": v(8.3, 53) * mm, "end": v(8.3, 49) * mm});
            skLineSegment(sketch, "E20.7.2.0", {"start": v(4.3, 47) * mm, "end": v(8.3, 47) * mm});
            skLineSegment(sketch, "E20.7.2.1", {"start": v(4.3, 47) * mm, "end": v(4.3, 43) * mm});
            skLineSegment(sketch, "E20.7.2.2", {"start": v(4.3, 43) * mm, "end": v(8.3, 43) * mm});
            skLineSegment(sketch, "E20.7.2.3", {"start": v(8.3, 47) * mm, "end": v(8.3, 43) * mm});
            skLineSegment(sketch, "E20.7.3.0", {"start": v(4.3, 41) * mm, "end": v(8.3, 41) * mm});
            skLineSegment(sketch, "E20.7.3.1", {"start": v(4.3, 41) * mm, "end": v(4.3, 37) * mm});
            skLineSegment(sketch, "E20.7.3.2", {"start": v(4.3, 37) * mm, "end": v(8.3, 37) * mm});
            skLineSegment(sketch, "E20.7.3.3", {"start": v(8.3, 41) * mm, "end": v(8.3, 37) * mm});
            skLineSegment(sketch, "E20.7.4.0", {"start": v(4.3, 35) * mm, "end": v(8.3, 35) * mm});
            skLineSegment(sketch, "E20.7.4.1", {"start": v(4.3, 35) * mm, "end": v(4.3, 31) * mm});
            skLineSegment(sketch, "E20.7.4.2", {"start": v(4.3, 31) * mm, "end": v(8.3, 31) * mm});
            skLineSegment(sketch, "E20.7.4.3", {"start": v(8.3, 35) * mm, "end": v(8.3, 31) * mm});
            skLineSegment(sketch, "E20.7.5.0", {"start": v(4.3, 29) * mm, "end": v(8.3, 29) * mm});
            skLineSegment(sketch, "E20.7.5.1", {"start": v(4.3, 29) * mm, "end": v(4.3, 25) * mm});
            skLineSegment(sketch, "E20.7.5.2", {"start": v(4.3, 25) * mm, "end": v(8.3, 25) * mm});
            skLineSegment(sketch, "E20.7.5.3", {"start": v(8.3, 29) * mm, "end": v(8.3, 25) * mm});
            skLineSegment(sketch, "E20.7.6.0", {"start": v(4.3, 23) * mm, "end": v(8.3, 23) * mm});
            skLineSegment(sketch, "E20.7.6.1", {"start": v(4.3, 23) * mm, "end": v(4.3, 19) * mm});
            skLineSegment(sketch, "E20.7.6.2", {"start": v(4.3, 19) * mm, "end": v(8.3, 19) * mm});
            skLineSegment(sketch, "E20.7.6.3", {"start": v(8.3, 23) * mm, "end": v(8.3, 19) * mm});
            skLineSegment(sketch, "E20.7.7.0", {"start": v(4.3, 17) * mm, "end": v(8.3, 17) * mm});
            skLineSegment(sketch, "E20.7.7.1", {"start": v(4.3, 17) * mm, "end": v(4.3, 13) * mm});
            skLineSegment(sketch, "E20.7.7.2", {"start": v(4.3, 13) * mm, "end": v(8.3, 13) * mm});
            skLineSegment(sketch, "E20.7.7.3", {"start": v(8.3, 17) * mm, "end": v(8.3, 13) * mm});
            skLineSegment(sketch, "E20.7.8.0", {"start": v(4.3, 11) * mm, "end": v(8.3, 11) * mm});
            skLineSegment(sketch, "E20.7.8.1", {"start": v(4.3, 11) * mm, "end": v(4.3, 7) * mm});
            skLineSegment(sketch, "E20.7.8.2", {"start": v(4.3, 7) * mm, "end": v(8.3, 7) * mm});
            skLineSegment(sketch, "E20.7.8.3", {"start": v(8.3, 11) * mm, "end": v(8.3, 7) * mm});
            skLineSegment(sketch, "E20.7.9.0", {"start": v(4.3, 5) * mm, "end": v(8.3, 5) * mm});
            skLineSegment(sketch, "E20.7.9.1", {"start": v(4.3, 5) * mm, "end": v(4.3, 1) * mm});
            skLineSegment(sketch, "E20.7.9.2", {"start": v(4.3, 1) * mm, "end": v(8.3, 1) * mm});
            skLineSegment(sketch, "E20.7.9.3", {"start": v(8.3, 5) * mm, "end": v(8.3, 1) * mm});
            skLineSegment(sketch, "E20.7.10.0", {"start": v(4.3, -1) * mm, "end": v(8.3, -1) * mm});
            skLineSegment(sketch, "E20.7.10.1", {"start": v(4.3, -1) * mm, "end": v(4.3, -5) * mm});
            skLineSegment(sketch, "E20.7.10.2", {"start": v(4.3, -5) * mm, "end": v(8.3, -5) * mm});
            skLineSegment(sketch, "E20.7.10.3", {"start": v(8.3, -1) * mm, "end": v(8.3, -5) * mm});
            skLineSegment(sketch, "E20.7.11.0", {"start": v(4.3, -7) * mm, "end": v(8.3, -7) * mm});
            skLineSegment(sketch, "E20.7.11.1", {"start": v(4.3, -7) * mm, "end": v(4.3, -11) * mm});
            skLineSegment(sketch, "E20.7.11.2", {"start": v(4.3, -11) * mm, "end": v(8.3, -11) * mm});
            skLineSegment(sketch, "E20.7.11.3", {"start": v(8.3, -7) * mm, "end": v(8.3, -11) * mm});
            skLineSegment(sketch, "E20.7.12.0", {"start": v(4.3, -13) * mm, "end": v(8.3, -13) * mm});
            skLineSegment(sketch, "E20.7.12.1", {"start": v(4.3, -13) * mm, "end": v(4.3, -17) * mm});
            skLineSegment(sketch, "E20.7.12.2", {"start": v(4.3, -17) * mm, "end": v(8.3, -17) * mm});
            skLineSegment(sketch, "E20.7.12.3", {"start": v(8.3, -13) * mm, "end": v(8.3, -17) * mm});
            skLineSegment(sketch, "E20.7.13.0", {"start": v(4.3, -19) * mm, "end": v(8.3, -19) * mm});
            skLineSegment(sketch, "E20.7.13.1", {"start": v(4.3, -19) * mm, "end": v(4.3, -23) * mm});
            skLineSegment(sketch, "E20.7.13.2", {"start": v(4.3, -23) * mm, "end": v(8.3, -23) * mm});
            skLineSegment(sketch, "E20.7.13.3", {"start": v(8.3, -19) * mm, "end": v(8.3, -23) * mm});
            skLineSegment(sketch, "E20.7.14.0", {"start": v(4.3, -25) * mm, "end": v(8.3, -25) * mm});
            skLineSegment(sketch, "E20.7.14.1", {"start": v(4.3, -25) * mm, "end": v(4.3, -29) * mm});
            skLineSegment(sketch, "E20.7.14.2", {"start": v(4.3, -29) * mm, "end": v(8.3, -29) * mm});
            skLineSegment(sketch, "E20.7.14.3", {"start": v(8.3, -25) * mm, "end": v(8.3, -29) * mm});
            skLineSegment(sketch, "E20.8.0.0", {"start": v(10.3, 59) * mm, "end": v(14.3, 59) * mm});
            skLineSegment(sketch, "E20.8.0.1", {"start": v(10.3, 59) * mm, "end": v(10.3, 55) * mm});
            skLineSegment(sketch, "E20.8.0.2", {"start": v(10.3, 55) * mm, "end": v(14.3, 55) * mm});
            skLineSegment(sketch, "E20.8.0.3", {"start": v(14.3, 59) * mm, "end": v(14.3, 55) * mm});
            skLineSegment(sketch, "E20.8.1.0", {"start": v(10.3, 53) * mm, "end": v(14.3, 53) * mm});
            skLineSegment(sketch, "E20.8.1.1", {"start": v(10.3, 53) * mm, "end": v(10.3, 49) * mm});
            skLineSegment(sketch, "E20.8.1.2", {"start": v(10.3, 49) * mm, "end": v(14.3, 49) * mm});
            skLineSegment(sketch, "E20.8.1.3", {"start": v(14.3, 53) * mm, "end": v(14.3, 49) * mm});
            skLineSegment(sketch, "E20.8.2.0", {"start": v(10.3, 47) * mm, "end": v(14.3, 47) * mm});
            skLineSegment(sketch, "E20.8.2.1", {"start": v(10.3, 47) * mm, "end": v(10.3, 43) * mm});
            skLineSegment(sketch, "E20.8.2.2", {"start": v(10.3, 43) * mm, "end": v(14.3, 43) * mm});
            skLineSegment(sketch, "E20.8.2.3", {"start": v(14.3, 47) * mm, "end": v(14.3, 43) * mm});
            skLineSegment(sketch, "E20.8.3.0", {"start": v(10.3, 41) * mm, "end": v(14.3, 41) * mm});
            skLineSegment(sketch, "E20.8.3.1", {"start": v(10.3, 41) * mm, "end": v(10.3, 37) * mm});
            skLineSegment(sketch, "E20.8.3.2", {"start": v(10.3, 37) * mm, "end": v(14.3, 37) * mm});
            skLineSegment(sketch, "E20.8.3.3", {"start": v(14.3, 41) * mm, "end": v(14.3, 37) * mm});
            skLineSegment(sketch, "E20.8.4.0", {"start": v(10.3, 35) * mm, "end": v(14.3, 35) * mm});
            skLineSegment(sketch, "E20.8.4.1", {"start": v(10.3, 35) * mm, "end": v(10.3, 31) * mm});
            skLineSegment(sketch, "E20.8.4.2", {"start": v(10.3, 31) * mm, "end": v(14.3, 31) * mm});
            skLineSegment(sketch, "E20.8.4.3", {"start": v(14.3, 35) * mm, "end": v(14.3, 31) * mm});
            skLineSegment(sketch, "E20.8.5.0", {"start": v(10.3, 29) * mm, "end": v(14.3, 29) * mm});
            skLineSegment(sketch, "E20.8.5.1", {"start": v(10.3, 29) * mm, "end": v(10.3, 25) * mm});
            skLineSegment(sketch, "E20.8.5.2", {"start": v(10.3, 25) * mm, "end": v(14.3, 25) * mm});
            skLineSegment(sketch, "E20.8.5.3", {"start": v(14.3, 29) * mm, "end": v(14.3, 25) * mm});
            skLineSegment(sketch, "E20.8.6.0", {"start": v(10.3, 23) * mm, "end": v(14.3, 23) * mm});
            skLineSegment(sketch, "E20.8.6.1", {"start": v(10.3, 23) * mm, "end": v(10.3, 19) * mm});
            skLineSegment(sketch, "E20.8.6.2", {"start": v(10.3, 19) * mm, "end": v(14.3, 19) * mm});
            skLineSegment(sketch, "E20.8.6.3", {"start": v(14.3, 23) * mm, "end": v(14.3, 19) * mm});
            skLineSegment(sketch, "E20.8.7.0", {"start": v(10.3, 17) * mm, "end": v(14.3, 17) * mm});
            skLineSegment(sketch, "E20.8.7.1", {"start": v(10.3, 17) * mm, "end": v(10.3, 13) * mm});
            skLineSegment(sketch, "E20.8.7.2", {"start": v(10.3, 13) * mm, "end": v(14.3, 13) * mm});
            skLineSegment(sketch, "E20.8.7.3", {"start": v(14.3, 17) * mm, "end": v(14.3, 13) * mm});
            skLineSegment(sketch, "E20.8.8.0", {"start": v(10.3, 11) * mm, "end": v(14.3, 11) * mm});
            skLineSegment(sketch, "E20.8.8.1", {"start": v(10.3, 11) * mm, "end": v(10.3, 7) * mm});
            skLineSegment(sketch, "E20.8.8.2", {"start": v(10.3, 7) * mm, "end": v(14.3, 7) * mm});
            skLineSegment(sketch, "E20.8.8.3", {"start": v(14.3, 11) * mm, "end": v(14.3, 7) * mm});
            skLineSegment(sketch, "E20.8.9.0", {"start": v(10.3, 5) * mm, "end": v(14.3, 5) * mm});
            skLineSegment(sketch, "E20.8.9.1", {"start": v(10.3, 5) * mm, "end": v(10.3, 1) * mm});
            skLineSegment(sketch, "E20.8.9.2", {"start": v(10.3, 1) * mm, "end": v(14.3, 1) * mm});
            skLineSegment(sketch, "E20.8.9.3", {"start": v(14.3, 5) * mm, "end": v(14.3, 1) * mm});
            skLineSegment(sketch, "E20.8.10.0", {"start": v(10.3, -1) * mm, "end": v(14.3, -1) * mm});
            skLineSegment(sketch, "E20.8.10.1", {"start": v(10.3, -1) * mm, "end": v(10.3, -5) * mm});
            skLineSegment(sketch, "E20.8.10.2", {"start": v(10.3, -5) * mm, "end": v(14.3, -5) * mm});
            skLineSegment(sketch, "E20.8.10.3", {"start": v(14.3, -1) * mm, "end": v(14.3, -5) * mm});
            skLineSegment(sketch, "E20.8.11.0", {"start": v(10.3, -7) * mm, "end": v(14.3, -7) * mm});
            skLineSegment(sketch, "E20.8.11.1", {"start": v(10.3, -7) * mm, "end": v(10.3, -11) * mm});
            skLineSegment(sketch, "E20.8.11.2", {"start": v(10.3, -11) * mm, "end": v(14.3, -11) * mm});
            skLineSegment(sketch, "E20.8.11.3", {"start": v(14.3, -7) * mm, "end": v(14.3, -11) * mm});
            skLineSegment(sketch, "E20.8.12.0", {"start": v(10.3, -13) * mm, "end": v(14.3, -13) * mm});
            skLineSegment(sketch, "E20.8.12.1", {"start": v(10.3, -13) * mm, "end": v(10.3, -17) * mm});
            skLineSegment(sketch, "E20.8.12.2", {"start": v(10.3, -17) * mm, "end": v(14.3, -17) * mm});
            skLineSegment(sketch, "E20.8.12.3", {"start": v(14.3, -13) * mm, "end": v(14.3, -17) * mm});
            skLineSegment(sketch, "E20.8.13.0", {"start": v(10.3, -19) * mm, "end": v(14.3, -19) * mm});
            skLineSegment(sketch, "E20.8.13.1", {"start": v(10.3, -19) * mm, "end": v(10.3, -23) * mm});
            skLineSegment(sketch, "E20.8.13.2", {"start": v(10.3, -23) * mm, "end": v(14.3, -23) * mm});
            skLineSegment(sketch, "E20.8.13.3", {"start": v(14.3, -19) * mm, "end": v(14.3, -23) * mm});
            skLineSegment(sketch, "E20.8.14.0", {"start": v(10.3, -25) * mm, "end": v(14.3, -25) * mm});
            skLineSegment(sketch, "E20.8.14.1", {"start": v(10.3, -25) * mm, "end": v(10.3, -29) * mm});
            skLineSegment(sketch, "E20.8.14.2", {"start": v(10.3, -29) * mm, "end": v(14.3, -29) * mm});
            skLineSegment(sketch, "E20.8.14.3", {"start": v(14.3, -25) * mm, "end": v(14.3, -29) * mm});
            skLineSegment(sketch, "E20.9.0.0", {"start": v(16.3, 59) * mm, "end": v(20.3, 59) * mm});
            skLineSegment(sketch, "E20.9.0.1", {"start": v(16.3, 59) * mm, "end": v(16.3, 55) * mm});
            skLineSegment(sketch, "E20.9.0.2", {"start": v(16.3, 55) * mm, "end": v(20.3, 55) * mm});
            skLineSegment(sketch, "E20.9.0.3", {"start": v(20.3, 59) * mm, "end": v(20.3, 55) * mm});
            skLineSegment(sketch, "E20.9.1.0", {"start": v(16.3, 53) * mm, "end": v(20.3, 53) * mm});
            skLineSegment(sketch, "E20.9.1.1", {"start": v(16.3, 53) * mm, "end": v(16.3, 49) * mm});
            skLineSegment(sketch, "E20.9.1.2", {"start": v(16.3, 49) * mm, "end": v(20.3, 49) * mm});
            skLineSegment(sketch, "E20.9.1.3", {"start": v(20.3, 53) * mm, "end": v(20.3, 49) * mm});
            skLineSegment(sketch, "E20.9.2.0", {"start": v(16.3, 47) * mm, "end": v(20.3, 47) * mm});
            skLineSegment(sketch, "E20.9.2.1", {"start": v(16.3, 47) * mm, "end": v(16.3, 43) * mm});
            skLineSegment(sketch, "E20.9.2.2", {"start": v(16.3, 43) * mm, "end": v(20.3, 43) * mm});
            skLineSegment(sketch, "E20.9.2.3", {"start": v(20.3, 47) * mm, "end": v(20.3, 43) * mm});
            skLineSegment(sketch, "E20.9.3.0", {"start": v(16.3, 41) * mm, "end": v(20.3, 41) * mm});
            skLineSegment(sketch, "E20.9.3.1", {"start": v(16.3, 41) * mm, "end": v(16.3, 37) * mm});
            skLineSegment(sketch, "E20.9.3.2", {"start": v(16.3, 37) * mm, "end": v(20.3, 37) * mm});
            skLineSegment(sketch, "E20.9.3.3", {"start": v(20.3, 41) * mm, "end": v(20.3, 37) * mm});
            skLineSegment(sketch, "E20.9.4.0", {"start": v(16.3, 35) * mm, "end": v(20.3, 35) * mm});
            skLineSegment(sketch, "E20.9.4.1", {"start": v(16.3, 35) * mm, "end": v(16.3, 31) * mm});
            skLineSegment(sketch, "E20.9.4.2", {"start": v(16.3, 31) * mm, "end": v(20.3, 31) * mm});
            skLineSegment(sketch, "E20.9.4.3", {"start": v(20.3, 35) * mm, "end": v(20.3, 31) * mm});
            skLineSegment(sketch, "E20.9.5.0", {"start": v(16.3, 29) * mm, "end": v(20.3, 29) * mm});
            skLineSegment(sketch, "E20.9.5.1", {"start": v(16.3, 29) * mm, "end": v(16.3, 25) * mm});
            skLineSegment(sketch, "E20.9.5.2", {"start": v(16.3, 25) * mm, "end": v(20.3, 25) * mm});
            skLineSegment(sketch, "E20.9.5.3", {"start": v(20.3, 29) * mm, "end": v(20.3, 25) * mm});
            skLineSegment(sketch, "E20.9.6.0", {"start": v(16.3, 23) * mm, "end": v(20.3, 23) * mm});
            skLineSegment(sketch, "E20.9.6.1", {"start": v(16.3, 23) * mm, "end": v(16.3, 19) * mm});
            skLineSegment(sketch, "E20.9.6.2", {"start": v(16.3, 19) * mm, "end": v(20.3, 19) * mm});
            skLineSegment(sketch, "E20.9.6.3", {"start": v(20.3, 23) * mm, "end": v(20.3, 19) * mm});
            skLineSegment(sketch, "E20.9.7.0", {"start": v(16.3, 17) * mm, "end": v(20.3, 17) * mm});
            skLineSegment(sketch, "E20.9.7.1", {"start": v(16.3, 17) * mm, "end": v(16.3, 13) * mm});
            skLineSegment(sketch, "E20.9.7.2", {"start": v(16.3, 13) * mm, "end": v(20.3, 13) * mm});
            skLineSegment(sketch, "E20.9.7.3", {"start": v(20.3, 17) * mm, "end": v(20.3, 13) * mm});
            skLineSegment(sketch, "E20.9.8.0", {"start": v(16.3, 11) * mm, "end": v(20.3, 11) * mm});
            skLineSegment(sketch, "E20.9.8.1", {"start": v(16.3, 11) * mm, "end": v(16.3, 7) * mm});
            skLineSegment(sketch, "E20.9.8.2", {"start": v(16.3, 7) * mm, "end": v(20.3, 7) * mm});
            skLineSegment(sketch, "E20.9.8.3", {"start": v(20.3, 11) * mm, "end": v(20.3, 7) * mm});
            skLineSegment(sketch, "E20.9.9.0", {"start": v(16.3, 5) * mm, "end": v(20.3, 5) * mm});
            skLineSegment(sketch, "E20.9.9.1", {"start": v(16.3, 5) * mm, "end": v(16.3, 1) * mm});
            skLineSegment(sketch, "E20.9.9.2", {"start": v(16.3, 1) * mm, "end": v(20.3, 1) * mm});
            skLineSegment(sketch, "E20.9.9.3", {"start": v(20.3, 5) * mm, "end": v(20.3, 1) * mm});
            skLineSegment(sketch, "E20.9.10.0", {"start": v(16.3, -1) * mm, "end": v(20.3, -1) * mm});
            skLineSegment(sketch, "E20.9.10.1", {"start": v(16.3, -1) * mm, "end": v(16.3, -5) * mm});
            skLineSegment(sketch, "E20.9.10.2", {"start": v(16.3, -5) * mm, "end": v(20.3, -5) * mm});
            skLineSegment(sketch, "E20.9.10.3", {"start": v(20.3, -1) * mm, "end": v(20.3, -5) * mm});
            skLineSegment(sketch, "E20.9.11.0", {"start": v(16.3, -7) * mm, "end": v(20.3, -7) * mm});
            skLineSegment(sketch, "E20.9.11.1", {"start": v(16.3, -7) * mm, "end": v(16.3, -11) * mm});
            skLineSegment(sketch, "E20.9.11.2", {"start": v(16.3, -11) * mm, "end": v(20.3, -11) * mm});
            skLineSegment(sketch, "E20.9.11.3", {"start": v(20.3, -7) * mm, "end": v(20.3, -11) * mm});
            skLineSegment(sketch, "E20.9.12.0", {"start": v(16.3, -13) * mm, "end": v(20.3, -13) * mm});
            skLineSegment(sketch, "E20.9.12.1", {"start": v(16.3, -13) * mm, "end": v(16.3, -17) * mm});
            skLineSegment(sketch, "E20.9.12.2", {"start": v(16.3, -17) * mm, "end": v(20.3, -17) * mm});
            skLineSegment(sketch, "E20.9.12.3", {"start": v(20.3, -13) * mm, "end": v(20.3, -17) * mm});
            skLineSegment(sketch, "E20.9.13.0", {"start": v(16.3, -19) * mm, "end": v(20.3, -19) * mm});
            skLineSegment(sketch, "E20.9.13.1", {"start": v(16.3, -19) * mm, "end": v(16.3, -23) * mm});
            skLineSegment(sketch, "E20.9.13.2", {"start": v(16.3, -23) * mm, "end": v(20.3, -23) * mm});
            skLineSegment(sketch, "E20.9.13.3", {"start": v(20.3, -19) * mm, "end": v(20.3, -23) * mm});
            skLineSegment(sketch, "E20.9.14.0", {"start": v(16.3, -25) * mm, "end": v(20.3, -25) * mm});
            skLineSegment(sketch, "E20.9.14.1", {"start": v(16.3, -25) * mm, "end": v(16.3, -29) * mm});
            skLineSegment(sketch, "E20.9.14.2", {"start": v(16.3, -29) * mm, "end": v(20.3, -29) * mm});
            skLineSegment(sketch, "E20.9.14.3", {"start": v(20.3, -25) * mm, "end": v(20.3, -29) * mm});
            skLineSegment(sketch, "E20.direction1", {"start": v(-37.7, 59) * mm, "end": v(-31.7, 59) * mm, "construction": true});
            skLineSegment(sketch, "E20.direction2", {"start": v(-37.7, 59) * mm, "end": v(-37.7, 53) * mm, "construction": true});
            skLineSegment(sketch, "E21.0.10.0", {"start": v(22.3, 59) * mm, "end": v(26.3, 59) * mm});
            skLineSegment(sketch, "E21.3.10.0", {"start": v(22.3, 59) * mm, "end": v(22.3, 55) * mm});
            skLineSegment(sketch, "E21.6.10.0", {"start": v(22.3, 55) * mm, "end": v(26.3, 55) * mm});
            skLineSegment(sketch, "E21.9.10.0", {"start": v(26.3, 59) * mm, "end": v(26.3, 55) * mm});
            skLineSegment(sketch, "E21.0.10.1", {"start": v(22.3, 53) * mm, "end": v(26.3, 53) * mm});
            skLineSegment(sketch, "E21.3.10.1", {"start": v(22.3, 53) * mm, "end": v(22.3, 49) * mm});
            skLineSegment(sketch, "E21.6.10.1", {"start": v(22.3, 49) * mm, "end": v(26.3, 49) * mm});
            skLineSegment(sketch, "E21.9.10.1", {"start": v(26.3, 53) * mm, "end": v(26.3, 49) * mm});
            skLineSegment(sketch, "E21.0.10.2", {"start": v(22.3, 47) * mm, "end": v(26.3, 47) * mm});
            skLineSegment(sketch, "E21.3.10.2", {"start": v(22.3, 47) * mm, "end": v(22.3, 43) * mm});
            skLineSegment(sketch, "E21.6.10.2", {"start": v(22.3, 43) * mm, "end": v(26.3, 43) * mm});
            skLineSegment(sketch, "E21.9.10.2", {"start": v(26.3, 47) * mm, "end": v(26.3, 43) * mm});
            skLineSegment(sketch, "E21.0.10.3", {"start": v(22.3, 41) * mm, "end": v(26.3, 41) * mm});
            skLineSegment(sketch, "E21.3.10.3", {"start": v(22.3, 41) * mm, "end": v(22.3, 37) * mm});
            skLineSegment(sketch, "E21.6.10.3", {"start": v(22.3, 37) * mm, "end": v(26.3, 37) * mm});
            skLineSegment(sketch, "E21.9.10.3", {"start": v(26.3, 41) * mm, "end": v(26.3, 37) * mm});
            skLineSegment(sketch, "E21.0.10.4", {"start": v(22.3, 35) * mm, "end": v(26.3, 35) * mm});
            skLineSegment(sketch, "E21.3.10.4", {"start": v(22.3, 35) * mm, "end": v(22.3, 31) * mm});
            skLineSegment(sketch, "E21.6.10.4", {"start": v(22.3, 31) * mm, "end": v(26.3, 31) * mm});
            skLineSegment(sketch, "E21.9.10.4", {"start": v(26.3, 35) * mm, "end": v(26.3, 31) * mm});
            skLineSegment(sketch, "E21.0.10.5", {"start": v(22.3, 29) * mm, "end": v(26.3, 29) * mm});
            skLineSegment(sketch, "E21.3.10.5", {"start": v(22.3, 29) * mm, "end": v(22.3, 25) * mm});
            skLineSegment(sketch, "E21.6.10.5", {"start": v(22.3, 25) * mm, "end": v(26.3, 25) * mm});
            skLineSegment(sketch, "E21.9.10.5", {"start": v(26.3, 29) * mm, "end": v(26.3, 25) * mm});
            skLineSegment(sketch, "E21.0.10.6", {"start": v(22.3, 23) * mm, "end": v(26.3, 23) * mm});
            skLineSegment(sketch, "E21.3.10.6", {"start": v(22.3, 23) * mm, "end": v(22.3, 19) * mm});
            skLineSegment(sketch, "E21.6.10.6", {"start": v(22.3, 19) * mm, "end": v(26.3, 19) * mm});
            skLineSegment(sketch, "E21.9.10.6", {"start": v(26.3, 23) * mm, "end": v(26.3, 19) * mm});
            skLineSegment(sketch, "E21.0.10.7", {"start": v(22.3, 17) * mm, "end": v(26.3, 17) * mm});
            skLineSegment(sketch, "E21.3.10.7", {"start": v(22.3, 17) * mm, "end": v(22.3, 13) * mm});
            skLineSegment(sketch, "E21.6.10.7", {"start": v(22.3, 13) * mm, "end": v(26.3, 13) * mm});
            skLineSegment(sketch, "E21.9.10.7", {"start": v(26.3, 17) * mm, "end": v(26.3, 13) * mm});
            skLineSegment(sketch, "E21.0.10.8", {"start": v(22.3, 11) * mm, "end": v(26.3, 11) * mm});
            skLineSegment(sketch, "E21.3.10.8", {"start": v(22.3, 11) * mm, "end": v(22.3, 7) * mm});
            skLineSegment(sketch, "E21.6.10.8", {"start": v(22.3, 7) * mm, "end": v(26.3, 7) * mm});
            skLineSegment(sketch, "E21.9.10.8", {"start": v(26.3, 11) * mm, "end": v(26.3, 7) * mm});
            skLineSegment(sketch, "E21.0.10.9", {"start": v(22.3, 5) * mm, "end": v(26.3, 5) * mm});
            skLineSegment(sketch, "E21.3.10.9", {"start": v(22.3, 5) * mm, "end": v(22.3, 1) * mm});
            skLineSegment(sketch, "E21.6.10.9", {"start": v(22.3, 1) * mm, "end": v(26.3, 1) * mm});
            skLineSegment(sketch, "E21.9.10.9", {"start": v(26.3, 5) * mm, "end": v(26.3, 1) * mm});
            skLineSegment(sketch, "E21.0.10.10", {"start": v(22.3, -1) * mm, "end": v(26.3, -1) * mm});
            skLineSegment(sketch, "E21.3.10.10", {"start": v(22.3, -1) * mm, "end": v(22.3, -5) * mm});
            skLineSegment(sketch, "E21.6.10.10", {"start": v(22.3, -5) * mm, "end": v(26.3, -5) * mm});
            skLineSegment(sketch, "E21.9.10.10", {"start": v(26.3, -1) * mm, "end": v(26.3, -5) * mm});
            skLineSegment(sketch, "E21.0.10.11", {"start": v(22.3, -7) * mm, "end": v(26.3, -7) * mm});
            skLineSegment(sketch, "E21.3.10.11", {"start": v(22.3, -7) * mm, "end": v(22.3, -11) * mm});
            skLineSegment(sketch, "E21.6.10.11", {"start": v(22.3, -11) * mm, "end": v(26.3, -11) * mm});
            skLineSegment(sketch, "E21.9.10.11", {"start": v(26.3, -7) * mm, "end": v(26.3, -11) * mm});
            skLineSegment(sketch, "E21.0.10.12", {"start": v(22.3, -13) * mm, "end": v(26.3, -13) * mm});
            skLineSegment(sketch, "E21.3.10.12", {"start": v(22.3, -13) * mm, "end": v(22.3, -17) * mm});
            skLineSegment(sketch, "E21.6.10.12", {"start": v(22.3, -17) * mm, "end": v(26.3, -17) * mm});
            skLineSegment(sketch, "E21.9.10.12", {"start": v(26.3, -13) * mm, "end": v(26.3, -17) * mm});
            skLineSegment(sketch, "E21.0.10.13", {"start": v(22.3, -19) * mm, "end": v(26.3, -19) * mm});
            skLineSegment(sketch, "E21.3.10.13", {"start": v(22.3, -19) * mm, "end": v(22.3, -23) * mm});
            skLineSegment(sketch, "E21.6.10.13", {"start": v(22.3, -23) * mm, "end": v(26.3, -23) * mm});
            skLineSegment(sketch, "E21.9.10.13", {"start": v(26.3, -19) * mm, "end": v(26.3, -23) * mm});
            skLineSegment(sketch, "E21.0.10.14", {"start": v(22.3, -25) * mm, "end": v(26.3, -25) * mm});
            skLineSegment(sketch, "E21.3.10.14", {"start": v(22.3, -25) * mm, "end": v(22.3, -29) * mm});
            skLineSegment(sketch, "E21.6.10.14", {"start": v(22.3, -29) * mm, "end": v(26.3, -29) * mm});
            skLineSegment(sketch, "E21.9.10.14", {"start": v(26.3, -25) * mm, "end": v(26.3, -29) * mm});
            skLineSegment(sketch, "E21.0.11.0", {"start": v(28.3, 59) * mm, "end": v(32.3, 59) * mm});
            skLineSegment(sketch, "E21.3.11.0", {"start": v(28.3, 59) * mm, "end": v(28.3, 55) * mm});
            skLineSegment(sketch, "E21.6.11.0", {"start": v(28.3, 55) * mm, "end": v(32.3, 55) * mm});
            skLineSegment(sketch, "E21.9.11.0", {"start": v(32.3, 59) * mm, "end": v(32.3, 55) * mm});
            skLineSegment(sketch, "E21.0.11.1", {"start": v(28.3, 53) * mm, "end": v(32.3, 53) * mm});
            skLineSegment(sketch, "E21.3.11.1", {"start": v(28.3, 53) * mm, "end": v(28.3, 49) * mm});
            skLineSegment(sketch, "E21.6.11.1", {"start": v(28.3, 49) * mm, "end": v(32.3, 49) * mm});
            skLineSegment(sketch, "E21.9.11.1", {"start": v(32.3, 53) * mm, "end": v(32.3, 49) * mm});
            skLineSegment(sketch, "E21.0.11.2", {"start": v(28.3, 47) * mm, "end": v(32.3, 47) * mm});
            skLineSegment(sketch, "E21.3.11.2", {"start": v(28.3, 47) * mm, "end": v(28.3, 43) * mm});
            skLineSegment(sketch, "E21.6.11.2", {"start": v(28.3, 43) * mm, "end": v(32.3, 43) * mm});
            skLineSegment(sketch, "E21.9.11.2", {"start": v(32.3, 47) * mm, "end": v(32.3, 43) * mm});
            skLineSegment(sketch, "E21.0.11.3", {"start": v(28.3, 41) * mm, "end": v(32.3, 41) * mm});
            skLineSegment(sketch, "E21.3.11.3", {"start": v(28.3, 41) * mm, "end": v(28.3, 37) * mm});
            skLineSegment(sketch, "E21.6.11.3", {"start": v(28.3, 37) * mm, "end": v(32.3, 37) * mm});
            skLineSegment(sketch, "E21.9.11.3", {"start": v(32.3, 41) * mm, "end": v(32.3, 37) * mm});
            skLineSegment(sketch, "E21.0.11.4", {"start": v(28.3, 35) * mm, "end": v(32.3, 35) * mm});
            skLineSegment(sketch, "E21.3.11.4", {"start": v(28.3, 35) * mm, "end": v(28.3, 31) * mm});
            skLineSegment(sketch, "E21.6.11.4", {"start": v(28.3, 31) * mm, "end": v(32.3, 31) * mm});
            skLineSegment(sketch, "E21.9.11.4", {"start": v(32.3, 35) * mm, "end": v(32.3, 31) * mm});
            skLineSegment(sketch, "E21.0.11.5", {"start": v(28.3, 29) * mm, "end": v(32.3, 29) * mm});
            skLineSegment(sketch, "E21.3.11.5", {"start": v(28.3, 29) * mm, "end": v(28.3, 25) * mm});
            skLineSegment(sketch, "E21.6.11.5", {"start": v(28.3, 25) * mm, "end": v(32.3, 25) * mm});
            skLineSegment(sketch, "E21.9.11.5", {"start": v(32.3, 29) * mm, "end": v(32.3, 25) * mm});
            skLineSegment(sketch, "E21.0.11.6", {"start": v(28.3, 23) * mm, "end": v(32.3, 23) * mm});
            skLineSegment(sketch, "E21.3.11.6", {"start": v(28.3, 23) * mm, "end": v(28.3, 19) * mm});
            skLineSegment(sketch, "E21.6.11.6", {"start": v(28.3, 19) * mm, "end": v(32.3, 19) * mm});
            skLineSegment(sketch, "E21.9.11.6", {"start": v(32.3, 23) * mm, "end": v(32.3, 19) * mm});
            skLineSegment(sketch, "E21.0.11.7", {"start": v(28.3, 17) * mm, "end": v(32.3, 17) * mm});
            skLineSegment(sketch, "E21.3.11.7", {"start": v(28.3, 17) * mm, "end": v(28.3, 13) * mm});
            skLineSegment(sketch, "E21.6.11.7", {"start": v(28.3, 13) * mm, "end": v(32.3, 13) * mm});
            skLineSegment(sketch, "E21.9.11.7", {"start": v(32.3, 17) * mm, "end": v(32.3, 13) * mm});
            skLineSegment(sketch, "E21.0.11.8", {"start": v(28.3, 11) * mm, "end": v(32.3, 11) * mm});
            skLineSegment(sketch, "E21.3.11.8", {"start": v(28.3, 11) * mm, "end": v(28.3, 7) * mm});
            skLineSegment(sketch, "E21.6.11.8", {"start": v(28.3, 7) * mm, "end": v(32.3, 7) * mm});
            skLineSegment(sketch, "E21.9.11.8", {"start": v(32.3, 11) * mm, "end": v(32.3, 7) * mm});
            skLineSegment(sketch, "E21.0.11.9", {"start": v(28.3, 5) * mm, "end": v(32.3, 5) * mm});
            skLineSegment(sketch, "E21.3.11.9", {"start": v(28.3, 5) * mm, "end": v(28.3, 1) * mm});
            skLineSegment(sketch, "E21.6.11.9", {"start": v(28.3, 1) * mm, "end": v(32.3, 1) * mm});
            skLineSegment(sketch, "E21.9.11.9", {"start": v(32.3, 5) * mm, "end": v(32.3, 1) * mm});
            skLineSegment(sketch, "E21.0.11.10", {"start": v(28.3, -1) * mm, "end": v(32.3, -1) * mm});
            skLineSegment(sketch, "E21.3.11.10", {"start": v(28.3, -1) * mm, "end": v(28.3, -5) * mm});
            skLineSegment(sketch, "E21.6.11.10", {"start": v(28.3, -5) * mm, "end": v(32.3, -5) * mm});
            skLineSegment(sketch, "E21.9.11.10", {"start": v(32.3, -1) * mm, "end": v(32.3, -5) * mm});
            skLineSegment(sketch, "E21.0.11.11", {"start": v(28.3, -7) * mm, "end": v(32.3, -7) * mm});
            skLineSegment(sketch, "E21.3.11.11", {"start": v(28.3, -7) * mm, "end": v(28.3, -11) * mm});
            skLineSegment(sketch, "E21.6.11.11", {"start": v(28.3, -11) * mm, "end": v(32.3, -11) * mm});
            skLineSegment(sketch, "E21.9.11.11", {"start": v(32.3, -7) * mm, "end": v(32.3, -11) * mm});
            skLineSegment(sketch, "E21.0.11.12", {"start": v(28.3, -13) * mm, "end": v(32.3, -13) * mm});
            skLineSegment(sketch, "E21.3.11.12", {"start": v(28.3, -13) * mm, "end": v(28.3, -17) * mm});
            skLineSegment(sketch, "E21.6.11.12", {"start": v(28.3, -17) * mm, "end": v(32.3, -17) * mm});
            skLineSegment(sketch, "E21.9.11.12", {"start": v(32.3, -13) * mm, "end": v(32.3, -17) * mm});
            skLineSegment(sketch, "E21.0.11.13", {"start": v(28.3, -19) * mm, "end": v(32.3, -19) * mm});
            skLineSegment(sketch, "E21.3.11.13", {"start": v(28.3, -19) * mm, "end": v(28.3, -23) * mm});
            skLineSegment(sketch, "E21.6.11.13", {"start": v(28.3, -23) * mm, "end": v(32.3, -23) * mm});
            skLineSegment(sketch, "E21.9.11.13", {"start": v(32.3, -19) * mm, "end": v(32.3, -23) * mm});
            skLineSegment(sketch, "E21.0.11.14", {"start": v(28.3, -25) * mm, "end": v(32.3, -25) * mm});
            skLineSegment(sketch, "E21.3.11.14", {"start": v(28.3, -25) * mm, "end": v(28.3, -29) * mm});
            skLineSegment(sketch, "E21.6.11.14", {"start": v(28.3, -29) * mm, "end": v(32.3, -29) * mm});
            skLineSegment(sketch, "E21.9.11.14", {"start": v(32.3, -25) * mm, "end": v(32.3, -29) * mm});
            skLineSegment(sketch, "E21.0.12.0", {"start": v(34.3, 59) * mm, "end": v(38.3, 59) * mm});
            skLineSegment(sketch, "E21.3.12.0", {"start": v(34.3, 59) * mm, "end": v(34.3, 55) * mm});
            skLineSegment(sketch, "E21.6.12.0", {"start": v(34.3, 55) * mm, "end": v(38.3, 55) * mm});
            skLineSegment(sketch, "E21.9.12.0", {"start": v(38.3, 59) * mm, "end": v(38.3, 55) * mm});
            skLineSegment(sketch, "E21.0.12.1", {"start": v(34.3, 53) * mm, "end": v(38.3, 53) * mm});
            skLineSegment(sketch, "E21.3.12.1", {"start": v(34.3, 53) * mm, "end": v(34.3, 49) * mm});
            skLineSegment(sketch, "E21.6.12.1", {"start": v(34.3, 49) * mm, "end": v(38.3, 49) * mm});
            skLineSegment(sketch, "E21.9.12.1", {"start": v(38.3, 53) * mm, "end": v(38.3, 49) * mm});
            skLineSegment(sketch, "E21.0.12.2", {"start": v(34.3, 47) * mm, "end": v(38.3, 47) * mm});
            skLineSegment(sketch, "E21.3.12.2", {"start": v(34.3, 47) * mm, "end": v(34.3, 43) * mm});
            skLineSegment(sketch, "E21.6.12.2", {"start": v(34.3, 43) * mm, "end": v(38.3, 43) * mm});
            skLineSegment(sketch, "E21.9.12.2", {"start": v(38.3, 47) * mm, "end": v(38.3, 43) * mm});
            skLineSegment(sketch, "E21.0.12.3", {"start": v(34.3, 41) * mm, "end": v(38.3, 41) * mm});
            skLineSegment(sketch, "E21.3.12.3", {"start": v(34.3, 41) * mm, "end": v(34.3, 37) * mm});
            skLineSegment(sketch, "E21.6.12.3", {"start": v(34.3, 37) * mm, "end": v(38.3, 37) * mm});
            skLineSegment(sketch, "E21.9.12.3", {"start": v(38.3, 41) * mm, "end": v(38.3, 37) * mm});
            skLineSegment(sketch, "E21.0.12.4", {"start": v(34.3, 35) * mm, "end": v(38.3, 35) * mm});
            skLineSegment(sketch, "E21.3.12.4", {"start": v(34.3, 35) * mm, "end": v(34.3, 31) * mm});
            skLineSegment(sketch, "E21.6.12.4", {"start": v(34.3, 31) * mm, "end": v(38.3, 31) * mm});
            skLineSegment(sketch, "E21.9.12.4", {"start": v(38.3, 35) * mm, "end": v(38.3, 31) * mm});
            skLineSegment(sketch, "E21.0.12.5", {"start": v(34.3, 29) * mm, "end": v(38.3, 29) * mm});
            skLineSegment(sketch, "E21.3.12.5", {"start": v(34.3, 29) * mm, "end": v(34.3, 25) * mm});
            skLineSegment(sketch, "E21.6.12.5", {"start": v(34.3, 25) * mm, "end": v(38.3, 25) * mm});
            skLineSegment(sketch, "E21.9.12.5", {"start": v(38.3, 29) * mm, "end": v(38.3, 25) * mm});
            skLineSegment(sketch, "E21.0.12.6", {"start": v(34.3, 23) * mm, "end": v(38.3, 23) * mm});
            skLineSegment(sketch, "E21.3.12.6", {"start": v(34.3, 23) * mm, "end": v(34.3, 19) * mm});
            skLineSegment(sketch, "E21.6.12.6", {"start": v(34.3, 19) * mm, "end": v(38.3, 19) * mm});
            skLineSegment(sketch, "E21.9.12.6", {"start": v(38.3, 23) * mm, "end": v(38.3, 19) * mm});
            skLineSegment(sketch, "E21.0.12.7", {"start": v(34.3, 17) * mm, "end": v(38.3, 17) * mm});
            skLineSegment(sketch, "E21.3.12.7", {"start": v(34.3, 17) * mm, "end": v(34.3, 13) * mm});
            skLineSegment(sketch, "E21.6.12.7", {"start": v(34.3, 13) * mm, "end": v(38.3, 13) * mm});
            skLineSegment(sketch, "E21.9.12.7", {"start": v(38.3, 17) * mm, "end": v(38.3, 13) * mm});
            skLineSegment(sketch, "E21.0.12.8", {"start": v(34.3, 11) * mm, "end": v(38.3, 11) * mm});
            skLineSegment(sketch, "E21.3.12.8", {"start": v(34.3, 11) * mm, "end": v(34.3, 7) * mm});
            skLineSegment(sketch, "E21.6.12.8", {"start": v(34.3, 7) * mm, "end": v(38.3, 7) * mm});
            skLineSegment(sketch, "E21.9.12.8", {"start": v(38.3, 11) * mm, "end": v(38.3, 7) * mm});
            skLineSegment(sketch, "E21.0.12.9", {"start": v(34.3, 5) * mm, "end": v(38.3, 5) * mm});
            skLineSegment(sketch, "E21.3.12.9", {"start": v(34.3, 5) * mm, "end": v(34.3, 1) * mm});
            skLineSegment(sketch, "E21.6.12.9", {"start": v(34.3, 1) * mm, "end": v(38.3, 1) * mm});
            skLineSegment(sketch, "E21.9.12.9", {"start": v(38.3, 5) * mm, "end": v(38.3, 1) * mm});
            skLineSegment(sketch, "E21.0.12.10", {"start": v(34.3, -1) * mm, "end": v(38.3, -1) * mm});
            skLineSegment(sketch, "E21.3.12.10", {"start": v(34.3, -1) * mm, "end": v(34.3, -5) * mm});
            skLineSegment(sketch, "E21.6.12.10", {"start": v(34.3, -5) * mm, "end": v(38.3, -5) * mm});
            skLineSegment(sketch, "E21.9.12.10", {"start": v(38.3, -1) * mm, "end": v(38.3, -5) * mm});
            skLineSegment(sketch, "E21.0.12.11", {"start": v(34.3, -7) * mm, "end": v(38.3, -7) * mm});
            skLineSegment(sketch, "E21.3.12.11", {"start": v(34.3, -7) * mm, "end": v(34.3, -11) * mm});
            skLineSegment(sketch, "E21.6.12.11", {"start": v(34.3, -11) * mm, "end": v(38.3, -11) * mm});
            skLineSegment(sketch, "E21.9.12.11", {"start": v(38.3, -7) * mm, "end": v(38.3, -11) * mm});
            skLineSegment(sketch, "E21.0.12.12", {"start": v(34.3, -13) * mm, "end": v(38.3, -13) * mm});
            skLineSegment(sketch, "E21.3.12.12", {"start": v(34.3, -13) * mm, "end": v(34.3, -17) * mm});
            skLineSegment(sketch, "E21.6.12.12", {"start": v(34.3, -17) * mm, "end": v(38.3, -17) * mm});
            skLineSegment(sketch, "E21.9.12.12", {"start": v(38.3, -13) * mm, "end": v(38.3, -17) * mm});
            skLineSegment(sketch, "E21.0.12.13", {"start": v(34.3, -19) * mm, "end": v(38.3, -19) * mm});
            skLineSegment(sketch, "E21.3.12.13", {"start": v(34.3, -19) * mm, "end": v(34.3, -23) * mm});
            skLineSegment(sketch, "E21.6.12.13", {"start": v(34.3, -23) * mm, "end": v(38.3, -23) * mm});
            skLineSegment(sketch, "E21.9.12.13", {"start": v(38.3, -19) * mm, "end": v(38.3, -23) * mm});
            skLineSegment(sketch, "E21.0.12.14", {"start": v(34.3, -25) * mm, "end": v(38.3, -25) * mm});
            skLineSegment(sketch, "E21.3.12.14", {"start": v(34.3, -25) * mm, "end": v(34.3, -29) * mm});
            skLineSegment(sketch, "E21.6.12.14", {"start": v(34.3, -29) * mm, "end": v(38.3, -29) * mm});
            skLineSegment(sketch, "E21.9.12.14", {"start": v(38.3, -25) * mm, "end": v(38.3, -29) * mm});
            skLineSegment(sketch, "E22.0.0.15", {"start": v(-37.7, -31) * mm, "end": v(-33.7, -31) * mm});
            skLineSegment(sketch, "E22.3.0.15", {"start": v(-37.7, -31) * mm, "end": v(-37.7, -35) * mm});
            skLineSegment(sketch, "E22.6.0.15", {"start": v(-37.7, -35) * mm, "end": v(-33.7, -35) * mm});
            skLineSegment(sketch, "E22.9.0.15", {"start": v(-33.7, -31) * mm, "end": v(-33.7, -35) * mm});
            skLineSegment(sketch, "E22.0.0.16", {"start": v(-37.7, -37) * mm, "end": v(-33.7, -37) * mm});
            skLineSegment(sketch, "E22.3.0.16", {"start": v(-37.7, -37) * mm, "end": v(-37.7, -41) * mm});
            skLineSegment(sketch, "E22.6.0.16", {"start": v(-37.7, -41) * mm, "end": v(-33.7, -41) * mm});
            skLineSegment(sketch, "E22.9.0.16", {"start": v(-33.7, -37) * mm, "end": v(-33.7, -41) * mm});
            skLineSegment(sketch, "E22.0.1.15", {"start": v(-31.7, -31) * mm, "end": v(-27.7, -31) * mm});
            skLineSegment(sketch, "E22.3.1.15", {"start": v(-31.7, -31) * mm, "end": v(-31.7, -35) * mm});
            skLineSegment(sketch, "E22.6.1.15", {"start": v(-31.7, -35) * mm, "end": v(-27.7, -35) * mm});
            skLineSegment(sketch, "E22.9.1.15", {"start": v(-27.7, -31) * mm, "end": v(-27.7, -35) * mm});
            skLineSegment(sketch, "E22.0.1.16", {"start": v(-31.7, -37) * mm, "end": v(-27.7, -37) * mm});
            skLineSegment(sketch, "E22.3.1.16", {"start": v(-31.7, -37) * mm, "end": v(-31.7, -41) * mm});
            skLineSegment(sketch, "E22.6.1.16", {"start": v(-31.7, -41) * mm, "end": v(-27.7, -41) * mm});
            skLineSegment(sketch, "E22.9.1.16", {"start": v(-27.7, -37) * mm, "end": v(-27.7, -41) * mm});
            skLineSegment(sketch, "E22.0.2.15", {"start": v(-25.7, -31) * mm, "end": v(-21.7, -31) * mm});
            skLineSegment(sketch, "E22.3.2.15", {"start": v(-25.7, -31) * mm, "end": v(-25.7, -35) * mm});
            skLineSegment(sketch, "E22.6.2.15", {"start": v(-25.7, -35) * mm, "end": v(-21.7, -35) * mm});
            skLineSegment(sketch, "E22.9.2.15", {"start": v(-21.7, -31) * mm, "end": v(-21.7, -35) * mm});
            skLineSegment(sketch, "E22.0.2.16", {"start": v(-25.7, -37) * mm, "end": v(-21.7, -37) * mm});
            skLineSegment(sketch, "E22.3.2.16", {"start": v(-25.7, -37) * mm, "end": v(-25.7, -41) * mm});
            skLineSegment(sketch, "E22.6.2.16", {"start": v(-25.7, -41) * mm, "end": v(-21.7, -41) * mm});
            skLineSegment(sketch, "E22.9.2.16", {"start": v(-21.7, -37) * mm, "end": v(-21.7, -41) * mm});
            skLineSegment(sketch, "E22.0.3.15", {"start": v(-19.7, -31) * mm, "end": v(-15.7, -31) * mm});
            skLineSegment(sketch, "E22.3.3.15", {"start": v(-19.7, -31) * mm, "end": v(-19.7, -35) * mm});
            skLineSegment(sketch, "E22.6.3.15", {"start": v(-19.7, -35) * mm, "end": v(-15.7, -35) * mm});
            skLineSegment(sketch, "E22.9.3.15", {"start": v(-15.7, -31) * mm, "end": v(-15.7, -35) * mm});
            skLineSegment(sketch, "E22.0.3.16", {"start": v(-19.7, -37) * mm, "end": v(-15.7, -37) * mm});
            skLineSegment(sketch, "E22.3.3.16", {"start": v(-19.7, -37) * mm, "end": v(-19.7, -41) * mm});
            skLineSegment(sketch, "E22.6.3.16", {"start": v(-19.7, -41) * mm, "end": v(-15.7, -41) * mm});
            skLineSegment(sketch, "E22.9.3.16", {"start": v(-15.7, -37) * mm, "end": v(-15.7, -41) * mm});
            skLineSegment(sketch, "E22.0.4.15", {"start": v(-13.7, -31) * mm, "end": v(-9.7, -31) * mm});
            skLineSegment(sketch, "E22.3.4.15", {"start": v(-13.7, -31) * mm, "end": v(-13.7, -35) * mm});
            skLineSegment(sketch, "E22.6.4.15", {"start": v(-13.7, -35) * mm, "end": v(-9.7, -35) * mm});
            skLineSegment(sketch, "E22.9.4.15", {"start": v(-9.7, -31) * mm, "end": v(-9.7, -35) * mm});
            skLineSegment(sketch, "E22.0.4.16", {"start": v(-13.7, -37) * mm, "end": v(-9.7, -37) * mm});
            skLineSegment(sketch, "E22.3.4.16", {"start": v(-13.7, -37) * mm, "end": v(-13.7, -41) * mm});
            skLineSegment(sketch, "E22.6.4.16", {"start": v(-13.7, -41) * mm, "end": v(-9.7, -41) * mm});
            skLineSegment(sketch, "E22.9.4.16", {"start": v(-9.7, -37) * mm, "end": v(-9.7, -41) * mm});
            skLineSegment(sketch, "E22.0.5.15", {"start": v(-7.7, -31) * mm, "end": v(-3.7, -31) * mm});
            skLineSegment(sketch, "E22.3.5.15", {"start": v(-7.7, -31) * mm, "end": v(-7.7, -35) * mm});
            skLineSegment(sketch, "E22.6.5.15", {"start": v(-7.7, -35) * mm, "end": v(-3.7, -35) * mm});
            skLineSegment(sketch, "E22.9.5.15", {"start": v(-3.7, -31) * mm, "end": v(-3.7, -35) * mm});
            skLineSegment(sketch, "E22.0.5.16", {"start": v(-7.7, -37) * mm, "end": v(-3.7, -37) * mm});
            skLineSegment(sketch, "E22.3.5.16", {"start": v(-7.7, -37) * mm, "end": v(-7.7, -41) * mm});
            skLineSegment(sketch, "E22.6.5.16", {"start": v(-7.7, -41) * mm, "end": v(-3.7, -41) * mm});
            skLineSegment(sketch, "E22.9.5.16", {"start": v(-3.7, -37) * mm, "end": v(-3.7, -41) * mm});
            skLineSegment(sketch, "E22.0.6.15", {"start": v(-1.7, -31) * mm, "end": v(2.3, -31) * mm});
            skLineSegment(sketch, "E22.3.6.15", {"start": v(-1.7, -31) * mm, "end": v(-1.7, -35) * mm});
            skLineSegment(sketch, "E22.6.6.15", {"start": v(-1.7, -35) * mm, "end": v(2.3, -35) * mm});
            skLineSegment(sketch, "E22.9.6.15", {"start": v(2.3, -31) * mm, "end": v(2.3, -35) * mm});
            skLineSegment(sketch, "E22.0.6.16", {"start": v(-1.7, -37) * mm, "end": v(2.3, -37) * mm});
            skLineSegment(sketch, "E22.3.6.16", {"start": v(-1.7, -37) * mm, "end": v(-1.7, -41) * mm});
            skLineSegment(sketch, "E22.6.6.16", {"start": v(-1.7, -41) * mm, "end": v(2.3, -41) * mm});
            skLineSegment(sketch, "E22.9.6.16", {"start": v(2.3, -37) * mm, "end": v(2.3, -41) * mm});
            skLineSegment(sketch, "E22.0.7.15", {"start": v(4.3, -31) * mm, "end": v(8.3, -31) * mm});
            skLineSegment(sketch, "E22.3.7.15", {"start": v(4.3, -31) * mm, "end": v(4.3, -35) * mm});
            skLineSegment(sketch, "E22.6.7.15", {"start": v(4.3, -35) * mm, "end": v(8.3, -35) * mm});
            skLineSegment(sketch, "E22.9.7.15", {"start": v(8.3, -31) * mm, "end": v(8.3, -35) * mm});
            skLineSegment(sketch, "E22.0.7.16", {"start": v(4.3, -37) * mm, "end": v(8.3, -37) * mm});
            skLineSegment(sketch, "E22.3.7.16", {"start": v(4.3, -37) * mm, "end": v(4.3, -41) * mm});
            skLineSegment(sketch, "E22.6.7.16", {"start": v(4.3, -41) * mm, "end": v(8.3, -41) * mm});
            skLineSegment(sketch, "E22.9.7.16", {"start": v(8.3, -37) * mm, "end": v(8.3, -41) * mm});
            skLineSegment(sketch, "E22.0.8.15", {"start": v(10.3, -31) * mm, "end": v(14.3, -31) * mm});
            skLineSegment(sketch, "E22.3.8.15", {"start": v(10.3, -31) * mm, "end": v(10.3, -35) * mm});
            skLineSegment(sketch, "E22.6.8.15", {"start": v(10.3, -35) * mm, "end": v(14.3, -35) * mm});
            skLineSegment(sketch, "E22.9.8.15", {"start": v(14.3, -31) * mm, "end": v(14.3, -35) * mm});
            skLineSegment(sketch, "E22.0.8.16", {"start": v(10.3, -37) * mm, "end": v(14.3, -37) * mm});
            skLineSegment(sketch, "E22.3.8.16", {"start": v(10.3, -37) * mm, "end": v(10.3, -41) * mm});
            skLineSegment(sketch, "E22.6.8.16", {"start": v(10.3, -41) * mm, "end": v(14.3, -41) * mm});
            skLineSegment(sketch, "E22.9.8.16", {"start": v(14.3, -37) * mm, "end": v(14.3, -41) * mm});
            skLineSegment(sketch, "E22.0.9.15", {"start": v(16.3, -31) * mm, "end": v(20.3, -31) * mm});
            skLineSegment(sketch, "E22.3.9.15", {"start": v(16.3, -31) * mm, "end": v(16.3, -35) * mm});
            skLineSegment(sketch, "E22.6.9.15", {"start": v(16.3, -35) * mm, "end": v(20.3, -35) * mm});
            skLineSegment(sketch, "E22.9.9.15", {"start": v(20.3, -31) * mm, "end": v(20.3, -35) * mm});
            skLineSegment(sketch, "E22.0.9.16", {"start": v(16.3, -37) * mm, "end": v(20.3, -37) * mm});
            skLineSegment(sketch, "E22.3.9.16", {"start": v(16.3, -37) * mm, "end": v(16.3, -41) * mm});
            skLineSegment(sketch, "E22.6.9.16", {"start": v(16.3, -41) * mm, "end": v(20.3, -41) * mm});
            skLineSegment(sketch, "E22.9.9.16", {"start": v(20.3, -37) * mm, "end": v(20.3, -41) * mm});
            skLineSegment(sketch, "E22.0.10.15", {"start": v(22.3, -31) * mm, "end": v(26.3, -31) * mm});
            skLineSegment(sketch, "E22.3.10.15", {"start": v(22.3, -31) * mm, "end": v(22.3, -35) * mm});
            skLineSegment(sketch, "E22.6.10.15", {"start": v(22.3, -35) * mm, "end": v(26.3, -35) * mm});
            skLineSegment(sketch, "E22.9.10.15", {"start": v(26.3, -31) * mm, "end": v(26.3, -35) * mm});
            skLineSegment(sketch, "E22.0.10.16", {"start": v(22.3, -37) * mm, "end": v(26.3, -37) * mm});
            skLineSegment(sketch, "E22.3.10.16", {"start": v(22.3, -37) * mm, "end": v(22.3, -41) * mm});
            skLineSegment(sketch, "E22.6.10.16", {"start": v(22.3, -41) * mm, "end": v(26.3, -41) * mm});
            skLineSegment(sketch, "E22.9.10.16", {"start": v(26.3, -37) * mm, "end": v(26.3, -41) * mm});
            skLineSegment(sketch, "E22.0.11.15", {"start": v(28.3, -31) * mm, "end": v(32.3, -31) * mm});
            skLineSegment(sketch, "E22.3.11.15", {"start": v(28.3, -31) * mm, "end": v(28.3, -35) * mm});
            skLineSegment(sketch, "E22.6.11.15", {"start": v(28.3, -35) * mm, "end": v(32.3, -35) * mm});
            skLineSegment(sketch, "E22.9.11.15", {"start": v(32.3, -31) * mm, "end": v(32.3, -35) * mm});
            skLineSegment(sketch, "E22.0.11.16", {"start": v(28.3, -37) * mm, "end": v(32.3, -37) * mm});
            skLineSegment(sketch, "E22.3.11.16", {"start": v(28.3, -37) * mm, "end": v(28.3, -41) * mm});
            skLineSegment(sketch, "E22.6.11.16", {"start": v(28.3, -41) * mm, "end": v(32.3, -41) * mm});
            skLineSegment(sketch, "E22.9.11.16", {"start": v(32.3, -37) * mm, "end": v(32.3, -41) * mm});
            skLineSegment(sketch, "E22.0.12.15", {"start": v(34.3, -31) * mm, "end": v(38.3, -31) * mm});
            skLineSegment(sketch, "E22.3.12.15", {"start": v(34.3, -31) * mm, "end": v(34.3, -35) * mm});
            skLineSegment(sketch, "E22.6.12.15", {"start": v(34.3, -35) * mm, "end": v(38.3, -35) * mm});
            skLineSegment(sketch, "E22.9.12.15", {"start": v(38.3, -31) * mm, "end": v(38.3, -35) * mm});
            skLineSegment(sketch, "E22.0.12.16", {"start": v(34.3, -37) * mm, "end": v(38.3, -37) * mm});
            skLineSegment(sketch, "E22.3.12.16", {"start": v(34.3, -37) * mm, "end": v(34.3, -41) * mm});
            skLineSegment(sketch, "E22.6.12.16", {"start": v(34.3, -41) * mm, "end": v(38.3, -41) * mm});
            skLineSegment(sketch, "E22.9.12.16", {"start": v(38.3, -37) * mm, "end": v(38.3, -41) * mm});
            skLineSegment(sketch, "E23.0.0.17", {"start": v(-37.7, -43) * mm, "end": v(-33.7, -43) * mm});
            skLineSegment(sketch, "E23.3.0.17", {"start": v(-37.7, -43) * mm, "end": v(-37.7, -47) * mm});
            skLineSegment(sketch, "E23.6.0.17", {"start": v(-37.7, -47) * mm, "end": v(-33.7, -47) * mm});
            skLineSegment(sketch, "E23.9.0.17", {"start": v(-33.7, -43) * mm, "end": v(-33.7, -47) * mm});
            skLineSegment(sketch, "E23.0.0.18", {"start": v(-37.7, -49) * mm, "end": v(-33.7, -49) * mm});
            skLineSegment(sketch, "E23.3.0.18", {"start": v(-37.7, -49) * mm, "end": v(-37.7, -53) * mm});
            skLineSegment(sketch, "E23.6.0.18", {"start": v(-37.7, -53) * mm, "end": v(-33.7, -53) * mm});
            skLineSegment(sketch, "E23.9.0.18", {"start": v(-33.7, -49) * mm, "end": v(-33.7, -53) * mm});
            skLineSegment(sketch, "E23.0.0.19", {"start": v(-37.7, -55) * mm, "end": v(-33.7, -55) * mm});
            skLineSegment(sketch, "E23.3.0.19", {"start": v(-37.7, -55) * mm, "end": v(-37.7, -59) * mm});
            skLineSegment(sketch, "E23.6.0.19", {"start": v(-37.7, -59) * mm, "end": v(-33.7, -59) * mm});
            skLineSegment(sketch, "E23.9.0.19", {"start": v(-33.7, -55) * mm, "end": v(-33.7, -59) * mm});
            skLineSegment(sketch, "E23.0.0.20", {"start": v(-37.7, -61) * mm, "end": v(-33.7, -61) * mm});
            skLineSegment(sketch, "E23.3.0.20", {"start": v(-37.7, -61) * mm, "end": v(-37.7, -65) * mm});
            skLineSegment(sketch, "E23.6.0.20", {"start": v(-37.7, -65) * mm, "end": v(-33.7, -65) * mm});
            skLineSegment(sketch, "E23.9.0.20", {"start": v(-33.7, -61) * mm, "end": v(-33.7, -65) * mm});
            skLineSegment(sketch, "E23.0.0.21", {"start": v(-37.7, -67) * mm, "end": v(-33.7, -67) * mm});
            skLineSegment(sketch, "E23.3.0.21", {"start": v(-37.7, -67) * mm, "end": v(-37.7, -71) * mm});
            skLineSegment(sketch, "E23.6.0.21", {"start": v(-37.7, -71) * mm, "end": v(-33.7, -71) * mm});
            skLineSegment(sketch, "E23.9.0.21", {"start": v(-33.7, -67) * mm, "end": v(-33.7, -71) * mm});
            skLineSegment(sketch, "E23.0.0.22", {"start": v(-37.7, -73) * mm, "end": v(-33.7, -73) * mm});
            skLineSegment(sketch, "E23.3.0.22", {"start": v(-37.7, -73) * mm, "end": v(-37.7, -77) * mm});
            skLineSegment(sketch, "E23.6.0.22", {"start": v(-37.7, -77) * mm, "end": v(-33.7, -77) * mm});
            skLineSegment(sketch, "E23.9.0.22", {"start": v(-33.7, -73) * mm, "end": v(-33.7, -77) * mm});
            skLineSegment(sketch, "E23.0.1.17", {"start": v(-31.7, -43) * mm, "end": v(-27.7, -43) * mm});
            skLineSegment(sketch, "E23.3.1.17", {"start": v(-31.7, -43) * mm, "end": v(-31.7, -47) * mm});
            skLineSegment(sketch, "E23.6.1.17", {"start": v(-31.7, -47) * mm, "end": v(-27.7, -47) * mm});
            skLineSegment(sketch, "E23.9.1.17", {"start": v(-27.7, -43) * mm, "end": v(-27.7, -47) * mm});
            skLineSegment(sketch, "E23.0.1.18", {"start": v(-31.7, -49) * mm, "end": v(-27.7, -49) * mm});
            skLineSegment(sketch, "E23.3.1.18", {"start": v(-31.7, -49) * mm, "end": v(-31.7, -53) * mm});
            skLineSegment(sketch, "E23.6.1.18", {"start": v(-31.7, -53) * mm, "end": v(-27.7, -53) * mm});
            skLineSegment(sketch, "E23.9.1.18", {"start": v(-27.7, -49) * mm, "end": v(-27.7, -53) * mm});
            skLineSegment(sketch, "E23.0.1.19", {"start": v(-31.7, -55) * mm, "end": v(-27.7, -55) * mm});
            skLineSegment(sketch, "E23.3.1.19", {"start": v(-31.7, -55) * mm, "end": v(-31.7, -59) * mm});
            skLineSegment(sketch, "E23.6.1.19", {"start": v(-31.7, -59) * mm, "end": v(-27.7, -59) * mm});
            skLineSegment(sketch, "E23.9.1.19", {"start": v(-27.7, -55) * mm, "end": v(-27.7, -59) * mm});
            skLineSegment(sketch, "E23.0.1.20", {"start": v(-31.7, -61) * mm, "end": v(-27.7, -61) * mm});
            skLineSegment(sketch, "E23.3.1.20", {"start": v(-31.7, -61) * mm, "end": v(-31.7, -65) * mm});
            skLineSegment(sketch, "E23.6.1.20", {"start": v(-31.7, -65) * mm, "end": v(-27.7, -65) * mm});
            skLineSegment(sketch, "E23.9.1.20", {"start": v(-27.7, -61) * mm, "end": v(-27.7, -65) * mm});
            skLineSegment(sketch, "E23.0.1.21", {"start": v(-31.7, -67) * mm, "end": v(-27.7, -67) * mm});
            skLineSegment(sketch, "E23.3.1.21", {"start": v(-31.7, -67) * mm, "end": v(-31.7, -71) * mm});
            skLineSegment(sketch, "E23.6.1.21", {"start": v(-31.7, -71) * mm, "end": v(-27.7, -71) * mm});
            skLineSegment(sketch, "E23.9.1.21", {"start": v(-27.7, -67) * mm, "end": v(-27.7, -71) * mm});
            skLineSegment(sketch, "E23.0.1.22", {"start": v(-31.7, -73) * mm, "end": v(-27.7, -73) * mm});
            skLineSegment(sketch, "E23.3.1.22", {"start": v(-31.7, -73) * mm, "end": v(-31.7, -77) * mm});
            skLineSegment(sketch, "E23.6.1.22", {"start": v(-31.7, -77) * mm, "end": v(-27.7, -77) * mm});
            skLineSegment(sketch, "E23.9.1.22", {"start": v(-27.7, -73) * mm, "end": v(-27.7, -77) * mm});
            skLineSegment(sketch, "E23.0.2.17", {"start": v(-25.7, -43) * mm, "end": v(-21.7, -43) * mm});
            skLineSegment(sketch, "E23.3.2.17", {"start": v(-25.7, -43) * mm, "end": v(-25.7, -47) * mm});
            skLineSegment(sketch, "E23.6.2.17", {"start": v(-25.7, -47) * mm, "end": v(-21.7, -47) * mm});
            skLineSegment(sketch, "E23.9.2.17", {"start": v(-21.7, -43) * mm, "end": v(-21.7, -47) * mm});
            skLineSegment(sketch, "E23.0.2.18", {"start": v(-25.7, -49) * mm, "end": v(-21.7, -49) * mm});
            skLineSegment(sketch, "E23.3.2.18", {"start": v(-25.7, -49) * mm, "end": v(-25.7, -53) * mm});
            skLineSegment(sketch, "E23.6.2.18", {"start": v(-25.7, -53) * mm, "end": v(-21.7, -53) * mm});
            skLineSegment(sketch, "E23.9.2.18", {"start": v(-21.7, -49) * mm, "end": v(-21.7, -53) * mm});
            skLineSegment(sketch, "E23.0.2.19", {"start": v(-25.7, -55) * mm, "end": v(-21.7, -55) * mm});
            skLineSegment(sketch, "E23.3.2.19", {"start": v(-25.7, -55) * mm, "end": v(-25.7, -59) * mm});
            skLineSegment(sketch, "E23.6.2.19", {"start": v(-25.7, -59) * mm, "end": v(-21.7, -59) * mm});
            skLineSegment(sketch, "E23.9.2.19", {"start": v(-21.7, -55) * mm, "end": v(-21.7, -59) * mm});
            skLineSegment(sketch, "E23.0.2.20", {"start": v(-25.7, -61) * mm, "end": v(-21.7, -61) * mm});
            skLineSegment(sketch, "E23.3.2.20", {"start": v(-25.7, -61) * mm, "end": v(-25.7, -65) * mm});
            skLineSegment(sketch, "E23.6.2.20", {"start": v(-25.7, -65) * mm, "end": v(-21.7, -65) * mm});
            skLineSegment(sketch, "E23.9.2.20", {"start": v(-21.7, -61) * mm, "end": v(-21.7, -65) * mm});
            skLineSegment(sketch, "E23.0.2.21", {"start": v(-25.7, -67) * mm, "end": v(-21.7, -67) * mm});
            skLineSegment(sketch, "E23.3.2.21", {"start": v(-25.7, -67) * mm, "end": v(-25.7, -71) * mm});
            skLineSegment(sketch, "E23.6.2.21", {"start": v(-25.7, -71) * mm, "end": v(-21.7, -71) * mm});
            skLineSegment(sketch, "E23.9.2.21", {"start": v(-21.7, -67) * mm, "end": v(-21.7, -71) * mm});
            skLineSegment(sketch, "E23.0.2.22", {"start": v(-25.7, -73) * mm, "end": v(-21.7, -73) * mm});
            skLineSegment(sketch, "E23.3.2.22", {"start": v(-25.7, -73) * mm, "end": v(-25.7, -77) * mm});
            skLineSegment(sketch, "E23.6.2.22", {"start": v(-25.7, -77) * mm, "end": v(-21.7, -77) * mm});
            skLineSegment(sketch, "E23.9.2.22", {"start": v(-21.7, -73) * mm, "end": v(-21.7, -77) * mm});
            skLineSegment(sketch, "E23.0.3.17", {"start": v(-19.7, -43) * mm, "end": v(-15.7, -43) * mm});
            skLineSegment(sketch, "E23.3.3.17", {"start": v(-19.7, -43) * mm, "end": v(-19.7, -47) * mm});
            skLineSegment(sketch, "E23.6.3.17", {"start": v(-19.7, -47) * mm, "end": v(-15.7, -47) * mm});
            skLineSegment(sketch, "E23.9.3.17", {"start": v(-15.7, -43) * mm, "end": v(-15.7, -47) * mm});
            skLineSegment(sketch, "E23.0.3.18", {"start": v(-19.7, -49) * mm, "end": v(-15.7, -49) * mm});
            skLineSegment(sketch, "E23.3.3.18", {"start": v(-19.7, -49) * mm, "end": v(-19.7, -53) * mm});
            skLineSegment(sketch, "E23.6.3.18", {"start": v(-19.7, -53) * mm, "end": v(-15.7, -53) * mm});
            skLineSegment(sketch, "E23.9.3.18", {"start": v(-15.7, -49) * mm, "end": v(-15.7, -53) * mm});
            skLineSegment(sketch, "E23.0.3.19", {"start": v(-19.7, -55) * mm, "end": v(-15.7, -55) * mm});
            skLineSegment(sketch, "E23.3.3.19", {"start": v(-19.7, -55) * mm, "end": v(-19.7, -59) * mm});
            skLineSegment(sketch, "E23.6.3.19", {"start": v(-19.7, -59) * mm, "end": v(-15.7, -59) * mm});
            skLineSegment(sketch, "E23.9.3.19", {"start": v(-15.7, -55) * mm, "end": v(-15.7, -59) * mm});
            skLineSegment(sketch, "E23.0.3.20", {"start": v(-19.7, -61) * mm, "end": v(-15.7, -61) * mm});
            skLineSegment(sketch, "E23.3.3.20", {"start": v(-19.7, -61) * mm, "end": v(-19.7, -65) * mm});
            skLineSegment(sketch, "E23.6.3.20", {"start": v(-19.7, -65) * mm, "end": v(-15.7, -65) * mm});
            skLineSegment(sketch, "E23.9.3.20", {"start": v(-15.7, -61) * mm, "end": v(-15.7, -65) * mm});
            skLineSegment(sketch, "E23.0.3.21", {"start": v(-19.7, -67) * mm, "end": v(-15.7, -67) * mm});
            skLineSegment(sketch, "E23.3.3.21", {"start": v(-19.7, -67) * mm, "end": v(-19.7, -71) * mm});
            skLineSegment(sketch, "E23.6.3.21", {"start": v(-19.7, -71) * mm, "end": v(-15.7, -71) * mm});
            skLineSegment(sketch, "E23.9.3.21", {"start": v(-15.7, -67) * mm, "end": v(-15.7, -71) * mm});
            skLineSegment(sketch, "E23.0.3.22", {"start": v(-19.7, -73) * mm, "end": v(-15.7, -73) * mm});
            skLineSegment(sketch, "E23.3.3.22", {"start": v(-19.7, -73) * mm, "end": v(-19.7, -77) * mm});
            skLineSegment(sketch, "E23.6.3.22", {"start": v(-19.7, -77) * mm, "end": v(-15.7, -77) * mm});
            skLineSegment(sketch, "E23.9.3.22", {"start": v(-15.7, -73) * mm, "end": v(-15.7, -77) * mm});
            skLineSegment(sketch, "E23.0.4.17", {"start": v(-13.7, -43) * mm, "end": v(-9.7, -43) * mm});
            skLineSegment(sketch, "E23.3.4.17", {"start": v(-13.7, -43) * mm, "end": v(-13.7, -47) * mm});
            skLineSegment(sketch, "E23.6.4.17", {"start": v(-13.7, -47) * mm, "end": v(-9.7, -47) * mm});
            skLineSegment(sketch, "E23.9.4.17", {"start": v(-9.7, -43) * mm, "end": v(-9.7, -47) * mm});
            skLineSegment(sketch, "E23.0.4.18", {"start": v(-13.7, -49) * mm, "end": v(-9.7, -49) * mm});
            skLineSegment(sketch, "E23.3.4.18", {"start": v(-13.7, -49) * mm, "end": v(-13.7, -53) * mm});
            skLineSegment(sketch, "E23.6.4.18", {"start": v(-13.7, -53) * mm, "end": v(-9.7, -53) * mm});
            skLineSegment(sketch, "E23.9.4.18", {"start": v(-9.7, -49) * mm, "end": v(-9.7, -53) * mm});
            skLineSegment(sketch, "E23.0.4.19", {"start": v(-13.7, -55) * mm, "end": v(-9.7, -55) * mm});
            skLineSegment(sketch, "E23.3.4.19", {"start": v(-13.7, -55) * mm, "end": v(-13.7, -59) * mm});
            skLineSegment(sketch, "E23.6.4.19", {"start": v(-13.7, -59) * mm, "end": v(-9.7, -59) * mm});
            skLineSegment(sketch, "E23.9.4.19", {"start": v(-9.7, -55) * mm, "end": v(-9.7, -59) * mm});
            skLineSegment(sketch, "E23.0.4.20", {"start": v(-13.7, -61) * mm, "end": v(-9.7, -61) * mm});
            skLineSegment(sketch, "E23.3.4.20", {"start": v(-13.7, -61) * mm, "end": v(-13.7, -65) * mm});
            skLineSegment(sketch, "E23.6.4.20", {"start": v(-13.7, -65) * mm, "end": v(-9.7, -65) * mm});
            skLineSegment(sketch, "E23.9.4.20", {"start": v(-9.7, -61) * mm, "end": v(-9.7, -65) * mm});
            skLineSegment(sketch, "E23.0.4.21", {"start": v(-13.7, -67) * mm, "end": v(-9.7, -67) * mm});
            skLineSegment(sketch, "E23.3.4.21", {"start": v(-13.7, -67) * mm, "end": v(-13.7, -71) * mm});
            skLineSegment(sketch, "E23.6.4.21", {"start": v(-13.7, -71) * mm, "end": v(-9.7, -71) * mm});
            skLineSegment(sketch, "E23.9.4.21", {"start": v(-9.7, -67) * mm, "end": v(-9.7, -71) * mm});
            skLineSegment(sketch, "E23.0.4.22", {"start": v(-13.7, -73) * mm, "end": v(-9.7, -73) * mm});
            skLineSegment(sketch, "E23.3.4.22", {"start": v(-13.7, -73) * mm, "end": v(-13.7, -77) * mm});
            skLineSegment(sketch, "E23.6.4.22", {"start": v(-13.7, -77) * mm, "end": v(-9.7, -77) * mm});
            skLineSegment(sketch, "E23.9.4.22", {"start": v(-9.7, -73) * mm, "end": v(-9.7, -77) * mm});
            skLineSegment(sketch, "E23.0.5.17", {"start": v(-7.7, -43) * mm, "end": v(-3.7, -43) * mm});
            skLineSegment(sketch, "E23.3.5.17", {"start": v(-7.7, -43) * mm, "end": v(-7.7, -47) * mm});
            skLineSegment(sketch, "E23.6.5.17", {"start": v(-7.7, -47) * mm, "end": v(-3.7, -47) * mm});
            skLineSegment(sketch, "E23.9.5.17", {"start": v(-3.7, -43) * mm, "end": v(-3.7, -47) * mm});
            skLineSegment(sketch, "E23.0.5.18", {"start": v(-7.7, -49) * mm, "end": v(-3.7, -49) * mm});
            skLineSegment(sketch, "E23.3.5.18", {"start": v(-7.7, -49) * mm, "end": v(-7.7, -53) * mm});
            skLineSegment(sketch, "E23.6.5.18", {"start": v(-7.7, -53) * mm, "end": v(-3.7, -53) * mm});
            skLineSegment(sketch, "E23.9.5.18", {"start": v(-3.7, -49) * mm, "end": v(-3.7, -53) * mm});
            skLineSegment(sketch, "E23.0.5.19", {"start": v(-7.7, -55) * mm, "end": v(-3.7, -55) * mm});
            skLineSegment(sketch, "E23.3.5.19", {"start": v(-7.7, -55) * mm, "end": v(-7.7, -59) * mm});
            skLineSegment(sketch, "E23.6.5.19", {"start": v(-7.7, -59) * mm, "end": v(-3.7, -59) * mm});
            skLineSegment(sketch, "E23.9.5.19", {"start": v(-3.7, -55) * mm, "end": v(-3.7, -59) * mm});
            skLineSegment(sketch, "E23.0.5.20", {"start": v(-7.7, -61) * mm, "end": v(-3.7, -61) * mm});
            skLineSegment(sketch, "E23.3.5.20", {"start": v(-7.7, -61) * mm, "end": v(-7.7, -65) * mm});
            skLineSegment(sketch, "E23.6.5.20", {"start": v(-7.7, -65) * mm, "end": v(-3.7, -65) * mm});
            skLineSegment(sketch, "E23.9.5.20", {"start": v(-3.7, -61) * mm, "end": v(-3.7, -65) * mm});
            skLineSegment(sketch, "E23.0.5.21", {"start": v(-7.7, -67) * mm, "end": v(-3.7, -67) * mm});
            skLineSegment(sketch, "E23.3.5.21", {"start": v(-7.7, -67) * mm, "end": v(-7.7, -71) * mm});
            skLineSegment(sketch, "E23.6.5.21", {"start": v(-7.7, -71) * mm, "end": v(-3.7, -71) * mm});
            skLineSegment(sketch, "E23.9.5.21", {"start": v(-3.7, -67) * mm, "end": v(-3.7, -71) * mm});
            skLineSegment(sketch, "E23.0.5.22", {"start": v(-7.7, -73) * mm, "end": v(-3.7, -73) * mm});
            skLineSegment(sketch, "E23.3.5.22", {"start": v(-7.7, -73) * mm, "end": v(-7.7, -77) * mm});
            skLineSegment(sketch, "E23.6.5.22", {"start": v(-7.7, -77) * mm, "end": v(-3.7, -77) * mm});
            skLineSegment(sketch, "E23.9.5.22", {"start": v(-3.7, -73) * mm, "end": v(-3.7, -77) * mm});
            skLineSegment(sketch, "E23.0.6.17", {"start": v(-1.7, -43) * mm, "end": v(2.3, -43) * mm});
            skLineSegment(sketch, "E23.3.6.17", {"start": v(-1.7, -43) * mm, "end": v(-1.7, -47) * mm});
            skLineSegment(sketch, "E23.6.6.17", {"start": v(-1.7, -47) * mm, "end": v(2.3, -47) * mm});
            skLineSegment(sketch, "E23.9.6.17", {"start": v(2.3, -43) * mm, "end": v(2.3, -47) * mm});
            skLineSegment(sketch, "E23.0.6.18", {"start": v(-1.7, -49) * mm, "end": v(2.3, -49) * mm});
            skLineSegment(sketch, "E23.3.6.18", {"start": v(-1.7, -49) * mm, "end": v(-1.7, -53) * mm});
            skLineSegment(sketch, "E23.6.6.18", {"start": v(-1.7, -53) * mm, "end": v(2.3, -53) * mm});
            skLineSegment(sketch, "E23.9.6.18", {"start": v(2.3, -49) * mm, "end": v(2.3, -53) * mm});
            skLineSegment(sketch, "E23.0.6.19", {"start": v(-1.7, -55) * mm, "end": v(2.3, -55) * mm});
            skLineSegment(sketch, "E23.3.6.19", {"start": v(-1.7, -55) * mm, "end": v(-1.7, -59) * mm});
            skLineSegment(sketch, "E23.6.6.19", {"start": v(-1.7, -59) * mm, "end": v(2.3, -59) * mm});
            skLineSegment(sketch, "E23.9.6.19", {"start": v(2.3, -55) * mm, "end": v(2.3, -59) * mm});
            skLineSegment(sketch, "E23.0.6.20", {"start": v(-1.7, -61) * mm, "end": v(2.3, -61) * mm});
            skLineSegment(sketch, "E23.3.6.20", {"start": v(-1.7, -61) * mm, "end": v(-1.7, -65) * mm});
            skLineSegment(sketch, "E23.6.6.20", {"start": v(-1.7, -65) * mm, "end": v(2.3, -65) * mm});
            skLineSegment(sketch, "E23.9.6.20", {"start": v(2.3, -61) * mm, "end": v(2.3, -65) * mm});
            skLineSegment(sketch, "E23.0.6.21", {"start": v(-1.7, -67) * mm, "end": v(2.3, -67) * mm});
            skLineSegment(sketch, "E23.3.6.21", {"start": v(-1.7, -67) * mm, "end": v(-1.7, -71) * mm});
            skLineSegment(sketch, "E23.6.6.21", {"start": v(-1.7, -71) * mm, "end": v(2.3, -71) * mm});
            skLineSegment(sketch, "E23.9.6.21", {"start": v(2.3, -67) * mm, "end": v(2.3, -71) * mm});
            skLineSegment(sketch, "E23.0.6.22", {"start": v(-1.7, -73) * mm, "end": v(2.3, -73) * mm});
            skLineSegment(sketch, "E23.3.6.22", {"start": v(-1.7, -73) * mm, "end": v(-1.7, -77) * mm});
            skLineSegment(sketch, "E23.6.6.22", {"start": v(-1.7, -77) * mm, "end": v(2.3, -77) * mm});
            skLineSegment(sketch, "E23.9.6.22", {"start": v(2.3, -73) * mm, "end": v(2.3, -77) * mm});
            skLineSegment(sketch, "E23.0.7.17", {"start": v(4.3, -43) * mm, "end": v(8.3, -43) * mm});
            skLineSegment(sketch, "E23.3.7.17", {"start": v(4.3, -43) * mm, "end": v(4.3, -47) * mm});
            skLineSegment(sketch, "E23.6.7.17", {"start": v(4.3, -47) * mm, "end": v(8.3, -47) * mm});
            skLineSegment(sketch, "E23.9.7.17", {"start": v(8.3, -43) * mm, "end": v(8.3, -47) * mm});
            skLineSegment(sketch, "E23.0.7.18", {"start": v(4.3, -49) * mm, "end": v(8.3, -49) * mm});
            skLineSegment(sketch, "E23.3.7.18", {"start": v(4.3, -49) * mm, "end": v(4.3, -53) * mm});
            skLineSegment(sketch, "E23.6.7.18", {"start": v(4.3, -53) * mm, "end": v(8.3, -53) * mm});
            skLineSegment(sketch, "E23.9.7.18", {"start": v(8.3, -49) * mm, "end": v(8.3, -53) * mm});
            skLineSegment(sketch, "E23.0.7.19", {"start": v(4.3, -55) * mm, "end": v(8.3, -55) * mm});
            skLineSegment(sketch, "E23.3.7.19", {"start": v(4.3, -55) * mm, "end": v(4.3, -59) * mm});
            skLineSegment(sketch, "E23.6.7.19", {"start": v(4.3, -59) * mm, "end": v(8.3, -59) * mm});
            skLineSegment(sketch, "E23.9.7.19", {"start": v(8.3, -55) * mm, "end": v(8.3, -59) * mm});
            skLineSegment(sketch, "E23.0.7.20", {"start": v(4.3, -61) * mm, "end": v(8.3, -61) * mm});
            skLineSegment(sketch, "E23.3.7.20", {"start": v(4.3, -61) * mm, "end": v(4.3, -65) * mm});
            skLineSegment(sketch, "E23.6.7.20", {"start": v(4.3, -65) * mm, "end": v(8.3, -65) * mm});
            skLineSegment(sketch, "E23.9.7.20", {"start": v(8.3, -61) * mm, "end": v(8.3, -65) * mm});
            skLineSegment(sketch, "E23.0.7.21", {"start": v(4.3, -67) * mm, "end": v(8.3, -67) * mm});
            skLineSegment(sketch, "E23.3.7.21", {"start": v(4.3, -67) * mm, "end": v(4.3, -71) * mm});
            skLineSegment(sketch, "E23.6.7.21", {"start": v(4.3, -71) * mm, "end": v(8.3, -71) * mm});
            skLineSegment(sketch, "E23.9.7.21", {"start": v(8.3, -67) * mm, "end": v(8.3, -71) * mm});
            skLineSegment(sketch, "E23.0.7.22", {"start": v(4.3, -73) * mm, "end": v(8.3, -73) * mm});
            skLineSegment(sketch, "E23.3.7.22", {"start": v(4.3, -73) * mm, "end": v(4.3, -77) * mm});
            skLineSegment(sketch, "E23.6.7.22", {"start": v(4.3, -77) * mm, "end": v(8.3, -77) * mm});
            skLineSegment(sketch, "E23.9.7.22", {"start": v(8.3, -73) * mm, "end": v(8.3, -77) * mm});
            skLineSegment(sketch, "E23.0.8.17", {"start": v(10.3, -43) * mm, "end": v(14.3, -43) * mm});
            skLineSegment(sketch, "E23.3.8.17", {"start": v(10.3, -43) * mm, "end": v(10.3, -47) * mm});
            skLineSegment(sketch, "E23.6.8.17", {"start": v(10.3, -47) * mm, "end": v(14.3, -47) * mm});
            skLineSegment(sketch, "E23.9.8.17", {"start": v(14.3, -43) * mm, "end": v(14.3, -47) * mm});
            skLineSegment(sketch, "E23.0.8.18", {"start": v(10.3, -49) * mm, "end": v(14.3, -49) * mm});
            skLineSegment(sketch, "E23.3.8.18", {"start": v(10.3, -49) * mm, "end": v(10.3, -53) * mm});
            skLineSegment(sketch, "E23.6.8.18", {"start": v(10.3, -53) * mm, "end": v(14.3, -53) * mm});
            skLineSegment(sketch, "E23.9.8.18", {"start": v(14.3, -49) * mm, "end": v(14.3, -53) * mm});
            skLineSegment(sketch, "E23.0.8.19", {"start": v(10.3, -55) * mm, "end": v(14.3, -55) * mm});
            skLineSegment(sketch, "E23.3.8.19", {"start": v(10.3, -55) * mm, "end": v(10.3, -59) * mm});
            skLineSegment(sketch, "E23.6.8.19", {"start": v(10.3, -59) * mm, "end": v(14.3, -59) * mm});
            skLineSegment(sketch, "E23.9.8.19", {"start": v(14.3, -55) * mm, "end": v(14.3, -59) * mm});
            skLineSegment(sketch, "E23.0.8.20", {"start": v(10.3, -61) * mm, "end": v(14.3, -61) * mm});
            skLineSegment(sketch, "E23.3.8.20", {"start": v(10.3, -61) * mm, "end": v(10.3, -65) * mm});
            skLineSegment(sketch, "E23.6.8.20", {"start": v(10.3, -65) * mm, "end": v(14.3, -65) * mm});
            skLineSegment(sketch, "E23.9.8.20", {"start": v(14.3, -61) * mm, "end": v(14.3, -65) * mm});
            skLineSegment(sketch, "E23.0.8.21", {"start": v(10.3, -67) * mm, "end": v(14.3, -67) * mm});
            skLineSegment(sketch, "E23.3.8.21", {"start": v(10.3, -67) * mm, "end": v(10.3, -71) * mm});
            skLineSegment(sketch, "E23.6.8.21", {"start": v(10.3, -71) * mm, "end": v(14.3, -71) * mm});
            skLineSegment(sketch, "E23.9.8.21", {"start": v(14.3, -67) * mm, "end": v(14.3, -71) * mm});
            skLineSegment(sketch, "E23.0.8.22", {"start": v(10.3, -73) * mm, "end": v(14.3, -73) * mm});
            skLineSegment(sketch, "E23.3.8.22", {"start": v(10.3, -73) * mm, "end": v(10.3, -77) * mm});
            skLineSegment(sketch, "E23.6.8.22", {"start": v(10.3, -77) * mm, "end": v(14.3, -77) * mm});
            skLineSegment(sketch, "E23.9.8.22", {"start": v(14.3, -73) * mm, "end": v(14.3, -77) * mm});
            skLineSegment(sketch, "E23.0.9.17", {"start": v(16.3, -43) * mm, "end": v(20.3, -43) * mm});
            skLineSegment(sketch, "E23.3.9.17", {"start": v(16.3, -43) * mm, "end": v(16.3, -47) * mm});
            skLineSegment(sketch, "E23.6.9.17", {"start": v(16.3, -47) * mm, "end": v(20.3, -47) * mm});
            skLineSegment(sketch, "E23.9.9.17", {"start": v(20.3, -43) * mm, "end": v(20.3, -47) * mm});
            skLineSegment(sketch, "E23.0.9.18", {"start": v(16.3, -49) * mm, "end": v(20.3, -49) * mm});
            skLineSegment(sketch, "E23.3.9.18", {"start": v(16.3, -49) * mm, "end": v(16.3, -53) * mm});
            skLineSegment(sketch, "E23.6.9.18", {"start": v(16.3, -53) * mm, "end": v(20.3, -53) * mm});
            skLineSegment(sketch, "E23.9.9.18", {"start": v(20.3, -49) * mm, "end": v(20.3, -53) * mm});
            skLineSegment(sketch, "E23.0.9.19", {"start": v(16.3, -55) * mm, "end": v(20.3, -55) * mm});
            skLineSegment(sketch, "E23.3.9.19", {"start": v(16.3, -55) * mm, "end": v(16.3, -59) * mm});
            skLineSegment(sketch, "E23.6.9.19", {"start": v(16.3, -59) * mm, "end": v(20.3, -59) * mm});
            skLineSegment(sketch, "E23.9.9.19", {"start": v(20.3, -55) * mm, "end": v(20.3, -59) * mm});
            skLineSegment(sketch, "E23.0.9.20", {"start": v(16.3, -61) * mm, "end": v(20.3, -61) * mm});
            skLineSegment(sketch, "E23.3.9.20", {"start": v(16.3, -61) * mm, "end": v(16.3, -65) * mm});
            skLineSegment(sketch, "E23.6.9.20", {"start": v(16.3, -65) * mm, "end": v(20.3, -65) * mm});
            skLineSegment(sketch, "E23.9.9.20", {"start": v(20.3, -61) * mm, "end": v(20.3, -65) * mm});
            skLineSegment(sketch, "E23.0.9.21", {"start": v(16.3, -67) * mm, "end": v(20.3, -67) * mm});
            skLineSegment(sketch, "E23.3.9.21", {"start": v(16.3, -67) * mm, "end": v(16.3, -71) * mm});
            skLineSegment(sketch, "E23.6.9.21", {"start": v(16.3, -71) * mm, "end": v(20.3, -71) * mm});
            skLineSegment(sketch, "E23.9.9.21", {"start": v(20.3, -67) * mm, "end": v(20.3, -71) * mm});
            skLineSegment(sketch, "E23.0.9.22", {"start": v(16.3, -73) * mm, "end": v(20.3, -73) * mm});
            skLineSegment(sketch, "E23.3.9.22", {"start": v(16.3, -73) * mm, "end": v(16.3, -77) * mm});
            skLineSegment(sketch, "E23.6.9.22", {"start": v(16.3, -77) * mm, "end": v(20.3, -77) * mm});
            skLineSegment(sketch, "E23.9.9.22", {"start": v(20.3, -73) * mm, "end": v(20.3, -77) * mm});
            skLineSegment(sketch, "E23.0.10.17", {"start": v(22.3, -43) * mm, "end": v(26.3, -43) * mm});
            skLineSegment(sketch, "E23.3.10.17", {"start": v(22.3, -43) * mm, "end": v(22.3, -47) * mm});
            skLineSegment(sketch, "E23.6.10.17", {"start": v(22.3, -47) * mm, "end": v(26.3, -47) * mm});
            skLineSegment(sketch, "E23.9.10.17", {"start": v(26.3, -43) * mm, "end": v(26.3, -47) * mm});
            skLineSegment(sketch, "E23.0.10.18", {"start": v(22.3, -49) * mm, "end": v(26.3, -49) * mm});
            skLineSegment(sketch, "E23.3.10.18", {"start": v(22.3, -49) * mm, "end": v(22.3, -53) * mm});
            skLineSegment(sketch, "E23.6.10.18", {"start": v(22.3, -53) * mm, "end": v(26.3, -53) * mm});
            skLineSegment(sketch, "E23.9.10.18", {"start": v(26.3, -49) * mm, "end": v(26.3, -53) * mm});
            skLineSegment(sketch, "E23.0.10.19", {"start": v(22.3, -55) * mm, "end": v(26.3, -55) * mm});
            skLineSegment(sketch, "E23.3.10.19", {"start": v(22.3, -55) * mm, "end": v(22.3, -59) * mm});
            skLineSegment(sketch, "E23.6.10.19", {"start": v(22.3, -59) * mm, "end": v(26.3, -59) * mm});
            skLineSegment(sketch, "E23.9.10.19", {"start": v(26.3, -55) * mm, "end": v(26.3, -59) * mm});
            skLineSegment(sketch, "E23.0.10.20", {"start": v(22.3, -61) * mm, "end": v(26.3, -61) * mm});
            skLineSegment(sketch, "E23.3.10.20", {"start": v(22.3, -61) * mm, "end": v(22.3, -65) * mm});
            skLineSegment(sketch, "E23.6.10.20", {"start": v(22.3, -65) * mm, "end": v(26.3, -65) * mm});
            skLineSegment(sketch, "E23.9.10.20", {"start": v(26.3, -61) * mm, "end": v(26.3, -65) * mm});
            skLineSegment(sketch, "E23.0.10.21", {"start": v(22.3, -67) * mm, "end": v(26.3, -67) * mm});
            skLineSegment(sketch, "E23.3.10.21", {"start": v(22.3, -67) * mm, "end": v(22.3, -71) * mm});
            skLineSegment(sketch, "E23.6.10.21", {"start": v(22.3, -71) * mm, "end": v(26.3, -71) * mm});
            skLineSegment(sketch, "E23.9.10.21", {"start": v(26.3, -67) * mm, "end": v(26.3, -71) * mm});
            skLineSegment(sketch, "E23.0.10.22", {"start": v(22.3, -73) * mm, "end": v(26.3, -73) * mm});
            skLineSegment(sketch, "E23.3.10.22", {"start": v(22.3, -73) * mm, "end": v(22.3, -77) * mm});
            skLineSegment(sketch, "E23.6.10.22", {"start": v(22.3, -77) * mm, "end": v(26.3, -77) * mm});
            skLineSegment(sketch, "E23.9.10.22", {"start": v(26.3, -73) * mm, "end": v(26.3, -77) * mm});
            skLineSegment(sketch, "E23.0.11.17", {"start": v(28.3, -43) * mm, "end": v(32.3, -43) * mm});
            skLineSegment(sketch, "E23.3.11.17", {"start": v(28.3, -43) * mm, "end": v(28.3, -47) * mm});
            skLineSegment(sketch, "E23.6.11.17", {"start": v(28.3, -47) * mm, "end": v(32.3, -47) * mm});
            skLineSegment(sketch, "E23.9.11.17", {"start": v(32.3, -43) * mm, "end": v(32.3, -47) * mm});
            skLineSegment(sketch, "E23.0.11.18", {"start": v(28.3, -49) * mm, "end": v(32.3, -49) * mm});
            skLineSegment(sketch, "E23.3.11.18", {"start": v(28.3, -49) * mm, "end": v(28.3, -53) * mm});
            skLineSegment(sketch, "E23.6.11.18", {"start": v(28.3, -53) * mm, "end": v(32.3, -53) * mm});
            skLineSegment(sketch, "E23.9.11.18", {"start": v(32.3, -49) * mm, "end": v(32.3, -53) * mm});
            skLineSegment(sketch, "E23.0.11.19", {"start": v(28.3, -55) * mm, "end": v(32.3, -55) * mm});
            skLineSegment(sketch, "E23.3.11.19", {"start": v(28.3, -55) * mm, "end": v(28.3, -59) * mm});
            skLineSegment(sketch, "E23.6.11.19", {"start": v(28.3, -59) * mm, "end": v(32.3, -59) * mm});
            skLineSegment(sketch, "E23.9.11.19", {"start": v(32.3, -55) * mm, "end": v(32.3, -59) * mm});
            skLineSegment(sketch, "E23.0.11.20", {"start": v(28.3, -61) * mm, "end": v(32.3, -61) * mm});
            skLineSegment(sketch, "E23.3.11.20", {"start": v(28.3, -61) * mm, "end": v(28.3, -65) * mm});
            skLineSegment(sketch, "E23.6.11.20", {"start": v(28.3, -65) * mm, "end": v(32.3, -65) * mm});
            skLineSegment(sketch, "E23.9.11.20", {"start": v(32.3, -61) * mm, "end": v(32.3, -65) * mm});
            skLineSegment(sketch, "E23.0.11.21", {"start": v(28.3, -67) * mm, "end": v(32.3, -67) * mm});
            skLineSegment(sketch, "E23.3.11.21", {"start": v(28.3, -67) * mm, "end": v(28.3, -71) * mm});
            skLineSegment(sketch, "E23.6.11.21", {"start": v(28.3, -71) * mm, "end": v(32.3, -71) * mm});
            skLineSegment(sketch, "E23.9.11.21", {"start": v(32.3, -67) * mm, "end": v(32.3, -71) * mm});
            skLineSegment(sketch, "E23.0.11.22", {"start": v(28.3, -73) * mm, "end": v(32.3, -73) * mm});
            skLineSegment(sketch, "E23.3.11.22", {"start": v(28.3, -73) * mm, "end": v(28.3, -77) * mm});
            skLineSegment(sketch, "E23.6.11.22", {"start": v(28.3, -77) * mm, "end": v(32.3, -77) * mm});
            skLineSegment(sketch, "E23.9.11.22", {"start": v(32.3, -73) * mm, "end": v(32.3, -77) * mm});
            skLineSegment(sketch, "E23.0.12.17", {"start": v(34.3, -43) * mm, "end": v(38.3, -43) * mm});
            skLineSegment(sketch, "E23.3.12.17", {"start": v(34.3, -43) * mm, "end": v(34.3, -47) * mm});
            skLineSegment(sketch, "E23.6.12.17", {"start": v(34.3, -47) * mm, "end": v(38.3, -47) * mm});
            skLineSegment(sketch, "E23.9.12.17", {"start": v(38.3, -43) * mm, "end": v(38.3, -47) * mm});
            skLineSegment(sketch, "E23.0.12.18", {"start": v(34.3, -49) * mm, "end": v(38.3, -49) * mm});
            skLineSegment(sketch, "E23.3.12.18", {"start": v(34.3, -49) * mm, "end": v(34.3, -53) * mm});
            skLineSegment(sketch, "E23.6.12.18", {"start": v(34.3, -53) * mm, "end": v(38.3, -53) * mm});
            skLineSegment(sketch, "E23.9.12.18", {"start": v(38.3, -49) * mm, "end": v(38.3, -53) * mm});
            skLineSegment(sketch, "E23.0.12.19", {"start": v(34.3, -55) * mm, "end": v(38.3, -55) * mm});
            skLineSegment(sketch, "E23.3.12.19", {"start": v(34.3, -55) * mm, "end": v(34.3, -59) * mm});
            skLineSegment(sketch, "E23.6.12.19", {"start": v(34.3, -59) * mm, "end": v(38.3, -59) * mm});
            skLineSegment(sketch, "E23.9.12.19", {"start": v(38.3, -55) * mm, "end": v(38.3, -59) * mm});
            skLineSegment(sketch, "E23.0.12.20", {"start": v(34.3, -61) * mm, "end": v(38.3, -61) * mm});
            skLineSegment(sketch, "E23.3.12.20", {"start": v(34.3, -61) * mm, "end": v(34.3, -65) * mm});
            skLineSegment(sketch, "E23.6.12.20", {"start": v(34.3, -65) * mm, "end": v(38.3, -65) * mm});
            skLineSegment(sketch, "E23.9.12.20", {"start": v(38.3, -61) * mm, "end": v(38.3, -65) * mm});
            skLineSegment(sketch, "E23.0.12.21", {"start": v(34.3, -67) * mm, "end": v(38.3, -67) * mm});
            skLineSegment(sketch, "E23.3.12.21", {"start": v(34.3, -67) * mm, "end": v(34.3, -71) * mm});
            skLineSegment(sketch, "E23.6.12.21", {"start": v(34.3, -71) * mm, "end": v(38.3, -71) * mm});
            skLineSegment(sketch, "E23.9.12.21", {"start": v(38.3, -67) * mm, "end": v(38.3, -71) * mm});
            skLineSegment(sketch, "E23.0.12.22", {"start": v(34.3, -73) * mm, "end": v(38.3, -73) * mm});
            skLineSegment(sketch, "E23.3.12.22", {"start": v(34.3, -73) * mm, "end": v(34.3, -77) * mm});
            skLineSegment(sketch, "E23.6.12.22", {"start": v(34.3, -77) * mm, "end": v(38.3, -77) * mm});
            skLineSegment(sketch, "E23.9.12.22", {"start": v(38.3, -73) * mm, "end": v(38.3, -77) * mm});
            skSolve(sketch);
        }
        {
            var Q0;
            Q0 = qSketchRegion(id + "F24", true);
            extrude(context, id + "F25", {"entities" : qUnion([Q0]), "operationType" : NewBodyOperationType.REMOVE, "oppositeDirection" : true, "depth" : 3 * mm, "offsetDistance" : 25 * mm});
        }
        {
            var Q0;
            Q0=makeQuery(id+"F1.opExtrude","CAP_FACE",FACE,{"disambiguationData":[OSD([sQuery(id+"F0.wireOp",EDGE,"E0.bottom"),sQuery(id+"F0.wireOp",EDGE,"E0.top"),sQuery(id+"F0.wireOp",EDGE,"E0.left"),sQuery(id+"F0.wireOp",EDGE,"E0.right")])],"isStart":true});
            var sketch = newSketch(context, id + "F26", { "sketchPlane" : qUnion([Q0])});
            skCircle(sketch, "E24", {"center": v(0, 36) * mm, "radius": 19 * mm});
            skCircle(sketch, "E25", {"center": v(-19.7, -23) * mm, "radius": 11.66 * mm});
            skCircle(sketch, "E26", {"center": v(22.3, 3) * mm, "radius": 11.76 * mm});
            skCircle(sketch, "E27", {"center": v(16.3, -45) * mm, "radius": 16.3 * mm});
            skSolve(sketch);
        }
        {
            var Q0;
            Q0 = qSketchRegion(id + "F26", true);
            extrude(context, id + "F27", {"entities" : qUnion([Q0]), "operationType" : NewBodyOperationType.ADD, "oppositeDirection" : true, "depth" : 2 * mm, "offsetDistance" : 25 * mm});
        }
        {
            var Q0;
            Q0=makeQuery(id+"F27.boolean.opBoolean","MERGE",FACE,{"derivedFrom":[makeQuery(id+"F1.opExtrude","CAP_FACE",FACE,{"disambiguationData":[OSD([sQuery(id+"F0.wireOp",EDGE,"E0.bottom"),sQuery(id+"F0.wireOp",EDGE,"E0.top"),sQuery(id+"F0.wireOp",EDGE,"E0.left"),sQuery(id+"F0.wireOp",EDGE,"E0.right")])],"isStart":true}),makeQuery(id+"F27.opExtrude","CAP_FACE",FACE,{"disambiguationData":[OSD([sQuery(id+"F26.wireOp",EDGE,"E24")])],"isStart":true})]});
            var sketch = newSketch(context, id + "F28", { "sketchPlane" : qUnion([Q0])});
            skCircle(sketch, "E28", {"center": v(0, 36) * mm, "radius": 15 * mm});
            skSolve(sketch);
        }
        {
            var Q0;
            Q0 = qSketchRegion(id + "F28", true);
            extrude(context, id + "F29", {"entities" : qUnion([Q0]), "operationType" : NewBodyOperationType.REMOVE, "oppositeDirection" : true, "depth" : 25 * mm, "offsetDistance" : 25 * mm});
        }
    });
